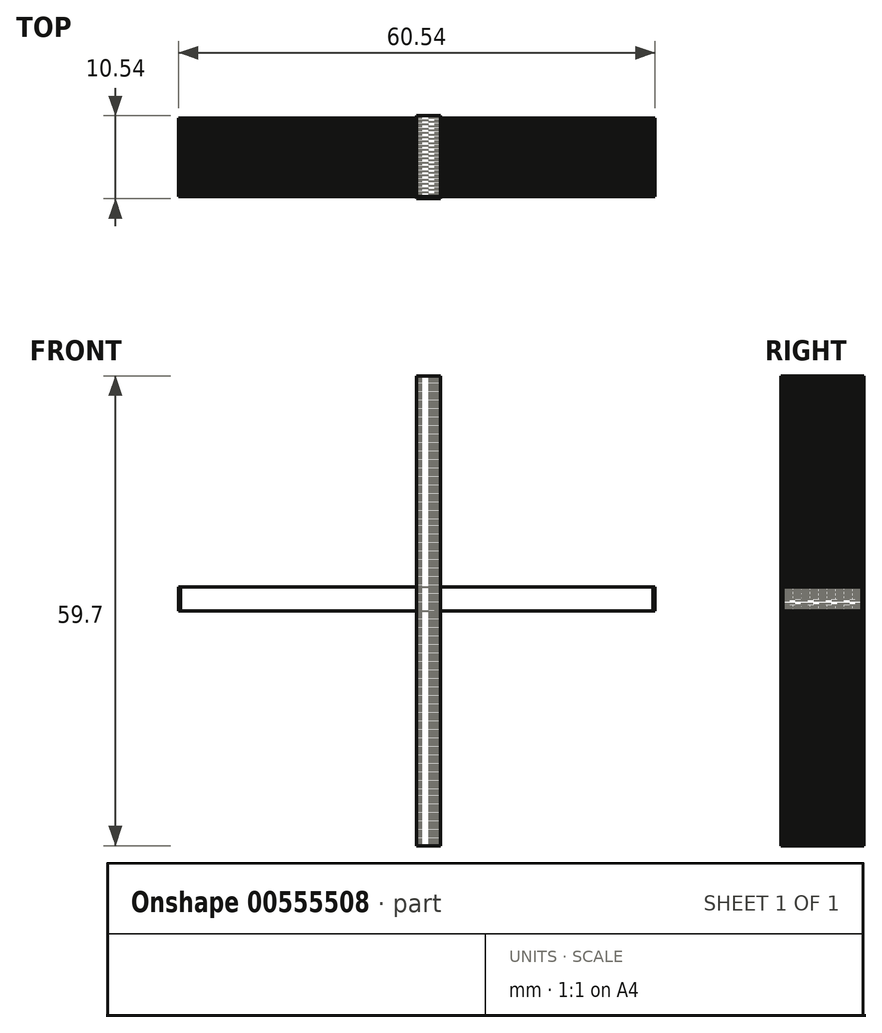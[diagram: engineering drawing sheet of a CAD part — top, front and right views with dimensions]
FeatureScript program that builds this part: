
annotation { "Feature Type Name" : "Feature", "Feature Type Description" : "" }
export const myFeature = defineFeature(function(context is Context, id is Id, definition is map)
    precondition{}
    {
        {
            var Q0;
            Q0=qCreatedBy(makeId("Top.planeOp"),FACE);
            var sketch = newSketch(context, id + "F0", { "sketchPlane" : qUnion([Q0])});
            skLineSegment(sketch, "E0.bottom", {"start": v(10, 5) * mm, "end": v(-10, 5) * mm});
            skLineSegment(sketch, "E0.top", {"start": v(10, -5) * mm, "end": v(-10, -5) * mm});
            skLineSegment(sketch, "E0.left", {"start": v(10, 5) * mm, "end": v(10, -5) * mm});
            skLineSegment(sketch, "E0.right", {"start": v(-10, 5) * mm, "end": v(-10, -5) * mm});
            skPoint(sketch, "E0.middle", {"position": v(0, 0) * mm});
            skLineSegment(sketch, "E1", {"start": v(-10, 4.73) * mm, "end": v(10, 4.73) * mm});
            skLineSegment(sketch, "E2.bottom", {"start": v(-10, 5) * mm, "end": v(-10.27, 5) * mm});
            skLineSegment(sketch, "E2.top", {"start": v(-10, -5) * mm, "end": v(-10.27, -5) * mm});
            skLineSegment(sketch, "E2.right", {"start": v(-10.27, 5) * mm, "end": v(-10.27, -5) * mm});
            skLineSegment(sketch, "E3.MirrorCS", {"start": v(10, 4.46) * mm, "end": v(-10, 4.46) * mm});
            skLineSegment(sketch, "E4.MirrorCS", {"start": v(10, 3.92) * mm, "end": v(-10, 3.92) * mm});
            skLineSegment(sketch, "E5.MirrorCS", {"start": v(-10, 4.19) * mm, "end": v(10, 4.2) * mm});
            skLineSegment(sketch, "E6.MirrorCS", {"start": v(-10, 3.65) * mm, "end": v(10, 3.65) * mm});
            skLineSegment(sketch, "E7.MirrorCS", {"start": v(10, 3.38) * mm, "end": v(-10, 3.38) * mm});
            skLineSegment(sketch, "E8.MirrorCS", {"start": v(-10, 3.11) * mm, "end": v(10, 3.11) * mm});
            skLineSegment(sketch, "E9.MirrorCS", {"start": v(10, 2.84) * mm, "end": v(-10, 2.84) * mm});
            skLineSegment(sketch, "E10.MirrorCS", {"start": v(-10, 2.57) * mm, "end": v(10, 2.57) * mm});
            skLineSegment(sketch, "E11.MirrorCS", {"start": v(10, 2.3) * mm, "end": v(-10, 2.3) * mm});
            skLineSegment(sketch, "E12.MirrorCS", {"start": v(-10, 2.03) * mm, "end": v(10, 2.03) * mm});
            skLineSegment(sketch, "E13.MirrorCS", {"start": v(10, 1.76) * mm, "end": v(-10, 1.76) * mm});
            skLineSegment(sketch, "E14.MirrorCS", {"start": v(-10, 1.49) * mm, "end": v(10, 1.5) * mm});
            skLineSegment(sketch, "E15.MirrorCS", {"start": v(10, 1.22) * mm, "end": v(-10, 1.22) * mm});
            skLineSegment(sketch, "E16.MirrorCS", {"start": v(-10, 0.95) * mm, "end": v(10, 0.95) * mm});
            skLineSegment(sketch, "E17.MirrorCS", {"start": v(10, 0.68) * mm, "end": v(-10, 0.68) * mm});
            skLineSegment(sketch, "E18.MirrorCS", {"start": v(-10, 0.4) * mm, "end": v(10, 0.4) * mm});
            skLineSegment(sketch, "E19.MirrorCS", {"start": v(10, 0.14) * mm, "end": v(-10, 0.14) * mm});
            skLineSegment(sketch, "E20.MirrorCS", {"start": v(-10, -0.13) * mm, "end": v(10, -0.13) * mm});
            skLineSegment(sketch, "E21.MirrorCS", {"start": v(10, -0.4) * mm, "end": v(-10, -0.4) * mm});
            skLineSegment(sketch, "E22.MirrorCS", {"start": v(-10, -0.67) * mm, "end": v(10, -0.67) * mm});
            skLineSegment(sketch, "E23.MirrorCS", {"start": v(10, -0.94) * mm, "end": v(-10, -0.94) * mm});
            skLineSegment(sketch, "E24.MirrorCS", {"start": v(-10, -1.21) * mm, "end": v(10, -1.21) * mm});
            skLineSegment(sketch, "E25.MirrorCS", {"start": v(10, -1.48) * mm, "end": v(-10, -1.48) * mm});
            skLineSegment(sketch, "E26.MirrorCS", {"start": v(-10, -1.75) * mm, "end": v(10, -1.75) * mm});
            skLineSegment(sketch, "E27.MirrorCS", {"start": v(10, -2.02) * mm, "end": v(-10, -2.02) * mm});
            skLineSegment(sketch, "E28.MirrorCS", {"start": v(-10, -2.3) * mm, "end": v(10, -2.3) * mm});
            skLineSegment(sketch, "E29.MirrorCS", {"start": v(10, -2.56) * mm, "end": v(-10, -2.56) * mm});
            skLineSegment(sketch, "E30.MirrorCS", {"start": v(-10, -2.83) * mm, "end": v(10, -2.83) * mm});
            skLineSegment(sketch, "E31.MirrorCS", {"start": v(10, -3.1) * mm, "end": v(-10, -3.1) * mm});
            skLineSegment(sketch, "E32.MirrorCS", {"start": v(-10, -3.37) * mm, "end": v(10, -3.37) * mm});
            skLineSegment(sketch, "E33.MirrorCS", {"start": v(10, -3.64) * mm, "end": v(-10, -3.64) * mm});
            skLineSegment(sketch, "E34.MirrorCS", {"start": v(-10, -3.91) * mm, "end": v(10, -3.91) * mm});
            skLineSegment(sketch, "E35.MirrorCS", {"start": v(10, -4.18) * mm, "end": v(-10, -4.18) * mm});
            skLineSegment(sketch, "E36.MirrorCS", {"start": v(-10, -4.45) * mm, "end": v(10, -4.45) * mm});
            skLineSegment(sketch, "E37.MirrorCS", {"start": v(10, -4.72) * mm, "end": v(-10, -4.72) * mm});
            skLineSegment(sketch, "E38.MirrorCS", {"start": v(-10, -5) * mm, "end": v(10, -5) * mm});
            skLineSegment(sketch, "E39.bottom", {"start": v(10, 5) * mm, "end": v(10.27, 5) * mm});
            skLineSegment(sketch, "E39.top", {"start": v(10, -5) * mm, "end": v(10.27, -5) * mm});
            skLineSegment(sketch, "E39.right", {"start": v(10.27, 5) * mm, "end": v(10.27, -5) * mm});
            skSolve(sketch);
        }
        {
            var Q0;
            Q0=qCreatedBy(makeId("Top.planeOp"),FACE);
            var sketch = newSketch(context, id + "F1", { "sketchPlane" : qUnion([Q0])});
            skLineSegment(sketch, "E40.bottom", {"start": v(30, 5) * mm, "end": v(-30, 5) * mm});
            skLineSegment(sketch, "E40.top", {"start": v(30, -5) * mm, "end": v(-30, -5) * mm});
            skLineSegment(sketch, "E40.left", {"start": v(30, 5) * mm, "end": v(30, -5) * mm});
            skLineSegment(sketch, "E40.right", {"start": v(-30, 5) * mm, "end": v(-30, -5) * mm});
            skPoint(sketch, "E40.middle", {"position": v(0, 0) * mm});
            skLineSegment(sketch, "E41", {"start": v(-30, 4.73) * mm, "end": v(30, 4.73) * mm});
            skLineSegment(sketch, "E42.bottom", {"start": v(-30, 5) * mm, "end": v(-30.27, 5) * mm});
            skLineSegment(sketch, "E42.top", {"start": v(-30, -5) * mm, "end": v(-30.27, -5) * mm});
            skLineSegment(sketch, "E42.right", {"start": v(-30.27, 5) * mm, "end": v(-30.27, -5) * mm});
            skLineSegment(sketch, "E43.MirrorCS", {"start": v(30, 4.46) * mm, "end": v(-30, 4.46) * mm});
            skLineSegment(sketch, "E44.MirrorCS", {"start": v(30, 3.92) * mm, "end": v(-30, 3.92) * mm});
            skLineSegment(sketch, "E45.MirrorCS", {"start": v(-30, 4.19) * mm, "end": v(30, 4.19) * mm});
            skLineSegment(sketch, "E46.MirrorCS", {"start": v(-30, 3.65) * mm, "end": v(30, 3.65) * mm});
            skLineSegment(sketch, "E47.MirrorCS", {"start": v(30, 3.38) * mm, "end": v(-30, 3.38) * mm});
            skLineSegment(sketch, "E48.MirrorCS", {"start": v(-30, 3.1) * mm, "end": v(30, 3.1) * mm});
            skLineSegment(sketch, "E49.MirrorCS", {"start": v(30, 2.84) * mm, "end": v(-30, 2.84) * mm});
            skLineSegment(sketch, "E50.MirrorCS", {"start": v(-30, 2.57) * mm, "end": v(30, 2.57) * mm});
            skLineSegment(sketch, "E51.MirrorCS", {"start": v(30, 2.3) * mm, "end": v(-30, 2.3) * mm});
            skLineSegment(sketch, "E52.MirrorCS", {"start": v(-30, 2.03) * mm, "end": v(30, 2.03) * mm});
            skLineSegment(sketch, "E53.MirrorCS", {"start": v(30, 1.76) * mm, "end": v(-30, 1.76) * mm});
            skLineSegment(sketch, "E54.MirrorCS", {"start": v(-30, 1.49) * mm, "end": v(30, 1.49) * mm});
            skLineSegment(sketch, "E55.MirrorCS", {"start": v(30, 1.22) * mm, "end": v(-30, 1.22) * mm});
            skLineSegment(sketch, "E56.MirrorCS", {"start": v(-30, 0.95) * mm, "end": v(30, 0.95) * mm});
            skLineSegment(sketch, "E57.MirrorCS", {"start": v(30, 0.68) * mm, "end": v(-30, 0.68) * mm});
            skLineSegment(sketch, "E58.MirrorCS", {"start": v(-30, 0.4) * mm, "end": v(30, 0.4) * mm});
            skLineSegment(sketch, "E59.MirrorCS", {"start": v(30, 0.14) * mm, "end": v(-30, 0.14) * mm});
            skLineSegment(sketch, "E60.MirrorCS", {"start": v(-30, -0.13) * mm, "end": v(30, -0.13) * mm});
            skLineSegment(sketch, "E61.MirrorCS", {"start": v(30, -0.4) * mm, "end": v(-30, -0.4) * mm});
            skLineSegment(sketch, "E62.MirrorCS", {"start": v(-30, -0.67) * mm, "end": v(30, -0.67) * mm});
            skLineSegment(sketch, "E63.MirrorCS", {"start": v(30, -0.94) * mm, "end": v(-30, -0.94) * mm});
            skLineSegment(sketch, "E64.MirrorCS", {"start": v(-30, -1.21) * mm, "end": v(30, -1.21) * mm});
            skLineSegment(sketch, "E65.MirrorCS", {"start": v(30, -1.48) * mm, "end": v(-30, -1.48) * mm});
            skLineSegment(sketch, "E66.MirrorCS", {"start": v(-30, -1.75) * mm, "end": v(30, -1.75) * mm});
            skLineSegment(sketch, "E67.MirrorCS", {"start": v(30, -2.02) * mm, "end": v(-30, -2.02) * mm});
            skLineSegment(sketch, "E68.MirrorCS", {"start": v(-30, -2.3) * mm, "end": v(30, -2.3) * mm});
            skLineSegment(sketch, "E69.MirrorCS", {"start": v(30, -2.56) * mm, "end": v(-30, -2.56) * mm});
            skLineSegment(sketch, "E70.MirrorCS", {"start": v(-30, -2.83) * mm, "end": v(30, -2.83) * mm});
            skLineSegment(sketch, "E71.MirrorCS", {"start": v(30, -3.1) * mm, "end": v(-30, -3.1) * mm});
            skLineSegment(sketch, "E72.MirrorCS", {"start": v(-30, -3.37) * mm, "end": v(30, -3.37) * mm});
            skLineSegment(sketch, "E73.MirrorCS", {"start": v(30, -3.64) * mm, "end": v(-30, -3.64) * mm});
            skLineSegment(sketch, "E74.MirrorCS", {"start": v(-30, -3.91) * mm, "end": v(30, -3.91) * mm});
            skLineSegment(sketch, "E75.MirrorCS", {"start": v(30, -4.18) * mm, "end": v(-30, -4.18) * mm});
            skLineSegment(sketch, "E76.MirrorCS", {"start": v(-30, -4.45) * mm, "end": v(30, -4.45) * mm});
            skLineSegment(sketch, "E77.MirrorCS", {"start": v(30, -4.72) * mm, "end": v(-30, -4.72) * mm});
            skLineSegment(sketch, "E78.MirrorCS", {"start": v(-30, -5) * mm, "end": v(30, -5) * mm});
            skLineSegment(sketch, "E79.bottom", {"start": v(30, 5) * mm, "end": v(30.27, 5) * mm});
            skLineSegment(sketch, "E79.top", {"start": v(30, -4.99) * mm, "end": v(30.27, -4.99) * mm});
            skLineSegment(sketch, "E79.left", {"start": v(30, 5) * mm, "end": v(30, -4.99) * mm});
            skLineSegment(sketch, "E79.right", {"start": v(30.27, 5) * mm, "end": v(30.27, -4.99) * mm});
            skSolve(sketch);
        }
        {
            var Q0;
            {var subQ38=sQuery(id+"F1.wireOp",EDGE,"E42.bottom");Q0=makeQuery(id+"F1.imprint","IMPRINT",FACE,{"disambiguationData":[TD([[makeQuery(id+"F1.imprint","IMPRINT",EDGE,{"derivedFrom":subQ38}),1.0]])]});}
            var Q1;
            {var subQ0=sQuery(id+"F1.wireOp",EDGE,"E40.bottom");Q1=makeQuery(id+"F1.imprint","IMPRINT",FACE,{"disambiguationData":[TD([[makeQuery(id+"F1.imprint","IMPRINT",EDGE,{"derivedFrom":subQ0}),1.0]])]});}
            var Q2;
            {var subQ0=sQuery(id+"F1.wireOp",EDGE,"E43.MirrorCS");Q2=makeQuery(id+"F1.imprint","IMPRINT",FACE,{"disambiguationData":[TD([[makeQuery(id+"F1.imprint","IMPRINT",EDGE,{"derivedFrom":subQ0}),1.0]])]});}
            var Q3;
            {var subQ0=sQuery(id+"F1.wireOp",EDGE,"E44.MirrorCS");Q3=makeQuery(id+"F1.imprint","IMPRINT",FACE,{"disambiguationData":[TD([[makeQuery(id+"F1.imprint","IMPRINT",EDGE,{"derivedFrom":subQ0}),1.0]])]});}
            var Q4;
            {var subQ0=sQuery(id+"F1.wireOp",EDGE,"E47.MirrorCS");Q4=makeQuery(id+"F1.imprint","IMPRINT",FACE,{"disambiguationData":[TD([[makeQuery(id+"F1.imprint","IMPRINT",EDGE,{"derivedFrom":subQ0}),1.0]])]});}
            var Q5;
            {var subQ0=sQuery(id+"F1.wireOp",EDGE,"E49.MirrorCS");Q5=makeQuery(id+"F1.imprint","IMPRINT",FACE,{"disambiguationData":[TD([[makeQuery(id+"F1.imprint","IMPRINT",EDGE,{"derivedFrom":subQ0}),1.0]])]});}
            var Q6;
            {var subQ0=sQuery(id+"F1.wireOp",EDGE,"E51.MirrorCS");Q6=makeQuery(id+"F1.imprint","IMPRINT",FACE,{"disambiguationData":[TD([[makeQuery(id+"F1.imprint","IMPRINT",EDGE,{"derivedFrom":subQ0}),1.0]])]});}
            var Q7;
            {var subQ0=sQuery(id+"F1.wireOp",EDGE,"E53.MirrorCS");Q7=makeQuery(id+"F1.imprint","IMPRINT",FACE,{"disambiguationData":[TD([[makeQuery(id+"F1.imprint","IMPRINT",EDGE,{"derivedFrom":subQ0}),1.0]])]});}
            var Q8;
            {var subQ0=sQuery(id+"F1.wireOp",EDGE,"E55.MirrorCS");Q8=makeQuery(id+"F1.imprint","IMPRINT",FACE,{"disambiguationData":[TD([[makeQuery(id+"F1.imprint","IMPRINT",EDGE,{"derivedFrom":subQ0}),1.0]])]});}
            var Q9;
            {var subQ0=sQuery(id+"F1.wireOp",EDGE,"E57.MirrorCS");Q9=makeQuery(id+"F1.imprint","IMPRINT",FACE,{"disambiguationData":[TD([[makeQuery(id+"F1.imprint","IMPRINT",EDGE,{"derivedFrom":subQ0}),1.0]])]});}
            var Q10;
            {var subQ0=sQuery(id+"F1.wireOp",EDGE,"E59.MirrorCS");Q10=makeQuery(id+"F1.imprint","IMPRINT",FACE,{"disambiguationData":[TD([[makeQuery(id+"F1.imprint","IMPRINT",EDGE,{"derivedFrom":subQ0}),1.0]])]});}
            var Q11;
            {var subQ0=sQuery(id+"F1.wireOp",EDGE,"E61.MirrorCS");Q11=makeQuery(id+"F1.imprint","IMPRINT",FACE,{"disambiguationData":[TD([[makeQuery(id+"F1.imprint","IMPRINT",EDGE,{"derivedFrom":subQ0}),1.0]])]});}
            var Q12;
            {var subQ0=sQuery(id+"F1.wireOp",EDGE,"E63.MirrorCS");Q12=makeQuery(id+"F1.imprint","IMPRINT",FACE,{"disambiguationData":[TD([[makeQuery(id+"F1.imprint","IMPRINT",EDGE,{"derivedFrom":subQ0}),1.0]])]});}
            var Q13;
            {var subQ0=sQuery(id+"F1.wireOp",EDGE,"E65.MirrorCS");Q13=makeQuery(id+"F1.imprint","IMPRINT",FACE,{"disambiguationData":[TD([[makeQuery(id+"F1.imprint","IMPRINT",EDGE,{"derivedFrom":subQ0}),1.0]])]});}
            var Q14;
            {var subQ2=sQuery(id+"F1.wireOp",EDGE,"E67.MirrorCS");Q14=makeQuery(id+"F1.imprint","IMPRINT",FACE,{"disambiguationData":[TD([[makeQuery(id+"F1.imprint","IMPRINT",EDGE,{"derivedFrom":subQ2}),1.0]])]});}
            var Q15;
            {var subQ0=sQuery(id+"F1.wireOp",EDGE,"E69.MirrorCS");Q15=makeQuery(id+"F1.imprint","IMPRINT",FACE,{"disambiguationData":[TD([[makeQuery(id+"F1.imprint","IMPRINT",EDGE,{"derivedFrom":subQ0}),1.0]])]});}
            var Q16;
            {var subQ0=sQuery(id+"F1.wireOp",EDGE,"E71.MirrorCS");Q16=makeQuery(id+"F1.imprint","IMPRINT",FACE,{"disambiguationData":[TD([[makeQuery(id+"F1.imprint","IMPRINT",EDGE,{"derivedFrom":subQ0}),1.0]])]});}
            var Q17;
            {var subQ0=sQuery(id+"F1.wireOp",EDGE,"E73.MirrorCS");Q17=makeQuery(id+"F1.imprint","IMPRINT",FACE,{"disambiguationData":[TD([[makeQuery(id+"F1.imprint","IMPRINT",EDGE,{"derivedFrom":subQ0}),1.0]])]});}
            var Q18;
            {var subQ0=sQuery(id+"F1.wireOp",EDGE,"E75.MirrorCS");Q18=makeQuery(id+"F1.imprint","IMPRINT",FACE,{"disambiguationData":[TD([[makeQuery(id+"F1.imprint","IMPRINT",EDGE,{"derivedFrom":subQ0}),1.0]])]});}
            var Q19;
            {var subQ0=sQuery(id+"F1.wireOp",EDGE,"E77.MirrorCS");Q19=makeQuery(id+"F1.imprint","IMPRINT",FACE,{"disambiguationData":[TD([[makeQuery(id+"F1.imprint","IMPRINT",EDGE,{"derivedFrom":subQ0}),1.0]])]});}
            extrude(context, id + "F2", {"entities" : qUnion([Q0, Q1, Q2, Q3, Q4, Q5, Q6, Q7, Q8, Q9, Q10, Q11, Q12, Q13, Q14, Q15, Q16, Q17, Q18, Q19]), "depth" : 3 * mm, "offsetDistance" : 25 * mm});
        }
        {
            var Q0;
            {var subQ33=sQuery(id+"F1.wireOp",EDGE,"E79.bottom");Q0=makeQuery(id+"F1.imprint","IMPRINT",FACE,{"disambiguationData":[TD([[makeQuery(id+"F1.imprint","IMPRINT",EDGE,{"derivedFrom":subQ33}),-1.0]])]});}
            var Q1;
            {var subQ0=sQuery(id+"F1.wireOp",EDGE,"E41");Q1=makeQuery(id+"F1.imprint","IMPRINT",FACE,{"disambiguationData":[TD([[makeQuery(id+"F1.imprint","IMPRINT",EDGE,{"derivedFrom":subQ0}),-1.0]])]});}
            var Q2;
            {var subQ0=sQuery(id+"F1.wireOp",EDGE,"E44.MirrorCS");Q2=makeQuery(id+"F1.imprint","IMPRINT",FACE,{"disambiguationData":[TD([[makeQuery(id+"F1.imprint","IMPRINT",EDGE,{"derivedFrom":subQ0}),-1.0]])]});}
            var Q3;
            {var subQ0=sQuery(id+"F1.wireOp",EDGE,"E46.MirrorCS");Q3=makeQuery(id+"F1.imprint","IMPRINT",FACE,{"disambiguationData":[TD([[makeQuery(id+"F1.imprint","IMPRINT",EDGE,{"derivedFrom":subQ0}),-1.0]])]});}
            var Q4;
            {var subQ0=sQuery(id+"F1.wireOp",EDGE,"E48.MirrorCS");Q4=makeQuery(id+"F1.imprint","IMPRINT",FACE,{"disambiguationData":[TD([[makeQuery(id+"F1.imprint","IMPRINT",EDGE,{"derivedFrom":subQ0}),-1.0]])]});}
            var Q5;
            {var subQ0=sQuery(id+"F1.wireOp",EDGE,"E50.MirrorCS");Q5=makeQuery(id+"F1.imprint","IMPRINT",FACE,{"disambiguationData":[TD([[makeQuery(id+"F1.imprint","IMPRINT",EDGE,{"derivedFrom":subQ0}),-1.0]])]});}
            var Q6;
            {var subQ0=sQuery(id+"F1.wireOp",EDGE,"E52.MirrorCS");Q6=makeQuery(id+"F1.imprint","IMPRINT",FACE,{"disambiguationData":[TD([[makeQuery(id+"F1.imprint","IMPRINT",EDGE,{"derivedFrom":subQ0}),-1.0]])]});}
            var Q7;
            {var subQ0=sQuery(id+"F1.wireOp",EDGE,"E54.MirrorCS");Q7=makeQuery(id+"F1.imprint","IMPRINT",FACE,{"disambiguationData":[TD([[makeQuery(id+"F1.imprint","IMPRINT",EDGE,{"derivedFrom":subQ0}),-1.0]])]});}
            var Q8;
            {var subQ0=sQuery(id+"F1.wireOp",EDGE,"E56.MirrorCS");Q8=makeQuery(id+"F1.imprint","IMPRINT",FACE,{"disambiguationData":[TD([[makeQuery(id+"F1.imprint","IMPRINT",EDGE,{"derivedFrom":subQ0}),-1.0]])]});}
            var Q9;
            {var subQ0=sQuery(id+"F1.wireOp",EDGE,"E58.MirrorCS");Q9=makeQuery(id+"F1.imprint","IMPRINT",FACE,{"disambiguationData":[TD([[makeQuery(id+"F1.imprint","IMPRINT",EDGE,{"derivedFrom":subQ0}),-1.0]])]});}
            var Q10;
            {var subQ0=sQuery(id+"F1.wireOp",EDGE,"E60.MirrorCS");Q10=makeQuery(id+"F1.imprint","IMPRINT",FACE,{"disambiguationData":[TD([[makeQuery(id+"F1.imprint","IMPRINT",EDGE,{"derivedFrom":subQ0}),-1.0]])]});}
            var Q11;
            {var subQ0=sQuery(id+"F1.wireOp",EDGE,"E62.MirrorCS");Q11=makeQuery(id+"F1.imprint","IMPRINT",FACE,{"disambiguationData":[TD([[makeQuery(id+"F1.imprint","IMPRINT",EDGE,{"derivedFrom":subQ0}),-1.0]])]});}
            var Q12;
            {var subQ0=sQuery(id+"F1.wireOp",EDGE,"E64.MirrorCS");Q12=makeQuery(id+"F1.imprint","IMPRINT",FACE,{"disambiguationData":[TD([[makeQuery(id+"F1.imprint","IMPRINT",EDGE,{"derivedFrom":subQ0}),-1.0]])]});}
            var Q13;
            {var subQ0=sQuery(id+"F1.wireOp",EDGE,"E66.MirrorCS");Q13=makeQuery(id+"F1.imprint","IMPRINT",FACE,{"disambiguationData":[TD([[makeQuery(id+"F1.imprint","IMPRINT",EDGE,{"derivedFrom":subQ0}),-1.0]])]});}
            var Q14;
            {var subQ0=sQuery(id+"F1.wireOp",EDGE,"E68.MirrorCS");Q14=makeQuery(id+"F1.imprint","IMPRINT",FACE,{"disambiguationData":[TD([[makeQuery(id+"F1.imprint","IMPRINT",EDGE,{"derivedFrom":subQ0}),-1.0]])]});}
            var Q15;
            {var subQ0=sQuery(id+"F1.wireOp",EDGE,"E70.MirrorCS");Q15=makeQuery(id+"F1.imprint","IMPRINT",FACE,{"disambiguationData":[TD([[makeQuery(id+"F1.imprint","IMPRINT",EDGE,{"derivedFrom":subQ0}),-1.0]])]});}
            var Q16;
            {var subQ0=sQuery(id+"F1.wireOp",EDGE,"E72.MirrorCS");Q16=makeQuery(id+"F1.imprint","IMPRINT",FACE,{"disambiguationData":[TD([[makeQuery(id+"F1.imprint","IMPRINT",EDGE,{"derivedFrom":subQ0}),-1.0]])]});}
            var Q17;
            {var subQ0=sQuery(id+"F1.wireOp",EDGE,"E74.MirrorCS");Q17=makeQuery(id+"F1.imprint","IMPRINT",FACE,{"disambiguationData":[TD([[makeQuery(id+"F1.imprint","IMPRINT",EDGE,{"derivedFrom":subQ0}),-1.0]])]});}
            var Q18;
            {var subQ0=sQuery(id+"F1.wireOp",EDGE,"E76.MirrorCS");Q18=makeQuery(id+"F1.imprint","IMPRINT",FACE,{"disambiguationData":[TD([[makeQuery(id+"F1.imprint","IMPRINT",EDGE,{"derivedFrom":subQ0}),-1.0]])]});}
            extrude(context, id + "F3", {"entities" : qUnion([Q0, Q1, Q2, Q3, Q4, Q5, Q6, Q7, Q8, Q9, Q10, Q11, Q12, Q13, Q14, Q15, Q16, Q17, Q18]), "depth" : 3 * mm, "offsetDistance" : 25 * mm});
        }
        {
            var Q0;
            {var subQ38=sQuery(id+"F1.wireOp",EDGE,"E42.bottom");Q0=makeQuery(id+"F1.imprint","IMPRINT",FACE,{"disambiguationData":[TD([[makeQuery(id+"F1.imprint","IMPRINT",EDGE,{"derivedFrom":subQ38}),1.0]])]});}
            var Q1;
            {var subQ0=sQuery(id+"F1.wireOp",EDGE,"E40.bottom");Q1=makeQuery(id+"F1.imprint","IMPRINT",FACE,{"disambiguationData":[TD([[makeQuery(id+"F1.imprint","IMPRINT",EDGE,{"derivedFrom":subQ0}),1.0]])]});}
            var Q2;
            {var subQ0=sQuery(id+"F1.wireOp",EDGE,"E41");Q2=makeQuery(id+"F1.imprint","IMPRINT",FACE,{"disambiguationData":[TD([[makeQuery(id+"F1.imprint","IMPRINT",EDGE,{"derivedFrom":subQ0}),-1.0]])]});}
            var Q3;
            {var subQ0=sQuery(id+"F1.wireOp",EDGE,"E43.MirrorCS");Q3=makeQuery(id+"F1.imprint","IMPRINT",FACE,{"disambiguationData":[TD([[makeQuery(id+"F1.imprint","IMPRINT",EDGE,{"derivedFrom":subQ0}),1.0]])]});}
            var Q4;
            {var subQ0=sQuery(id+"F1.wireOp",EDGE,"E44.MirrorCS");Q4=makeQuery(id+"F1.imprint","IMPRINT",FACE,{"disambiguationData":[TD([[makeQuery(id+"F1.imprint","IMPRINT",EDGE,{"derivedFrom":subQ0}),1.0]])]});}
            var Q5;
            {var subQ0=sQuery(id+"F1.wireOp",EDGE,"E47.MirrorCS");Q5=makeQuery(id+"F1.imprint","IMPRINT",FACE,{"disambiguationData":[TD([[makeQuery(id+"F1.imprint","IMPRINT",EDGE,{"derivedFrom":subQ0}),1.0]])]});}
            var Q6;
            {var subQ0=sQuery(id+"F1.wireOp",EDGE,"E46.MirrorCS");Q6=makeQuery(id+"F1.imprint","IMPRINT",FACE,{"disambiguationData":[TD([[makeQuery(id+"F1.imprint","IMPRINT",EDGE,{"derivedFrom":subQ0}),-1.0]])]});}
            var Q7;
            {var subQ0=sQuery(id+"F1.wireOp",EDGE,"E49.MirrorCS");Q7=makeQuery(id+"F1.imprint","IMPRINT",FACE,{"disambiguationData":[TD([[makeQuery(id+"F1.imprint","IMPRINT",EDGE,{"derivedFrom":subQ0}),1.0]])]});}
            var Q8;
            {var subQ0=sQuery(id+"F1.wireOp",EDGE,"E50.MirrorCS");Q8=makeQuery(id+"F1.imprint","IMPRINT",FACE,{"disambiguationData":[TD([[makeQuery(id+"F1.imprint","IMPRINT",EDGE,{"derivedFrom":subQ0}),-1.0]])]});}
            var Q9;
            {var subQ0=sQuery(id+"F1.wireOp",EDGE,"E51.MirrorCS");Q9=makeQuery(id+"F1.imprint","IMPRINT",FACE,{"disambiguationData":[TD([[makeQuery(id+"F1.imprint","IMPRINT",EDGE,{"derivedFrom":subQ0}),1.0]])]});}
            var Q10;
            {var subQ0=sQuery(id+"F1.wireOp",EDGE,"E53.MirrorCS");Q10=makeQuery(id+"F1.imprint","IMPRINT",FACE,{"disambiguationData":[TD([[makeQuery(id+"F1.imprint","IMPRINT",EDGE,{"derivedFrom":subQ0}),1.0]])]});}
            var Q11;
            {var subQ0=sQuery(id+"F1.wireOp",EDGE,"E54.MirrorCS");Q11=makeQuery(id+"F1.imprint","IMPRINT",FACE,{"disambiguationData":[TD([[makeQuery(id+"F1.imprint","IMPRINT",EDGE,{"derivedFrom":subQ0}),-1.0]])]});}
            var Q12;
            {var subQ0=sQuery(id+"F1.wireOp",EDGE,"E55.MirrorCS");Q12=makeQuery(id+"F1.imprint","IMPRINT",FACE,{"disambiguationData":[TD([[makeQuery(id+"F1.imprint","IMPRINT",EDGE,{"derivedFrom":subQ0}),1.0]])]});}
            var Q13;
            {var subQ0=sQuery(id+"F1.wireOp",EDGE,"E57.MirrorCS");Q13=makeQuery(id+"F1.imprint","IMPRINT",FACE,{"disambiguationData":[TD([[makeQuery(id+"F1.imprint","IMPRINT",EDGE,{"derivedFrom":subQ0}),1.0]])]});}
            var Q14;
            {var subQ0=sQuery(id+"F1.wireOp",EDGE,"E58.MirrorCS");Q14=makeQuery(id+"F1.imprint","IMPRINT",FACE,{"disambiguationData":[TD([[makeQuery(id+"F1.imprint","IMPRINT",EDGE,{"derivedFrom":subQ0}),-1.0]])]});}
            var Q15;
            {var subQ0=sQuery(id+"F1.wireOp",EDGE,"E59.MirrorCS");Q15=makeQuery(id+"F1.imprint","IMPRINT",FACE,{"disambiguationData":[TD([[makeQuery(id+"F1.imprint","IMPRINT",EDGE,{"derivedFrom":subQ0}),1.0]])]});}
            var Q16;
            {var subQ0=sQuery(id+"F1.wireOp",EDGE,"E61.MirrorCS");Q16=makeQuery(id+"F1.imprint","IMPRINT",FACE,{"disambiguationData":[TD([[makeQuery(id+"F1.imprint","IMPRINT",EDGE,{"derivedFrom":subQ0}),1.0]])]});}
            var Q17;
            {var subQ0=sQuery(id+"F1.wireOp",EDGE,"E62.MirrorCS");Q17=makeQuery(id+"F1.imprint","IMPRINT",FACE,{"disambiguationData":[TD([[makeQuery(id+"F1.imprint","IMPRINT",EDGE,{"derivedFrom":subQ0}),-1.0]])]});}
            var Q18;
            {var subQ0=sQuery(id+"F1.wireOp",EDGE,"E63.MirrorCS");Q18=makeQuery(id+"F1.imprint","IMPRINT",FACE,{"disambiguationData":[TD([[makeQuery(id+"F1.imprint","IMPRINT",EDGE,{"derivedFrom":subQ0}),1.0]])]});}
            var Q19;
            {var subQ0=sQuery(id+"F1.wireOp",EDGE,"E65.MirrorCS");Q19=makeQuery(id+"F1.imprint","IMPRINT",FACE,{"disambiguationData":[TD([[makeQuery(id+"F1.imprint","IMPRINT",EDGE,{"derivedFrom":subQ0}),1.0]])]});}
            var Q20;
            {var subQ0=sQuery(id+"F1.wireOp",EDGE,"E66.MirrorCS");Q20=makeQuery(id+"F1.imprint","IMPRINT",FACE,{"disambiguationData":[TD([[makeQuery(id+"F1.imprint","IMPRINT",EDGE,{"derivedFrom":subQ0}),-1.0]])]});}
            var Q21;
            {var subQ2=sQuery(id+"F1.wireOp",EDGE,"E67.MirrorCS");Q21=makeQuery(id+"F1.imprint","IMPRINT",FACE,{"disambiguationData":[TD([[makeQuery(id+"F1.imprint","IMPRINT",EDGE,{"derivedFrom":subQ2}),1.0]])]});}
            var Q22;
            {var subQ0=sQuery(id+"F1.wireOp",EDGE,"E69.MirrorCS");Q22=makeQuery(id+"F1.imprint","IMPRINT",FACE,{"disambiguationData":[TD([[makeQuery(id+"F1.imprint","IMPRINT",EDGE,{"derivedFrom":subQ0}),1.0]])]});}
            var Q23;
            {var subQ0=sQuery(id+"F1.wireOp",EDGE,"E70.MirrorCS");Q23=makeQuery(id+"F1.imprint","IMPRINT",FACE,{"disambiguationData":[TD([[makeQuery(id+"F1.imprint","IMPRINT",EDGE,{"derivedFrom":subQ0}),-1.0]])]});}
            var Q24;
            {var subQ0=sQuery(id+"F1.wireOp",EDGE,"E71.MirrorCS");Q24=makeQuery(id+"F1.imprint","IMPRINT",FACE,{"disambiguationData":[TD([[makeQuery(id+"F1.imprint","IMPRINT",EDGE,{"derivedFrom":subQ0}),1.0]])]});}
            var Q25;
            {var subQ0=sQuery(id+"F1.wireOp",EDGE,"E73.MirrorCS");Q25=makeQuery(id+"F1.imprint","IMPRINT",FACE,{"disambiguationData":[TD([[makeQuery(id+"F1.imprint","IMPRINT",EDGE,{"derivedFrom":subQ0}),1.0]])]});}
            var Q26;
            {var subQ0=sQuery(id+"F1.wireOp",EDGE,"E74.MirrorCS");Q26=makeQuery(id+"F1.imprint","IMPRINT",FACE,{"disambiguationData":[TD([[makeQuery(id+"F1.imprint","IMPRINT",EDGE,{"derivedFrom":subQ0}),-1.0]])]});}
            var Q27;
            {var subQ0=sQuery(id+"F1.wireOp",EDGE,"E75.MirrorCS");Q27=makeQuery(id+"F1.imprint","IMPRINT",FACE,{"disambiguationData":[TD([[makeQuery(id+"F1.imprint","IMPRINT",EDGE,{"derivedFrom":subQ0}),1.0]])]});}
            var Q28;
            {var subQ0=sQuery(id+"F1.wireOp",EDGE,"E77.MirrorCS");Q28=makeQuery(id+"F1.imprint","IMPRINT",FACE,{"disambiguationData":[TD([[makeQuery(id+"F1.imprint","IMPRINT",EDGE,{"derivedFrom":subQ0}),1.0]])]});}
            extrude(context, id + "F4", {"entities" : qUnion([Q0, Q1, Q2, Q3, Q4, Q5, Q6, Q7, Q8, Q9, Q10, Q11, Q12, Q13, Q14, Q15, Q16, Q17, Q18, Q19, Q20, Q21, Q22, Q23, Q24, Q25, Q26, Q27, Q28]), "depth" : 3 * mm, "offsetDistance" : 25 * mm});
        }
        {
            var Q0;
            {var subQ0=sQuery(id+"F1.wireOp",EDGE,"E44.MirrorCS");Q0=makeQuery(id+"F1.imprint","IMPRINT",FACE,{"disambiguationData":[TD([[makeQuery(id+"F1.imprint","IMPRINT",EDGE,{"derivedFrom":subQ0}),-1.0]])]});}
            var Q1;
            {var subQ0=sQuery(id+"F1.wireOp",EDGE,"E48.MirrorCS");Q1=makeQuery(id+"F1.imprint","IMPRINT",FACE,{"disambiguationData":[TD([[makeQuery(id+"F1.imprint","IMPRINT",EDGE,{"derivedFrom":subQ0}),-1.0]])]});}
            var Q2;
            {var subQ0=sQuery(id+"F1.wireOp",EDGE,"E52.MirrorCS");Q2=makeQuery(id+"F1.imprint","IMPRINT",FACE,{"disambiguationData":[TD([[makeQuery(id+"F1.imprint","IMPRINT",EDGE,{"derivedFrom":subQ0}),-1.0]])]});}
            var Q3;
            {var subQ0=sQuery(id+"F1.wireOp",EDGE,"E56.MirrorCS");Q3=makeQuery(id+"F1.imprint","IMPRINT",FACE,{"disambiguationData":[TD([[makeQuery(id+"F1.imprint","IMPRINT",EDGE,{"derivedFrom":subQ0}),-1.0]])]});}
            var Q4;
            {var subQ0=sQuery(id+"F1.wireOp",EDGE,"E60.MirrorCS");Q4=makeQuery(id+"F1.imprint","IMPRINT",FACE,{"disambiguationData":[TD([[makeQuery(id+"F1.imprint","IMPRINT",EDGE,{"derivedFrom":subQ0}),-1.0]])]});}
            var Q5;
            {var subQ0=sQuery(id+"F1.wireOp",EDGE,"E64.MirrorCS");Q5=makeQuery(id+"F1.imprint","IMPRINT",FACE,{"disambiguationData":[TD([[makeQuery(id+"F1.imprint","IMPRINT",EDGE,{"derivedFrom":subQ0}),-1.0]])]});}
            var Q6;
            {var subQ0=sQuery(id+"F1.wireOp",EDGE,"E68.MirrorCS");Q6=makeQuery(id+"F1.imprint","IMPRINT",FACE,{"disambiguationData":[TD([[makeQuery(id+"F1.imprint","IMPRINT",EDGE,{"derivedFrom":subQ0}),-1.0]])]});}
            var Q7;
            {var subQ0=sQuery(id+"F1.wireOp",EDGE,"E72.MirrorCS");Q7=makeQuery(id+"F1.imprint","IMPRINT",FACE,{"disambiguationData":[TD([[makeQuery(id+"F1.imprint","IMPRINT",EDGE,{"derivedFrom":subQ0}),-1.0]])]});}
            var Q8;
            {var subQ0=sQuery(id+"F1.wireOp",EDGE,"E76.MirrorCS");Q8=makeQuery(id+"F1.imprint","IMPRINT",FACE,{"disambiguationData":[TD([[makeQuery(id+"F1.imprint","IMPRINT",EDGE,{"derivedFrom":subQ0}),-1.0]])]});}
            var Q9;
            {var subQ33=sQuery(id+"F1.wireOp",EDGE,"E79.bottom");Q9=makeQuery(id+"F1.imprint","IMPRINT",FACE,{"disambiguationData":[TD([[makeQuery(id+"F1.imprint","IMPRINT",EDGE,{"derivedFrom":subQ33}),-1.0]])]});}
            extrude(context, id + "F5", {"entities" : qUnion([Q0, Q1, Q2, Q3, Q4, Q5, Q6, Q7, Q8, Q9]), "depth" : 3 * mm, "offsetDistance" : 25 * mm});
        }
        {
            var Q0;
            {var subQ38=sQuery(id+"F1.wireOp",EDGE,"E42.bottom");Q0=makeQuery(id+"F1.imprint","IMPRINT",FACE,{"disambiguationData":[TD([[makeQuery(id+"F1.imprint","IMPRINT",EDGE,{"derivedFrom":subQ38}),1.0]])]});}
            var Q1;
            {var subQ0=sQuery(id+"F1.wireOp",EDGE,"E40.bottom");Q1=makeQuery(id+"F1.imprint","IMPRINT",FACE,{"disambiguationData":[TD([[makeQuery(id+"F1.imprint","IMPRINT",EDGE,{"derivedFrom":subQ0}),1.0]])]});}
            var Q2;
            {var subQ0=sQuery(id+"F1.wireOp",EDGE,"E41");Q2=makeQuery(id+"F1.imprint","IMPRINT",FACE,{"disambiguationData":[TD([[makeQuery(id+"F1.imprint","IMPRINT",EDGE,{"derivedFrom":subQ0}),-1.0]])]});}
            var Q3;
            {var subQ0=sQuery(id+"F1.wireOp",EDGE,"E43.MirrorCS");Q3=makeQuery(id+"F1.imprint","IMPRINT",FACE,{"disambiguationData":[TD([[makeQuery(id+"F1.imprint","IMPRINT",EDGE,{"derivedFrom":subQ0}),1.0]])]});}
            var Q4;
            {var subQ0=sQuery(id+"F1.wireOp",EDGE,"E44.MirrorCS");Q4=makeQuery(id+"F1.imprint","IMPRINT",FACE,{"disambiguationData":[TD([[makeQuery(id+"F1.imprint","IMPRINT",EDGE,{"derivedFrom":subQ0}),-1.0]])]});}
            var Q5;
            {var subQ0=sQuery(id+"F1.wireOp",EDGE,"E44.MirrorCS");Q5=makeQuery(id+"F1.imprint","IMPRINT",FACE,{"disambiguationData":[TD([[makeQuery(id+"F1.imprint","IMPRINT",EDGE,{"derivedFrom":subQ0}),1.0]])]});}
            var Q6;
            {var subQ0=sQuery(id+"F1.wireOp",EDGE,"E47.MirrorCS");Q6=makeQuery(id+"F1.imprint","IMPRINT",FACE,{"disambiguationData":[TD([[makeQuery(id+"F1.imprint","IMPRINT",EDGE,{"derivedFrom":subQ0}),1.0]])]});}
            var Q7;
            {var subQ0=sQuery(id+"F1.wireOp",EDGE,"E48.MirrorCS");Q7=makeQuery(id+"F1.imprint","IMPRINT",FACE,{"disambiguationData":[TD([[makeQuery(id+"F1.imprint","IMPRINT",EDGE,{"derivedFrom":subQ0}),-1.0]])]});}
            var Q8;
            {var subQ0=sQuery(id+"F1.wireOp",EDGE,"E49.MirrorCS");Q8=makeQuery(id+"F1.imprint","IMPRINT",FACE,{"disambiguationData":[TD([[makeQuery(id+"F1.imprint","IMPRINT",EDGE,{"derivedFrom":subQ0}),1.0]])]});}
            var Q9;
            {var subQ0=sQuery(id+"F1.wireOp",EDGE,"E53.MirrorCS");Q9=makeQuery(id+"F1.imprint","IMPRINT",FACE,{"disambiguationData":[TD([[makeQuery(id+"F1.imprint","IMPRINT",EDGE,{"derivedFrom":subQ0}),1.0]])]});}
            var Q10;
            {var subQ0=sQuery(id+"F1.wireOp",EDGE,"E55.MirrorCS");Q10=makeQuery(id+"F1.imprint","IMPRINT",FACE,{"disambiguationData":[TD([[makeQuery(id+"F1.imprint","IMPRINT",EDGE,{"derivedFrom":subQ0}),1.0]])]});}
            var Q11;
            {var subQ0=sQuery(id+"F1.wireOp",EDGE,"E59.MirrorCS");Q11=makeQuery(id+"F1.imprint","IMPRINT",FACE,{"disambiguationData":[TD([[makeQuery(id+"F1.imprint","IMPRINT",EDGE,{"derivedFrom":subQ0}),1.0]])]});}
            var Q12;
            {var subQ0=sQuery(id+"F1.wireOp",EDGE,"E63.MirrorCS");Q12=makeQuery(id+"F1.imprint","IMPRINT",FACE,{"disambiguationData":[TD([[makeQuery(id+"F1.imprint","IMPRINT",EDGE,{"derivedFrom":subQ0}),1.0]])]});}
            var Q13;
            {var subQ0=sQuery(id+"F1.wireOp",EDGE,"E70.MirrorCS");Q13=makeQuery(id+"F1.imprint","IMPRINT",FACE,{"disambiguationData":[TD([[makeQuery(id+"F1.imprint","IMPRINT",EDGE,{"derivedFrom":subQ0}),-1.0]])]});}
            var Q14;
            {var subQ0=sQuery(id+"F1.wireOp",EDGE,"E73.MirrorCS");Q14=makeQuery(id+"F1.imprint","IMPRINT",FACE,{"disambiguationData":[TD([[makeQuery(id+"F1.imprint","IMPRINT",EDGE,{"derivedFrom":subQ0}),1.0]])]});}
            var Q15;
            {var subQ0=sQuery(id+"F1.wireOp",EDGE,"E76.MirrorCS");Q15=makeQuery(id+"F1.imprint","IMPRINT",FACE,{"disambiguationData":[TD([[makeQuery(id+"F1.imprint","IMPRINT",EDGE,{"derivedFrom":subQ0}),-1.0]])]});}
            var Q16;
            {var subQ0=sQuery(id+"F1.wireOp",EDGE,"E77.MirrorCS");Q16=makeQuery(id+"F1.imprint","IMPRINT",FACE,{"disambiguationData":[TD([[makeQuery(id+"F1.imprint","IMPRINT",EDGE,{"derivedFrom":subQ0}),1.0]])]});}
            var Q17;
            {var subQ0=sQuery(id+"F1.wireOp",EDGE,"E74.MirrorCS");Q17=makeQuery(id+"F1.imprint","IMPRINT",FACE,{"disambiguationData":[TD([[makeQuery(id+"F1.imprint","IMPRINT",EDGE,{"derivedFrom":subQ0}),-1.0]])]});}
            var Q18;
            {var subQ0=sQuery(id+"F1.wireOp",EDGE,"E71.MirrorCS");Q18=makeQuery(id+"F1.imprint","IMPRINT",FACE,{"disambiguationData":[TD([[makeQuery(id+"F1.imprint","IMPRINT",EDGE,{"derivedFrom":subQ0}),1.0]])]});}
            var Q19;
            {var subQ0=sQuery(id+"F1.wireOp",EDGE,"E68.MirrorCS");Q19=makeQuery(id+"F1.imprint","IMPRINT",FACE,{"disambiguationData":[TD([[makeQuery(id+"F1.imprint","IMPRINT",EDGE,{"derivedFrom":subQ0}),-1.0]])]});}
            var Q20;
            {var subQ2=sQuery(id+"F1.wireOp",EDGE,"E67.MirrorCS");Q20=makeQuery(id+"F1.imprint","IMPRINT",FACE,{"disambiguationData":[TD([[makeQuery(id+"F1.imprint","IMPRINT",EDGE,{"derivedFrom":subQ2}),1.0]])]});}
            var Q21;
            {var subQ0=sQuery(id+"F1.wireOp",EDGE,"E65.MirrorCS");Q21=makeQuery(id+"F1.imprint","IMPRINT",FACE,{"disambiguationData":[TD([[makeQuery(id+"F1.imprint","IMPRINT",EDGE,{"derivedFrom":subQ0}),1.0]])]});}
            var Q22;
            {var subQ0=sQuery(id+"F1.wireOp",EDGE,"E61.MirrorCS");Q22=makeQuery(id+"F1.imprint","IMPRINT",FACE,{"disambiguationData":[TD([[makeQuery(id+"F1.imprint","IMPRINT",EDGE,{"derivedFrom":subQ0}),1.0]])]});}
            var Q23;
            {var subQ0=sQuery(id+"F1.wireOp",EDGE,"E57.MirrorCS");Q23=makeQuery(id+"F1.imprint","IMPRINT",FACE,{"disambiguationData":[TD([[makeQuery(id+"F1.imprint","IMPRINT",EDGE,{"derivedFrom":subQ0}),1.0]])]});}
            var Q24;
            {var subQ0=sQuery(id+"F1.wireOp",EDGE,"E50.MirrorCS");Q24=makeQuery(id+"F1.imprint","IMPRINT",FACE,{"disambiguationData":[TD([[makeQuery(id+"F1.imprint","IMPRINT",EDGE,{"derivedFrom":subQ0}),-1.0]])]});}
            var Q25;
            {var subQ0=sQuery(id+"F1.wireOp",EDGE,"E46.MirrorCS");Q25=makeQuery(id+"F1.imprint","IMPRINT",FACE,{"disambiguationData":[TD([[makeQuery(id+"F1.imprint","IMPRINT",EDGE,{"derivedFrom":subQ0}),-1.0]])]});}
            var Q26;
            {var subQ0=sQuery(id+"F1.wireOp",EDGE,"E51.MirrorCS");Q26=makeQuery(id+"F1.imprint","IMPRINT",FACE,{"disambiguationData":[TD([[makeQuery(id+"F1.imprint","IMPRINT",EDGE,{"derivedFrom":subQ0}),1.0]])]});}
            var Q27;
            {var subQ0=sQuery(id+"F1.wireOp",EDGE,"E75.MirrorCS");Q27=makeQuery(id+"F1.imprint","IMPRINT",FACE,{"disambiguationData":[TD([[makeQuery(id+"F1.imprint","IMPRINT",EDGE,{"derivedFrom":subQ0}),1.0]])]});}
            var Q28;
            {var subQ0=sQuery(id+"F1.wireOp",EDGE,"E72.MirrorCS");Q28=makeQuery(id+"F1.imprint","IMPRINT",FACE,{"disambiguationData":[TD([[makeQuery(id+"F1.imprint","IMPRINT",EDGE,{"derivedFrom":subQ0}),-1.0]])]});}
            var Q29;
            {var subQ0=sQuery(id+"F1.wireOp",EDGE,"E69.MirrorCS");Q29=makeQuery(id+"F1.imprint","IMPRINT",FACE,{"disambiguationData":[TD([[makeQuery(id+"F1.imprint","IMPRINT",EDGE,{"derivedFrom":subQ0}),1.0]])]});}
            var Q30;
            {var subQ0=sQuery(id+"F1.wireOp",EDGE,"E66.MirrorCS");Q30=makeQuery(id+"F1.imprint","IMPRINT",FACE,{"disambiguationData":[TD([[makeQuery(id+"F1.imprint","IMPRINT",EDGE,{"derivedFrom":subQ0}),-1.0]])]});}
            var Q31;
            {var subQ0=sQuery(id+"F1.wireOp",EDGE,"E64.MirrorCS");Q31=makeQuery(id+"F1.imprint","IMPRINT",FACE,{"disambiguationData":[TD([[makeQuery(id+"F1.imprint","IMPRINT",EDGE,{"derivedFrom":subQ0}),-1.0]])]});}
            var Q32;
            {var subQ0=sQuery(id+"F1.wireOp",EDGE,"E62.MirrorCS");Q32=makeQuery(id+"F1.imprint","IMPRINT",FACE,{"disambiguationData":[TD([[makeQuery(id+"F1.imprint","IMPRINT",EDGE,{"derivedFrom":subQ0}),-1.0]])]});}
            var Q33;
            {var subQ0=sQuery(id+"F1.wireOp",EDGE,"E60.MirrorCS");Q33=makeQuery(id+"F1.imprint","IMPRINT",FACE,{"disambiguationData":[TD([[makeQuery(id+"F1.imprint","IMPRINT",EDGE,{"derivedFrom":subQ0}),-1.0]])]});}
            var Q34;
            {var subQ0=sQuery(id+"F1.wireOp",EDGE,"E58.MirrorCS");Q34=makeQuery(id+"F1.imprint","IMPRINT",FACE,{"disambiguationData":[TD([[makeQuery(id+"F1.imprint","IMPRINT",EDGE,{"derivedFrom":subQ0}),-1.0]])]});}
            var Q35;
            {var subQ0=sQuery(id+"F1.wireOp",EDGE,"E56.MirrorCS");Q35=makeQuery(id+"F1.imprint","IMPRINT",FACE,{"disambiguationData":[TD([[makeQuery(id+"F1.imprint","IMPRINT",EDGE,{"derivedFrom":subQ0}),-1.0]])]});}
            var Q36;
            {var subQ0=sQuery(id+"F1.wireOp",EDGE,"E54.MirrorCS");Q36=makeQuery(id+"F1.imprint","IMPRINT",FACE,{"disambiguationData":[TD([[makeQuery(id+"F1.imprint","IMPRINT",EDGE,{"derivedFrom":subQ0}),-1.0]])]});}
            var Q37;
            {var subQ0=sQuery(id+"F1.wireOp",EDGE,"E52.MirrorCS");Q37=makeQuery(id+"F1.imprint","IMPRINT",FACE,{"disambiguationData":[TD([[makeQuery(id+"F1.imprint","IMPRINT",EDGE,{"derivedFrom":subQ0}),-1.0]])]});}
            extrude(context, id + "F6", {"entities" : qUnion([Q0, Q1, Q2, Q3, Q4, Q5, Q6, Q7, Q8, Q9, Q10, Q11, Q12, Q13, Q14, Q15, Q16, Q17, Q18, Q19, Q20, Q21, Q22, Q23, Q24, Q25, Q26, Q27, Q28, Q29, Q30, Q31, Q32, Q33, Q34, Q35, Q36, Q37]), "depth" : 3 * mm, "offsetDistance" : 25 * mm});
        }
        {
            var Q0;
            Q0=qCreatedBy(makeId("Right.planeOp"),FACE);
            var sketch = newSketch(context, id + "F7", { "sketchPlane" : qUnion([Q0])});
            skLineSegment(sketch, "E80.bottom", {"start": v(5, 29.85) * mm, "end": v(-5, 29.85) * mm});
            skLineSegment(sketch, "E80.top", {"start": v(5, -29.85) * mm, "end": v(-5, -29.85) * mm});
            skLineSegment(sketch, "E80.left", {"start": v(5, 29.85) * mm, "end": v(5, -29.85) * mm});
            skLineSegment(sketch, "E80.right", {"start": v(-5, 29.85) * mm, "end": v(-5, -29.85) * mm});
            skPoint(sketch, "E80.middle", {"position": v(0, 0) * mm});
            skLineSegment(sketch, "E81", {"start": v(-5, 29.58) * mm, "end": v(5, 29.58) * mm});
            skLineSegment(sketch, "E82.bottom", {"start": v(-5, 29.85) * mm, "end": v(-5.27, 29.85) * mm});
            skLineSegment(sketch, "E82.top", {"start": v(-5, -29.85) * mm, "end": v(-5.27, -29.85) * mm});
            skLineSegment(sketch, "E82.right", {"start": v(-5.27, 29.85) * mm, "end": v(-5.27, -29.85) * mm});
            skLineSegment(sketch, "E83.MirrorCS", {"start": v(5, 29.31) * mm, "end": v(-5, 29.31) * mm});
            skLineSegment(sketch, "E84.MirrorCS", {"start": v(5, 28.77) * mm, "end": v(-5, 28.77) * mm});
            skLineSegment(sketch, "E85.MirrorCS", {"start": v(-5, 29.04) * mm, "end": v(5, 29.04) * mm});
            skLineSegment(sketch, "E86.MirrorCS", {"start": v(-5, 28.5) * mm, "end": v(5, 28.5) * mm});
            skLineSegment(sketch, "E87.MirrorCS", {"start": v(5, 28.23) * mm, "end": v(-5, 28.23) * mm});
            skLineSegment(sketch, "E88.MirrorCS", {"start": v(-5, 27.96) * mm, "end": v(5, 27.96) * mm});
            skLineSegment(sketch, "E89.MirrorCS", {"start": v(5, 27.7) * mm, "end": v(-5, 27.7) * mm});
            skLineSegment(sketch, "E90.MirrorCS", {"start": v(-5, 27.42) * mm, "end": v(5, 27.42) * mm});
            skLineSegment(sketch, "E91.MirrorCS", {"start": v(5, 27.15) * mm, "end": v(-5, 27.15) * mm});
            skLineSegment(sketch, "E92.MirrorCS", {"start": v(-5, 26.88) * mm, "end": v(5, 26.88) * mm});
            skLineSegment(sketch, "E93.MirrorCS", {"start": v(5, 26.61) * mm, "end": v(-5, 26.61) * mm});
            skLineSegment(sketch, "E94.MirrorCS", {"start": v(-5, 26.34) * mm, "end": v(5, 26.34) * mm});
            skLineSegment(sketch, "E95.MirrorCS", {"start": v(5, 26.07) * mm, "end": v(-5, 26.07) * mm});
            skLineSegment(sketch, "E96.MirrorCS", {"start": v(-5, 25.8) * mm, "end": v(5, 25.8) * mm});
            skLineSegment(sketch, "E97.MirrorCS", {"start": v(5, 25.53) * mm, "end": v(-5, 25.53) * mm});
            skLineSegment(sketch, "E98.MirrorCS", {"start": v(-5, 25.26) * mm, "end": v(5, 25.26) * mm});
            skLineSegment(sketch, "E99.MirrorCS", {"start": v(5, 25) * mm, "end": v(-5, 25) * mm});
            skLineSegment(sketch, "E100.MirrorCS", {"start": v(-5, 24.72) * mm, "end": v(5, 24.72) * mm});
            skLineSegment(sketch, "E101.MirrorCS", {"start": v(5, 24.45) * mm, "end": v(-5, 24.45) * mm});
            skLineSegment(sketch, "E102.MirrorCS", {"start": v(-5, 24.18) * mm, "end": v(5, 24.18) * mm});
            skLineSegment(sketch, "E103.MirrorCS", {"start": v(5, 23.91) * mm, "end": v(-5, 23.91) * mm});
            skLineSegment(sketch, "E104.MirrorCS", {"start": v(-5, 23.64) * mm, "end": v(5, 23.64) * mm});
            skLineSegment(sketch, "E105.MirrorCS", {"start": v(5, 23.37) * mm, "end": v(-5, 23.37) * mm});
            skLineSegment(sketch, "E106.MirrorCS", {"start": v(-5, 23.1) * mm, "end": v(5, 23.1) * mm});
            skLineSegment(sketch, "E107.MirrorCS", {"start": v(5, 22.83) * mm, "end": v(-5, 22.83) * mm});
            skLineSegment(sketch, "E108.MirrorCS", {"start": v(-5, 22.56) * mm, "end": v(5, 22.56) * mm});
            skLineSegment(sketch, "E109.MirrorCS", {"start": v(5, 22.3) * mm, "end": v(-5, 22.3) * mm});
            skLineSegment(sketch, "E110.MirrorCS", {"start": v(-5, 22.02) * mm, "end": v(5, 22.02) * mm});
            skLineSegment(sketch, "E111.MirrorCS", {"start": v(5, 21.75) * mm, "end": v(-5, 21.75) * mm});
            skLineSegment(sketch, "E112.MirrorCS", {"start": v(-5, 21.48) * mm, "end": v(5, 21.48) * mm});
            skLineSegment(sketch, "E113.MirrorCS", {"start": v(5, 21.21) * mm, "end": v(-5, 21.21) * mm});
            skLineSegment(sketch, "E114.MirrorCS", {"start": v(-5, 20.94) * mm, "end": v(5, 20.94) * mm});
            skLineSegment(sketch, "E115.MirrorCS", {"start": v(5, 20.67) * mm, "end": v(-5, 20.67) * mm});
            skLineSegment(sketch, "E116.MirrorCS", {"start": v(-5, 20.4) * mm, "end": v(5, 20.4) * mm});
            skLineSegment(sketch, "E117.MirrorCS", {"start": v(5, 20.13) * mm, "end": v(-5, 20.13) * mm});
            skLineSegment(sketch, "E118.MirrorCS", {"start": v(-5, 19.86) * mm, "end": v(5, 19.86) * mm});
            skLineSegment(sketch, "E119.bottom", {"start": v(5, 29.85) * mm, "end": v(5.27, 29.85) * mm});
            skLineSegment(sketch, "E119.left", {"start": v(5, 29.85) * mm, "end": v(5, 19.86) * mm});
            skLineSegment(sketch, "E120", {"start": v(5.27, 29.85) * mm, "end": v(5.27, -29.85) * mm});
            skLineSegment(sketch, "E121", {"start": v(5.27, -29.85) * mm, "end": v(5, -29.85) * mm});
            skLineSegment(sketch, "E122.MirrorCS", {"start": v(5, 9.87) * mm, "end": v(-5, 9.87) * mm});
            skLineSegment(sketch, "E123.MirrorCS", {"start": v(-5, 10.14) * mm, "end": v(5, 10.14) * mm});
            skLineSegment(sketch, "E124.MirrorCS", {"start": v(5, 10.41) * mm, "end": v(-5, 10.41) * mm});
            skLineSegment(sketch, "E125.MirrorCS", {"start": v(-5, 10.68) * mm, "end": v(5, 10.68) * mm});
            skLineSegment(sketch, "E126.MirrorCS", {"start": v(5, 10.95) * mm, "end": v(-5, 10.95) * mm});
            skLineSegment(sketch, "E127.MirrorCS", {"start": v(-5, 11.22) * mm, "end": v(5, 11.22) * mm});
            skLineSegment(sketch, "E128.MirrorCS", {"start": v(5, 11.5) * mm, "end": v(-5, 11.5) * mm});
            skLineSegment(sketch, "E129.MirrorCS", {"start": v(-5, 11.76) * mm, "end": v(5, 11.76) * mm});
            skLineSegment(sketch, "E130.MirrorCS", {"start": v(5, 12.03) * mm, "end": v(-5, 12.03) * mm});
            skLineSegment(sketch, "E131.MirrorCS", {"start": v(-5, 12.3) * mm, "end": v(5, 12.3) * mm});
            skLineSegment(sketch, "E132.MirrorCS", {"start": v(5, 12.57) * mm, "end": v(-5, 12.57) * mm});
            skLineSegment(sketch, "E133.MirrorCS", {"start": v(-5, 12.84) * mm, "end": v(5, 12.84) * mm});
            skLineSegment(sketch, "E134.MirrorCS", {"start": v(5, 13.11) * mm, "end": v(-5, 13.11) * mm});
            skLineSegment(sketch, "E135.MirrorCS", {"start": v(-5, 13.38) * mm, "end": v(5, 13.38) * mm});
            skLineSegment(sketch, "E136.MirrorCS", {"start": v(5, 13.65) * mm, "end": v(-5, 13.65) * mm});
            skLineSegment(sketch, "E137.MirrorCS", {"start": v(-5, 13.92) * mm, "end": v(5, 13.92) * mm});
            skLineSegment(sketch, "E138.MirrorCS", {"start": v(5, 14.2) * mm, "end": v(-5, 14.2) * mm});
            skLineSegment(sketch, "E139.MirrorCS", {"start": v(-5, 14.46) * mm, "end": v(5, 14.46) * mm});
            skLineSegment(sketch, "E140.MirrorCS", {"start": v(5, 14.73) * mm, "end": v(-5, 14.73) * mm});
            skLineSegment(sketch, "E141.MirrorCS", {"start": v(-5, 15) * mm, "end": v(5, 15) * mm});
            skLineSegment(sketch, "E142.MirrorCS", {"start": v(-5, 15.54) * mm, "end": v(5, 15.54) * mm});
            skLineSegment(sketch, "E143.MirrorCS", {"start": v(5, 15.81) * mm, "end": v(-5, 15.81) * mm});
            skLineSegment(sketch, "E144.MirrorCS", {"start": v(-5, 16.08) * mm, "end": v(5, 16.08) * mm});
            skLineSegment(sketch, "E145.MirrorCS", {"start": v(5, 16.35) * mm, "end": v(-5, 16.35) * mm});
            skLineSegment(sketch, "E146.MirrorCS", {"start": v(-5, 16.62) * mm, "end": v(5, 16.62) * mm});
            skLineSegment(sketch, "E147.MirrorCS", {"start": v(5, 16.9) * mm, "end": v(-5, 16.9) * mm});
            skLineSegment(sketch, "E148.MirrorCS", {"start": v(-5, 17.16) * mm, "end": v(5, 17.16) * mm});
            skLineSegment(sketch, "E149.MirrorCS", {"start": v(5, 17.43) * mm, "end": v(-5, 17.43) * mm});
            skLineSegment(sketch, "E150.MirrorCS", {"start": v(-5, 17.7) * mm, "end": v(5, 17.7) * mm});
            skLineSegment(sketch, "E151.MirrorCS", {"start": v(5, 17.97) * mm, "end": v(-5, 17.97) * mm});
            skLineSegment(sketch, "E152.MirrorCS", {"start": v(-5, 18.24) * mm, "end": v(5, 18.24) * mm});
            skLineSegment(sketch, "E153.MirrorCS", {"start": v(5, 18.51) * mm, "end": v(-5, 18.51) * mm});
            skLineSegment(sketch, "E154.MirrorCS", {"start": v(-5, 18.78) * mm, "end": v(5, 18.78) * mm});
            skLineSegment(sketch, "E155.MirrorCS", {"start": v(5, 19.05) * mm, "end": v(-5, 19.05) * mm});
            skLineSegment(sketch, "E156.MirrorCS", {"start": v(-5, 19.32) * mm, "end": v(5, 19.32) * mm});
            skLineSegment(sketch, "E157.MirrorCS", {"start": v(5, 19.6) * mm, "end": v(-5, 19.6) * mm});
            skLineSegment(sketch, "E158.MirrorCS", {"start": v(5, 15.27) * mm, "end": v(-5, 15.27) * mm});
            skLineSegment(sketch, "E159.MirrorCS", {"start": v(-5, 9.6) * mm, "end": v(5, 9.6) * mm});
            skLineSegment(sketch, "E160.MirrorCS", {"start": v(5, 9.33) * mm, "end": v(-5, 9.33) * mm});
            skLineSegment(sketch, "E161.MirrorCS", {"start": v(-5, 9.06) * mm, "end": v(5, 9.06) * mm});
            skLineSegment(sketch, "E162.MirrorCS", {"start": v(5, 8.8) * mm, "end": v(-5, 8.8) * mm});
            skLineSegment(sketch, "E163.MirrorCS", {"start": v(-5, 8.52) * mm, "end": v(5, 8.52) * mm});
            skLineSegment(sketch, "E164.MirrorCS", {"start": v(5, 8.25) * mm, "end": v(-5, 8.25) * mm});
            skLineSegment(sketch, "E165.MirrorCS", {"start": v(-5, 7.98) * mm, "end": v(5, 7.98) * mm});
            skLineSegment(sketch, "E166.MirrorCS", {"start": v(5, 7.71) * mm, "end": v(-5, 7.71) * mm});
            skLineSegment(sketch, "E167.MirrorCS", {"start": v(-5, 7.44) * mm, "end": v(5, 7.44) * mm});
            skLineSegment(sketch, "E168.MirrorCS", {"start": v(5, 7.17) * mm, "end": v(-5, 7.17) * mm});
            skLineSegment(sketch, "E169.MirrorCS", {"start": v(-5, 6.9) * mm, "end": v(5, 6.9) * mm});
            skLineSegment(sketch, "E170.MirrorCS", {"start": v(5, 6.63) * mm, "end": v(-5, 6.63) * mm});
            skLineSegment(sketch, "E171.MirrorCS", {"start": v(-5, 6.36) * mm, "end": v(5, 6.36) * mm});
            skLineSegment(sketch, "E172.MirrorCS", {"start": v(5, 6.1) * mm, "end": v(-5, 6.1) * mm});
            skLineSegment(sketch, "E173.MirrorCS", {"start": v(-5, 5.82) * mm, "end": v(5, 5.82) * mm});
            skLineSegment(sketch, "E174.MirrorCS", {"start": v(5, 5.55) * mm, "end": v(-5, 5.55) * mm});
            skLineSegment(sketch, "E175.MirrorCS", {"start": v(-5, 5.28) * mm, "end": v(5, 5.28) * mm});
            skLineSegment(sketch, "E176.MirrorCS", {"start": v(5, 5.01) * mm, "end": v(-5, 5.01) * mm});
            skLineSegment(sketch, "E177.MirrorCS", {"start": v(-5, 4.74) * mm, "end": v(5, 4.74) * mm});
            skLineSegment(sketch, "E178.MirrorCS", {"start": v(5, 4.47) * mm, "end": v(-5, 4.47) * mm});
            skLineSegment(sketch, "E179.MirrorCS", {"start": v(-5, 4.2) * mm, "end": v(5, 4.2) * mm});
            skLineSegment(sketch, "E180.MirrorCS", {"start": v(5, 3.93) * mm, "end": v(-5, 3.93) * mm});
            skLineSegment(sketch, "E181.MirrorCS", {"start": v(-5, 3.66) * mm, "end": v(5, 3.66) * mm});
            skLineSegment(sketch, "E182.MirrorCS", {"start": v(5, 3.4) * mm, "end": v(-5, 3.4) * mm});
            skLineSegment(sketch, "E183.MirrorCS", {"start": v(-5, 3.12) * mm, "end": v(5, 3.12) * mm});
            skLineSegment(sketch, "E184.MirrorCS", {"start": v(5, 2.85) * mm, "end": v(-5, 2.85) * mm});
            skLineSegment(sketch, "E185.MirrorCS", {"start": v(-5, 2.58) * mm, "end": v(5, 2.58) * mm});
            skLineSegment(sketch, "E186.MirrorCS", {"start": v(5, 2.31) * mm, "end": v(-5, 2.31) * mm});
            skLineSegment(sketch, "E187.MirrorCS", {"start": v(-5, 2.04) * mm, "end": v(5, 2.04) * mm});
            skLineSegment(sketch, "E188.MirrorCS", {"start": v(5, 1.77) * mm, "end": v(-5, 1.77) * mm});
            skLineSegment(sketch, "E189.MirrorCS", {"start": v(-5, 1.5) * mm, "end": v(5, 1.5) * mm});
            skLineSegment(sketch, "E190.MirrorCS", {"start": v(5, 1.23) * mm, "end": v(-5, 1.23) * mm});
            skLineSegment(sketch, "E191.MirrorCS", {"start": v(-5, 0.96) * mm, "end": v(5, 0.96) * mm});
            skLineSegment(sketch, "E192.MirrorCS", {"start": v(5, 0.7) * mm, "end": v(-5, 0.7) * mm});
            skLineSegment(sketch, "E193.MirrorCS", {"start": v(-5, 0.42) * mm, "end": v(5, 0.42) * mm});
            skLineSegment(sketch, "E194.MirrorCS", {"start": v(5, 0.15) * mm, "end": v(-5, 0.15) * mm});
            skLineSegment(sketch, "E195.MirrorCS", {"start": v(-5, -0.12) * mm, "end": v(5, -0.12) * mm});
            skLineSegment(sketch, "E196.MirrorCS", {"start": v(5, -0.39) * mm, "end": v(-5, -0.39) * mm});
            skLineSegment(sketch, "E197.MirrorCS", {"start": v(-5, -0.66) * mm, "end": v(5, -0.66) * mm});
            skLineSegment(sketch, "E198.MirrorCS", {"start": v(5, -0.93) * mm, "end": v(-5, -0.93) * mm});
            skLineSegment(sketch, "E199.MirrorCS", {"start": v(-5, -1.2) * mm, "end": v(5, -1.2) * mm});
            skLineSegment(sketch, "E200.MirrorCS", {"start": v(5, -1.47) * mm, "end": v(-5, -1.47) * mm});
            skLineSegment(sketch, "E201.MirrorCS", {"start": v(-5, -1.74) * mm, "end": v(5, -1.74) * mm});
            skLineSegment(sketch, "E202.MirrorCS", {"start": v(5, -2) * mm, "end": v(-5, -2) * mm});
            skLineSegment(sketch, "E203.MirrorCS", {"start": v(-5, -2.28) * mm, "end": v(5, -2.28) * mm});
            skLineSegment(sketch, "E204.MirrorCS", {"start": v(5, -2.55) * mm, "end": v(-5, -2.55) * mm});
            skLineSegment(sketch, "E205.MirrorCS", {"start": v(-5, -2.82) * mm, "end": v(5, -2.82) * mm});
            skLineSegment(sketch, "E206.MirrorCS", {"start": v(5, -3.09) * mm, "end": v(-5, -3.09) * mm});
            skLineSegment(sketch, "E207.MirrorCS", {"start": v(-5, -3.36) * mm, "end": v(5, -3.36) * mm});
            skLineSegment(sketch, "E208.MirrorCS", {"start": v(5, -3.63) * mm, "end": v(-5, -3.63) * mm});
            skLineSegment(sketch, "E209.MirrorCS", {"start": v(-5, -3.9) * mm, "end": v(5, -3.9) * mm});
            skLineSegment(sketch, "E210.MirrorCS", {"start": v(5, -4.17) * mm, "end": v(-5, -4.17) * mm});
            skLineSegment(sketch, "E211.MirrorCS", {"start": v(-5, -4.44) * mm, "end": v(5, -4.44) * mm});
            skLineSegment(sketch, "E212.MirrorCS", {"start": v(5, -4.7) * mm, "end": v(-5, -4.7) * mm});
            skLineSegment(sketch, "E213.MirrorCS", {"start": v(-5, -4.98) * mm, "end": v(5, -4.98) * mm});
            skLineSegment(sketch, "E214.MirrorCS", {"start": v(5, -5.25) * mm, "end": v(-5, -5.25) * mm});
            skLineSegment(sketch, "E215.MirrorCS", {"start": v(-5, -5.52) * mm, "end": v(5, -5.52) * mm});
            skLineSegment(sketch, "E216.MirrorCS", {"start": v(5, -5.79) * mm, "end": v(-5, -5.79) * mm});
            skLineSegment(sketch, "E217.MirrorCS", {"start": v(-5, -6.06) * mm, "end": v(5, -6.06) * mm});
            skLineSegment(sketch, "E218.MirrorCS", {"start": v(5, -6.33) * mm, "end": v(-5, -6.33) * mm});
            skLineSegment(sketch, "E219.MirrorCS", {"start": v(-5, -6.6) * mm, "end": v(5, -6.6) * mm});
            skLineSegment(sketch, "E220.MirrorCS", {"start": v(5, -6.87) * mm, "end": v(-5, -6.87) * mm});
            skLineSegment(sketch, "E221.MirrorCS", {"start": v(-5, -7.14) * mm, "end": v(5, -7.14) * mm});
            skLineSegment(sketch, "E222.MirrorCS", {"start": v(5, -7.4) * mm, "end": v(-5, -7.4) * mm});
            skLineSegment(sketch, "E223.MirrorCS", {"start": v(-5, -7.68) * mm, "end": v(5, -7.68) * mm});
            skLineSegment(sketch, "E224.MirrorCS", {"start": v(5, -7.95) * mm, "end": v(-5, -7.95) * mm});
            skLineSegment(sketch, "E225.MirrorCS", {"start": v(-5, -8.22) * mm, "end": v(5, -8.22) * mm});
            skLineSegment(sketch, "E226.MirrorCS", {"start": v(5, -8.49) * mm, "end": v(-5, -8.49) * mm});
            skLineSegment(sketch, "E227.MirrorCS", {"start": v(-5, -8.76) * mm, "end": v(5, -8.76) * mm});
            skLineSegment(sketch, "E228.MirrorCS", {"start": v(5, -9.03) * mm, "end": v(-5, -9.03) * mm});
            skLineSegment(sketch, "E229.MirrorCS", {"start": v(-5, -9.3) * mm, "end": v(5, -9.3) * mm});
            skLineSegment(sketch, "E230.MirrorCS", {"start": v(5, -9.57) * mm, "end": v(-5, -9.57) * mm});
            skLineSegment(sketch, "E231.MirrorCS", {"start": v(-5, -9.84) * mm, "end": v(5, -9.84) * mm});
            skLineSegment(sketch, "E232.MirrorCS", {"start": v(5, -10.1) * mm, "end": v(-5, -10.1) * mm});
            skLineSegment(sketch, "E233.MirrorCS", {"start": v(-5, -10.38) * mm, "end": v(5, -10.38) * mm});
            skLineSegment(sketch, "E234.MirrorCS", {"start": v(5, -10.65) * mm, "end": v(-5, -10.65) * mm});
            skLineSegment(sketch, "E235.MirrorCS", {"start": v(-5, -10.92) * mm, "end": v(5, -10.92) * mm});
            skLineSegment(sketch, "E236.MirrorCS", {"start": v(5, -11.19) * mm, "end": v(-5, -11.19) * mm});
            skLineSegment(sketch, "E237.MirrorCS", {"start": v(-5, -11.46) * mm, "end": v(5, -11.46) * mm});
            skLineSegment(sketch, "E238.MirrorCS", {"start": v(5, -11.73) * mm, "end": v(-5, -11.73) * mm});
            skLineSegment(sketch, "E239.MirrorCS", {"start": v(-5, -12) * mm, "end": v(5, -12) * mm});
            skLineSegment(sketch, "E240.MirrorCS", {"start": v(5, -12.27) * mm, "end": v(-5, -12.27) * mm});
            skLineSegment(sketch, "E241.MirrorCS", {"start": v(-5, -12.54) * mm, "end": v(5, -12.54) * mm});
            skLineSegment(sketch, "E242.MirrorCS", {"start": v(5, -12.8) * mm, "end": v(-5, -12.8) * mm});
            skLineSegment(sketch, "E243.MirrorCS", {"start": v(-5, -13.08) * mm, "end": v(5, -13.08) * mm});
            skLineSegment(sketch, "E244.MirrorCS", {"start": v(5, -13.35) * mm, "end": v(-5, -13.35) * mm});
            skLineSegment(sketch, "E245.MirrorCS", {"start": v(-5, -13.62) * mm, "end": v(5, -13.62) * mm});
            skLineSegment(sketch, "E246.MirrorCS", {"start": v(5, -13.89) * mm, "end": v(-5, -13.89) * mm});
            skLineSegment(sketch, "E247.MirrorCS", {"start": v(-5, -14.16) * mm, "end": v(5, -14.16) * mm});
            skLineSegment(sketch, "E248.MirrorCS", {"start": v(5, -14.43) * mm, "end": v(-5, -14.43) * mm});
            skLineSegment(sketch, "E249.MirrorCS", {"start": v(-5, -14.7) * mm, "end": v(5, -14.7) * mm});
            skLineSegment(sketch, "E250.MirrorCS", {"start": v(5, -14.97) * mm, "end": v(-5, -14.97) * mm});
            skLineSegment(sketch, "E251.MirrorCS", {"start": v(-5, -15.24) * mm, "end": v(5, -15.24) * mm});
            skLineSegment(sketch, "E252.MirrorCS", {"start": v(5, -15.5) * mm, "end": v(-5, -15.5) * mm});
            skLineSegment(sketch, "E253.MirrorCS", {"start": v(-5, -15.78) * mm, "end": v(5, -15.78) * mm});
            skLineSegment(sketch, "E254.MirrorCS", {"start": v(5, -16.05) * mm, "end": v(-5, -16.05) * mm});
            skLineSegment(sketch, "E255.MirrorCS", {"start": v(-5, -16.32) * mm, "end": v(5, -16.32) * mm});
            skLineSegment(sketch, "E256.MirrorCS", {"start": v(5, -16.59) * mm, "end": v(-5, -16.59) * mm});
            skLineSegment(sketch, "E257.MirrorCS", {"start": v(-5, -16.86) * mm, "end": v(5, -16.86) * mm});
            skLineSegment(sketch, "E258.MirrorCS", {"start": v(5, -17.13) * mm, "end": v(-5, -17.13) * mm});
            skLineSegment(sketch, "E259.MirrorCS", {"start": v(-5, -29.28) * mm, "end": v(5, -29.28) * mm});
            skLineSegment(sketch, "E260.MirrorCS", {"start": v(5, -29) * mm, "end": v(-5, -29) * mm});
            skLineSegment(sketch, "E261.MirrorCS", {"start": v(-5, -28.74) * mm, "end": v(5, -28.74) * mm});
            skLineSegment(sketch, "E262.MirrorCS", {"start": v(5, -28.47) * mm, "end": v(-5, -28.47) * mm});
            skLineSegment(sketch, "E263.MirrorCS", {"start": v(-5, -28.2) * mm, "end": v(5, -28.2) * mm});
            skLineSegment(sketch, "E264.MirrorCS", {"start": v(5, -27.93) * mm, "end": v(-5, -27.93) * mm});
            skLineSegment(sketch, "E265.MirrorCS", {"start": v(-5, -27.66) * mm, "end": v(5, -27.66) * mm});
            skLineSegment(sketch, "E266.MirrorCS", {"start": v(5, -27.39) * mm, "end": v(-5, -27.39) * mm});
            skLineSegment(sketch, "E267.MirrorCS", {"start": v(-5, -27.12) * mm, "end": v(5, -27.12) * mm});
            skLineSegment(sketch, "E268.MirrorCS", {"start": v(5, -26.85) * mm, "end": v(-5, -26.85) * mm});
            skLineSegment(sketch, "E269.MirrorCS", {"start": v(-5, -26.58) * mm, "end": v(5, -26.58) * mm});
            skLineSegment(sketch, "E270.MirrorCS", {"start": v(5, -26.3) * mm, "end": v(-5, -26.3) * mm});
            skLineSegment(sketch, "E271.MirrorCS", {"start": v(-5, -26.04) * mm, "end": v(5, -26.04) * mm});
            skLineSegment(sketch, "E272.MirrorCS", {"start": v(5, -25.77) * mm, "end": v(-5, -25.77) * mm});
            skLineSegment(sketch, "E273.MirrorCS", {"start": v(-5, -25.5) * mm, "end": v(5, -25.5) * mm});
            skLineSegment(sketch, "E274.MirrorCS", {"start": v(5, -25.23) * mm, "end": v(-5, -25.23) * mm});
            skLineSegment(sketch, "E275.MirrorCS", {"start": v(-5, -24.96) * mm, "end": v(5, -24.96) * mm});
            skLineSegment(sketch, "E276.MirrorCS", {"start": v(5, -24.69) * mm, "end": v(-5, -24.69) * mm});
            skLineSegment(sketch, "E277.MirrorCS", {"start": v(-5, -24.42) * mm, "end": v(5, -24.42) * mm});
            skLineSegment(sketch, "E278.MirrorCS", {"start": v(5, -24.15) * mm, "end": v(-5, -24.15) * mm});
            skLineSegment(sketch, "E279.MirrorCS", {"start": v(-5, -23.88) * mm, "end": v(5, -23.88) * mm});
            skLineSegment(sketch, "E280.MirrorCS", {"start": v(5, -23.6) * mm, "end": v(-5, -23.6) * mm});
            skLineSegment(sketch, "E281.MirrorCS", {"start": v(-5, -23.34) * mm, "end": v(5, -23.34) * mm});
            skLineSegment(sketch, "E282.MirrorCS", {"start": v(5, -23.07) * mm, "end": v(-5, -23.07) * mm});
            skLineSegment(sketch, "E283.MirrorCS", {"start": v(-5, -22.8) * mm, "end": v(5, -22.8) * mm});
            skLineSegment(sketch, "E284.MirrorCS", {"start": v(5, -22.53) * mm, "end": v(-5, -22.53) * mm});
            skLineSegment(sketch, "E285.MirrorCS", {"start": v(-5, -22.26) * mm, "end": v(5, -22.26) * mm});
            skLineSegment(sketch, "E286.MirrorCS", {"start": v(5, -21.99) * mm, "end": v(-5, -21.99) * mm});
            skLineSegment(sketch, "E287.MirrorCS", {"start": v(-5, -21.72) * mm, "end": v(5, -21.72) * mm});
            skLineSegment(sketch, "E288.MirrorCS", {"start": v(5, -21.45) * mm, "end": v(-5, -21.45) * mm});
            skLineSegment(sketch, "E289.MirrorCS", {"start": v(-5, -21.18) * mm, "end": v(5, -21.18) * mm});
            skLineSegment(sketch, "E290.MirrorCS", {"start": v(5, -20.9) * mm, "end": v(-5, -20.9) * mm});
            skLineSegment(sketch, "E291.MirrorCS", {"start": v(-5, -20.64) * mm, "end": v(5, -20.64) * mm});
            skLineSegment(sketch, "E292.MirrorCS", {"start": v(5, -20.37) * mm, "end": v(-5, -20.37) * mm});
            skLineSegment(sketch, "E293.MirrorCS", {"start": v(-5, -20.1) * mm, "end": v(5, -20.1) * mm});
            skLineSegment(sketch, "E294.MirrorCS", {"start": v(5, -19.83) * mm, "end": v(-5, -19.83) * mm});
            skLineSegment(sketch, "E295.MirrorCS", {"start": v(-5, -19.56) * mm, "end": v(5, -19.56) * mm});
            skLineSegment(sketch, "E296.MirrorCS", {"start": v(5, -19.29) * mm, "end": v(-5, -19.29) * mm});
            skLineSegment(sketch, "E297.MirrorCS", {"start": v(-5, -19.02) * mm, "end": v(5, -19.02) * mm});
            skLineSegment(sketch, "E298.MirrorCS", {"start": v(5, -18.75) * mm, "end": v(-5, -18.75) * mm});
            skLineSegment(sketch, "E299.MirrorCS", {"start": v(-5, -18.48) * mm, "end": v(5, -18.48) * mm});
            skLineSegment(sketch, "E300.MirrorCS", {"start": v(5, -18.2) * mm, "end": v(-5, -18.2) * mm});
            skLineSegment(sketch, "E301.MirrorCS", {"start": v(-5, -17.94) * mm, "end": v(5, -17.94) * mm});
            skLineSegment(sketch, "E302.MirrorCS", {"start": v(5, -17.67) * mm, "end": v(-5, -17.67) * mm});
            skLineSegment(sketch, "E303.MirrorCS", {"start": v(-5, -17.4) * mm, "end": v(5, -17.4) * mm});
            skLineSegment(sketch, "E304.MirrorCS", {"start": v(5, -29.55) * mm, "end": v(-5, -29.55) * mm});
            skSolve(sketch);
        }
        {
            var Q0;
            {var subQ0=sQuery(id+"F7.wireOp",EDGE,"E80.bottom");Q0=makeQuery(id+"F7.imprint","IMPRINT",FACE,{"disambiguationData":[TD([[makeQuery(id+"F7.imprint","IMPRINT",EDGE,{"derivedFrom":subQ0}),1.0]])]});}
            var Q1;
            {var subQ0=sQuery(id+"F7.wireOp",EDGE,"E83.MirrorCS");Q1=makeQuery(id+"F7.imprint","IMPRINT",FACE,{"disambiguationData":[TD([[makeQuery(id+"F7.imprint","IMPRINT",EDGE,{"derivedFrom":subQ0}),1.0]])]});}
            var Q2;
            {var subQ0=sQuery(id+"F7.wireOp",EDGE,"E84.MirrorCS");Q2=makeQuery(id+"F7.imprint","IMPRINT",FACE,{"disambiguationData":[TD([[makeQuery(id+"F7.imprint","IMPRINT",EDGE,{"derivedFrom":subQ0}),1.0]])]});}
            var Q3;
            {var subQ0=sQuery(id+"F7.wireOp",EDGE,"E87.MirrorCS");Q3=makeQuery(id+"F7.imprint","IMPRINT",FACE,{"disambiguationData":[TD([[makeQuery(id+"F7.imprint","IMPRINT",EDGE,{"derivedFrom":subQ0}),1.0]])]});}
            var Q4;
            {var subQ215=sQuery(id+"F7.wireOp",EDGE,"E119.bottom");Q4=makeQuery(id+"F7.imprint","IMPRINT",FACE,{"disambiguationData":[TD([[makeQuery(id+"F7.imprint","IMPRINT",EDGE,{"derivedFrom":subQ215}),-1.0]])]});}
            var Q5;
            {var subQ0=sQuery(id+"F7.wireOp",EDGE,"E89.MirrorCS");Q5=makeQuery(id+"F7.imprint","IMPRINT",FACE,{"disambiguationData":[TD([[makeQuery(id+"F7.imprint","IMPRINT",EDGE,{"derivedFrom":subQ0}),1.0]])]});}
            var Q6;
            {var subQ0=sQuery(id+"F7.wireOp",EDGE,"E91.MirrorCS");Q6=makeQuery(id+"F7.imprint","IMPRINT",FACE,{"disambiguationData":[TD([[makeQuery(id+"F7.imprint","IMPRINT",EDGE,{"derivedFrom":subQ0}),1.0]])]});}
            var Q7;
            {var subQ0=sQuery(id+"F7.wireOp",EDGE,"E93.MirrorCS");Q7=makeQuery(id+"F7.imprint","IMPRINT",FACE,{"disambiguationData":[TD([[makeQuery(id+"F7.imprint","IMPRINT",EDGE,{"derivedFrom":subQ0}),1.0]])]});}
            var Q8;
            {var subQ0=sQuery(id+"F7.wireOp",EDGE,"E95.MirrorCS");Q8=makeQuery(id+"F7.imprint","IMPRINT",FACE,{"disambiguationData":[TD([[makeQuery(id+"F7.imprint","IMPRINT",EDGE,{"derivedFrom":subQ0}),1.0]])]});}
            var Q9;
            {var subQ0=sQuery(id+"F7.wireOp",EDGE,"E97.MirrorCS");Q9=makeQuery(id+"F7.imprint","IMPRINT",FACE,{"disambiguationData":[TD([[makeQuery(id+"F7.imprint","IMPRINT",EDGE,{"derivedFrom":subQ0}),1.0]])]});}
            var Q10;
            {var subQ0=sQuery(id+"F7.wireOp",EDGE,"E99.MirrorCS");Q10=makeQuery(id+"F7.imprint","IMPRINT",FACE,{"disambiguationData":[TD([[makeQuery(id+"F7.imprint","IMPRINT",EDGE,{"derivedFrom":subQ0}),1.0]])]});}
            var Q11;
            {var subQ0=sQuery(id+"F7.wireOp",EDGE,"E101.MirrorCS");Q11=makeQuery(id+"F7.imprint","IMPRINT",FACE,{"disambiguationData":[TD([[makeQuery(id+"F7.imprint","IMPRINT",EDGE,{"derivedFrom":subQ0}),1.0]])]});}
            var Q12;
            {var subQ0=sQuery(id+"F7.wireOp",EDGE,"E105.MirrorCS");Q12=makeQuery(id+"F7.imprint","IMPRINT",FACE,{"disambiguationData":[TD([[makeQuery(id+"F7.imprint","IMPRINT",EDGE,{"derivedFrom":subQ0}),1.0]])]});}
            var Q13;
            {var subQ0=sQuery(id+"F7.wireOp",EDGE,"E107.MirrorCS");Q13=makeQuery(id+"F7.imprint","IMPRINT",FACE,{"disambiguationData":[TD([[makeQuery(id+"F7.imprint","IMPRINT",EDGE,{"derivedFrom":subQ0}),1.0]])]});}
            var Q14;
            {var subQ0=sQuery(id+"F7.wireOp",EDGE,"E109.MirrorCS");Q14=makeQuery(id+"F7.imprint","IMPRINT",FACE,{"disambiguationData":[TD([[makeQuery(id+"F7.imprint","IMPRINT",EDGE,{"derivedFrom":subQ0}),1.0]])]});}
            var Q15;
            {var subQ0=sQuery(id+"F7.wireOp",EDGE,"E111.MirrorCS");Q15=makeQuery(id+"F7.imprint","IMPRINT",FACE,{"disambiguationData":[TD([[makeQuery(id+"F7.imprint","IMPRINT",EDGE,{"derivedFrom":subQ0}),1.0]])]});}
            var Q16;
            {var subQ0=sQuery(id+"F7.wireOp",EDGE,"E113.MirrorCS");Q16=makeQuery(id+"F7.imprint","IMPRINT",FACE,{"disambiguationData":[TD([[makeQuery(id+"F7.imprint","IMPRINT",EDGE,{"derivedFrom":subQ0}),1.0]])]});}
            var Q17;
            {var subQ0=sQuery(id+"F7.wireOp",EDGE,"E115.MirrorCS");Q17=makeQuery(id+"F7.imprint","IMPRINT",FACE,{"disambiguationData":[TD([[makeQuery(id+"F7.imprint","IMPRINT",EDGE,{"derivedFrom":subQ0}),1.0]])]});}
            var Q18;
            {var subQ0=sQuery(id+"F7.wireOp",EDGE,"E117.MirrorCS");Q18=makeQuery(id+"F7.imprint","IMPRINT",FACE,{"disambiguationData":[TD([[makeQuery(id+"F7.imprint","IMPRINT",EDGE,{"derivedFrom":subQ0}),1.0]])]});}
            var Q19;
            {var subQ0=sQuery(id+"F7.wireOp",EDGE,"E156.MirrorCS");Q19=makeQuery(id+"F7.imprint","IMPRINT",FACE,{"disambiguationData":[TD([[makeQuery(id+"F7.imprint","IMPRINT",EDGE,{"derivedFrom":subQ0}),1.0]])]});}
            var Q20;
            {var subQ0=sQuery(id+"F7.wireOp",EDGE,"E154.MirrorCS");Q20=makeQuery(id+"F7.imprint","IMPRINT",FACE,{"disambiguationData":[TD([[makeQuery(id+"F7.imprint","IMPRINT",EDGE,{"derivedFrom":subQ0}),1.0]])]});}
            var Q21;
            {var subQ0=sQuery(id+"F7.wireOp",EDGE,"E152.MirrorCS");Q21=makeQuery(id+"F7.imprint","IMPRINT",FACE,{"disambiguationData":[TD([[makeQuery(id+"F7.imprint","IMPRINT",EDGE,{"derivedFrom":subQ0}),1.0]])]});}
            var Q22;
            {var subQ0=sQuery(id+"F7.wireOp",EDGE,"E150.MirrorCS");Q22=makeQuery(id+"F7.imprint","IMPRINT",FACE,{"disambiguationData":[TD([[makeQuery(id+"F7.imprint","IMPRINT",EDGE,{"derivedFrom":subQ0}),1.0]])]});}
            var Q23;
            {var subQ0=sQuery(id+"F7.wireOp",EDGE,"E148.MirrorCS");Q23=makeQuery(id+"F7.imprint","IMPRINT",FACE,{"disambiguationData":[TD([[makeQuery(id+"F7.imprint","IMPRINT",EDGE,{"derivedFrom":subQ0}),1.0]])]});}
            var Q24;
            {var subQ0=sQuery(id+"F7.wireOp",EDGE,"E146.MirrorCS");Q24=makeQuery(id+"F7.imprint","IMPRINT",FACE,{"disambiguationData":[TD([[makeQuery(id+"F7.imprint","IMPRINT",EDGE,{"derivedFrom":subQ0}),1.0]])]});}
            var Q25;
            {var subQ0=sQuery(id+"F7.wireOp",EDGE,"E144.MirrorCS");Q25=makeQuery(id+"F7.imprint","IMPRINT",FACE,{"disambiguationData":[TD([[makeQuery(id+"F7.imprint","IMPRINT",EDGE,{"derivedFrom":subQ0}),1.0]])]});}
            var Q26;
            {var subQ0=sQuery(id+"F7.wireOp",EDGE,"E142.MirrorCS");Q26=makeQuery(id+"F7.imprint","IMPRINT",FACE,{"disambiguationData":[TD([[makeQuery(id+"F7.imprint","IMPRINT",EDGE,{"derivedFrom":subQ0}),1.0]])]});}
            var Q27;
            {var subQ0=sQuery(id+"F7.wireOp",EDGE,"E141.MirrorCS");Q27=makeQuery(id+"F7.imprint","IMPRINT",FACE,{"disambiguationData":[TD([[makeQuery(id+"F7.imprint","IMPRINT",EDGE,{"derivedFrom":subQ0}),1.0]])]});}
            var Q28;
            {var subQ0=sQuery(id+"F7.wireOp",EDGE,"E139.MirrorCS");Q28=makeQuery(id+"F7.imprint","IMPRINT",FACE,{"disambiguationData":[TD([[makeQuery(id+"F7.imprint","IMPRINT",EDGE,{"derivedFrom":subQ0}),1.0]])]});}
            var Q29;
            {var subQ0=sQuery(id+"F7.wireOp",EDGE,"E137.MirrorCS");Q29=makeQuery(id+"F7.imprint","IMPRINT",FACE,{"disambiguationData":[TD([[makeQuery(id+"F7.imprint","IMPRINT",EDGE,{"derivedFrom":subQ0}),1.0]])]});}
            var Q30;
            {var subQ0=sQuery(id+"F7.wireOp",EDGE,"E135.MirrorCS");Q30=makeQuery(id+"F7.imprint","IMPRINT",FACE,{"disambiguationData":[TD([[makeQuery(id+"F7.imprint","IMPRINT",EDGE,{"derivedFrom":subQ0}),1.0]])]});}
            var Q31;
            {var subQ0=sQuery(id+"F7.wireOp",EDGE,"E103.MirrorCS");Q31=makeQuery(id+"F7.imprint","IMPRINT",FACE,{"disambiguationData":[TD([[makeQuery(id+"F7.imprint","IMPRINT",EDGE,{"derivedFrom":subQ0}),1.0]])]});}
            var Q32;
            {var subQ0=sQuery(id+"F7.wireOp",EDGE,"E133.MirrorCS");Q32=makeQuery(id+"F7.imprint","IMPRINT",FACE,{"disambiguationData":[TD([[makeQuery(id+"F7.imprint","IMPRINT",EDGE,{"derivedFrom":subQ0}),1.0]])]});}
            var Q33;
            {var subQ0=sQuery(id+"F7.wireOp",EDGE,"E131.MirrorCS");Q33=makeQuery(id+"F7.imprint","IMPRINT",FACE,{"disambiguationData":[TD([[makeQuery(id+"F7.imprint","IMPRINT",EDGE,{"derivedFrom":subQ0}),1.0]])]});}
            var Q34;
            {var subQ0=sQuery(id+"F7.wireOp",EDGE,"E129.MirrorCS");Q34=makeQuery(id+"F7.imprint","IMPRINT",FACE,{"disambiguationData":[TD([[makeQuery(id+"F7.imprint","IMPRINT",EDGE,{"derivedFrom":subQ0}),1.0]])]});}
            var Q35;
            {var subQ0=sQuery(id+"F7.wireOp",EDGE,"E127.MirrorCS");Q35=makeQuery(id+"F7.imprint","IMPRINT",FACE,{"disambiguationData":[TD([[makeQuery(id+"F7.imprint","IMPRINT",EDGE,{"derivedFrom":subQ0}),1.0]])]});}
            var Q36;
            {var subQ0=sQuery(id+"F7.wireOp",EDGE,"E125.MirrorCS");Q36=makeQuery(id+"F7.imprint","IMPRINT",FACE,{"disambiguationData":[TD([[makeQuery(id+"F7.imprint","IMPRINT",EDGE,{"derivedFrom":subQ0}),1.0]])]});}
            var Q37;
            {var subQ0=sQuery(id+"F7.wireOp",EDGE,"E123.MirrorCS");Q37=makeQuery(id+"F7.imprint","IMPRINT",FACE,{"disambiguationData":[TD([[makeQuery(id+"F7.imprint","IMPRINT",EDGE,{"derivedFrom":subQ0}),1.0]])]});}
            var Q38;
            {var subQ0=sQuery(id+"F7.wireOp",EDGE,"E122.MirrorCS");Q38=makeQuery(id+"F7.imprint","IMPRINT",FACE,{"disambiguationData":[TD([[makeQuery(id+"F7.imprint","IMPRINT",EDGE,{"derivedFrom":subQ0}),1.0]])]});}
            var Q39;
            {var subQ0=sQuery(id+"F7.wireOp",EDGE,"E160.MirrorCS");Q39=makeQuery(id+"F7.imprint","IMPRINT",FACE,{"disambiguationData":[TD([[makeQuery(id+"F7.imprint","IMPRINT",EDGE,{"derivedFrom":subQ0}),1.0]])]});}
            var Q40;
            {var subQ0=sQuery(id+"F7.wireOp",EDGE,"E162.MirrorCS");Q40=makeQuery(id+"F7.imprint","IMPRINT",FACE,{"disambiguationData":[TD([[makeQuery(id+"F7.imprint","IMPRINT",EDGE,{"derivedFrom":subQ0}),1.0]])]});}
            var Q41;
            {var subQ0=sQuery(id+"F7.wireOp",EDGE,"E164.MirrorCS");Q41=makeQuery(id+"F7.imprint","IMPRINT",FACE,{"disambiguationData":[TD([[makeQuery(id+"F7.imprint","IMPRINT",EDGE,{"derivedFrom":subQ0}),1.0]])]});}
            var Q42;
            {var subQ0=sQuery(id+"F7.wireOp",EDGE,"E166.MirrorCS");Q42=makeQuery(id+"F7.imprint","IMPRINT",FACE,{"disambiguationData":[TD([[makeQuery(id+"F7.imprint","IMPRINT",EDGE,{"derivedFrom":subQ0}),1.0]])]});}
            var Q43;
            {var subQ0=sQuery(id+"F7.wireOp",EDGE,"E178.MirrorCS");Q43=makeQuery(id+"F7.imprint","IMPRINT",FACE,{"disambiguationData":[TD([[makeQuery(id+"F7.imprint","IMPRINT",EDGE,{"derivedFrom":subQ0}),1.0]])]});}
            var Q44;
            {var subQ0=sQuery(id+"F7.wireOp",EDGE,"E180.MirrorCS");Q44=makeQuery(id+"F7.imprint","IMPRINT",FACE,{"disambiguationData":[TD([[makeQuery(id+"F7.imprint","IMPRINT",EDGE,{"derivedFrom":subQ0}),1.0]])]});}
            var Q45;
            {var subQ0=sQuery(id+"F7.wireOp",EDGE,"E168.MirrorCS");Q45=makeQuery(id+"F7.imprint","IMPRINT",FACE,{"disambiguationData":[TD([[makeQuery(id+"F7.imprint","IMPRINT",EDGE,{"derivedFrom":subQ0}),1.0]])]});}
            var Q46;
            {var subQ0=sQuery(id+"F7.wireOp",EDGE,"E172.MirrorCS");Q46=makeQuery(id+"F7.imprint","IMPRINT",FACE,{"disambiguationData":[TD([[makeQuery(id+"F7.imprint","IMPRINT",EDGE,{"derivedFrom":subQ0}),1.0]])]});}
            var Q47;
            {var subQ0=sQuery(id+"F7.wireOp",EDGE,"E174.MirrorCS");Q47=makeQuery(id+"F7.imprint","IMPRINT",FACE,{"disambiguationData":[TD([[makeQuery(id+"F7.imprint","IMPRINT",EDGE,{"derivedFrom":subQ0}),1.0]])]});}
            var Q48;
            {var subQ0=sQuery(id+"F7.wireOp",EDGE,"E176.MirrorCS");Q48=makeQuery(id+"F7.imprint","IMPRINT",FACE,{"disambiguationData":[TD([[makeQuery(id+"F7.imprint","IMPRINT",EDGE,{"derivedFrom":subQ0}),1.0]])]});}
            var Q49;
            {var subQ0=sQuery(id+"F7.wireOp",EDGE,"E170.MirrorCS");Q49=makeQuery(id+"F7.imprint","IMPRINT",FACE,{"disambiguationData":[TD([[makeQuery(id+"F7.imprint","IMPRINT",EDGE,{"derivedFrom":subQ0}),1.0]])]});}
            var Q50;
            {var subQ0=sQuery(id+"F7.wireOp",EDGE,"E184.MirrorCS");Q50=makeQuery(id+"F7.imprint","IMPRINT",FACE,{"disambiguationData":[TD([[makeQuery(id+"F7.imprint","IMPRINT",EDGE,{"derivedFrom":subQ0}),1.0]])]});}
            var Q51;
            {var subQ0=sQuery(id+"F7.wireOp",EDGE,"E186.MirrorCS");Q51=makeQuery(id+"F7.imprint","IMPRINT",FACE,{"disambiguationData":[TD([[makeQuery(id+"F7.imprint","IMPRINT",EDGE,{"derivedFrom":subQ0}),1.0]])]});}
            var Q52;
            {var subQ0=sQuery(id+"F7.wireOp",EDGE,"E188.MirrorCS");Q52=makeQuery(id+"F7.imprint","IMPRINT",FACE,{"disambiguationData":[TD([[makeQuery(id+"F7.imprint","IMPRINT",EDGE,{"derivedFrom":subQ0}),1.0]])]});}
            var Q53;
            {var subQ0=sQuery(id+"F7.wireOp",EDGE,"E190.MirrorCS");Q53=makeQuery(id+"F7.imprint","IMPRINT",FACE,{"disambiguationData":[TD([[makeQuery(id+"F7.imprint","IMPRINT",EDGE,{"derivedFrom":subQ0}),1.0]])]});}
            var Q54;
            {var subQ0=sQuery(id+"F7.wireOp",EDGE,"E192.MirrorCS");Q54=makeQuery(id+"F7.imprint","IMPRINT",FACE,{"disambiguationData":[TD([[makeQuery(id+"F7.imprint","IMPRINT",EDGE,{"derivedFrom":subQ0}),1.0]])]});}
            var Q55;
            {var subQ0=sQuery(id+"F7.wireOp",EDGE,"E182.MirrorCS");Q55=makeQuery(id+"F7.imprint","IMPRINT",FACE,{"disambiguationData":[TD([[makeQuery(id+"F7.imprint","IMPRINT",EDGE,{"derivedFrom":subQ0}),1.0]])]});}
            var Q56;
            {var subQ0=sQuery(id+"F7.wireOp",EDGE,"E194.MirrorCS");Q56=makeQuery(id+"F7.imprint","IMPRINT",FACE,{"disambiguationData":[TD([[makeQuery(id+"F7.imprint","IMPRINT",EDGE,{"derivedFrom":subQ0}),1.0]])]});}
            var Q57;
            {var subQ0=sQuery(id+"F7.wireOp",EDGE,"E196.MirrorCS");Q57=makeQuery(id+"F7.imprint","IMPRINT",FACE,{"disambiguationData":[TD([[makeQuery(id+"F7.imprint","IMPRINT",EDGE,{"derivedFrom":subQ0}),1.0]])]});}
            var Q58;
            {var subQ0=sQuery(id+"F7.wireOp",EDGE,"E198.MirrorCS");Q58=makeQuery(id+"F7.imprint","IMPRINT",FACE,{"disambiguationData":[TD([[makeQuery(id+"F7.imprint","IMPRINT",EDGE,{"derivedFrom":subQ0}),1.0]])]});}
            var Q59;
            {var subQ0=sQuery(id+"F7.wireOp",EDGE,"E200.MirrorCS");Q59=makeQuery(id+"F7.imprint","IMPRINT",FACE,{"disambiguationData":[TD([[makeQuery(id+"F7.imprint","IMPRINT",EDGE,{"derivedFrom":subQ0}),1.0]])]});}
            var Q60;
            {var subQ0=sQuery(id+"F7.wireOp",EDGE,"E202.MirrorCS");Q60=makeQuery(id+"F7.imprint","IMPRINT",FACE,{"disambiguationData":[TD([[makeQuery(id+"F7.imprint","IMPRINT",EDGE,{"derivedFrom":subQ0}),1.0]])]});}
            var Q61;
            {var subQ0=sQuery(id+"F7.wireOp",EDGE,"E204.MirrorCS");Q61=makeQuery(id+"F7.imprint","IMPRINT",FACE,{"disambiguationData":[TD([[makeQuery(id+"F7.imprint","IMPRINT",EDGE,{"derivedFrom":subQ0}),1.0]])]});}
            var Q62;
            {var subQ0=sQuery(id+"F7.wireOp",EDGE,"E206.MirrorCS");Q62=makeQuery(id+"F7.imprint","IMPRINT",FACE,{"disambiguationData":[TD([[makeQuery(id+"F7.imprint","IMPRINT",EDGE,{"derivedFrom":subQ0}),1.0]])]});}
            var Q63;
            {var subQ0=sQuery(id+"F7.wireOp",EDGE,"E208.MirrorCS");Q63=makeQuery(id+"F7.imprint","IMPRINT",FACE,{"disambiguationData":[TD([[makeQuery(id+"F7.imprint","IMPRINT",EDGE,{"derivedFrom":subQ0}),1.0]])]});}
            var Q64;
            {var subQ0=sQuery(id+"F7.wireOp",EDGE,"E210.MirrorCS");Q64=makeQuery(id+"F7.imprint","IMPRINT",FACE,{"disambiguationData":[TD([[makeQuery(id+"F7.imprint","IMPRINT",EDGE,{"derivedFrom":subQ0}),1.0]])]});}
            var Q65;
            {var subQ0=sQuery(id+"F7.wireOp",EDGE,"E212.MirrorCS");Q65=makeQuery(id+"F7.imprint","IMPRINT",FACE,{"disambiguationData":[TD([[makeQuery(id+"F7.imprint","IMPRINT",EDGE,{"derivedFrom":subQ0}),1.0]])]});}
            var Q66;
            {var subQ0=sQuery(id+"F7.wireOp",EDGE,"E214.MirrorCS");Q66=makeQuery(id+"F7.imprint","IMPRINT",FACE,{"disambiguationData":[TD([[makeQuery(id+"F7.imprint","IMPRINT",EDGE,{"derivedFrom":subQ0}),1.0]])]});}
            var Q67;
            {var subQ0=sQuery(id+"F7.wireOp",EDGE,"E216.MirrorCS");Q67=makeQuery(id+"F7.imprint","IMPRINT",FACE,{"disambiguationData":[TD([[makeQuery(id+"F7.imprint","IMPRINT",EDGE,{"derivedFrom":subQ0}),1.0]])]});}
            var Q68;
            {var subQ0=sQuery(id+"F7.wireOp",EDGE,"E218.MirrorCS");Q68=makeQuery(id+"F7.imprint","IMPRINT",FACE,{"disambiguationData":[TD([[makeQuery(id+"F7.imprint","IMPRINT",EDGE,{"derivedFrom":subQ0}),1.0]])]});}
            var Q69;
            {var subQ0=sQuery(id+"F7.wireOp",EDGE,"E220.MirrorCS");Q69=makeQuery(id+"F7.imprint","IMPRINT",FACE,{"disambiguationData":[TD([[makeQuery(id+"F7.imprint","IMPRINT",EDGE,{"derivedFrom":subQ0}),1.0]])]});}
            var Q70;
            {var subQ0=sQuery(id+"F7.wireOp",EDGE,"E222.MirrorCS");Q70=makeQuery(id+"F7.imprint","IMPRINT",FACE,{"disambiguationData":[TD([[makeQuery(id+"F7.imprint","IMPRINT",EDGE,{"derivedFrom":subQ0}),1.0]])]});}
            var Q71;
            {var subQ0=sQuery(id+"F7.wireOp",EDGE,"E224.MirrorCS");Q71=makeQuery(id+"F7.imprint","IMPRINT",FACE,{"disambiguationData":[TD([[makeQuery(id+"F7.imprint","IMPRINT",EDGE,{"derivedFrom":subQ0}),1.0]])]});}
            var Q72;
            {var subQ0=sQuery(id+"F7.wireOp",EDGE,"E226.MirrorCS");Q72=makeQuery(id+"F7.imprint","IMPRINT",FACE,{"disambiguationData":[TD([[makeQuery(id+"F7.imprint","IMPRINT",EDGE,{"derivedFrom":subQ0}),1.0]])]});}
            var Q73;
            {var subQ0=sQuery(id+"F7.wireOp",EDGE,"E228.MirrorCS");Q73=makeQuery(id+"F7.imprint","IMPRINT",FACE,{"disambiguationData":[TD([[makeQuery(id+"F7.imprint","IMPRINT",EDGE,{"derivedFrom":subQ0}),1.0]])]});}
            var Q74;
            {var subQ0=sQuery(id+"F7.wireOp",EDGE,"E230.MirrorCS");Q74=makeQuery(id+"F7.imprint","IMPRINT",FACE,{"disambiguationData":[TD([[makeQuery(id+"F7.imprint","IMPRINT",EDGE,{"derivedFrom":subQ0}),1.0]])]});}
            var Q75;
            {var subQ0=sQuery(id+"F7.wireOp",EDGE,"E232.MirrorCS");Q75=makeQuery(id+"F7.imprint","IMPRINT",FACE,{"disambiguationData":[TD([[makeQuery(id+"F7.imprint","IMPRINT",EDGE,{"derivedFrom":subQ0}),1.0]])]});}
            var Q76;
            {var subQ0=sQuery(id+"F7.wireOp",EDGE,"E234.MirrorCS");Q76=makeQuery(id+"F7.imprint","IMPRINT",FACE,{"disambiguationData":[TD([[makeQuery(id+"F7.imprint","IMPRINT",EDGE,{"derivedFrom":subQ0}),1.0]])]});}
            var Q77;
            {var subQ0=sQuery(id+"F7.wireOp",EDGE,"E236.MirrorCS");Q77=makeQuery(id+"F7.imprint","IMPRINT",FACE,{"disambiguationData":[TD([[makeQuery(id+"F7.imprint","IMPRINT",EDGE,{"derivedFrom":subQ0}),1.0]])]});}
            var Q78;
            {var subQ0=sQuery(id+"F7.wireOp",EDGE,"E238.MirrorCS");Q78=makeQuery(id+"F7.imprint","IMPRINT",FACE,{"disambiguationData":[TD([[makeQuery(id+"F7.imprint","IMPRINT",EDGE,{"derivedFrom":subQ0}),1.0]])]});}
            var Q79;
            {var subQ0=sQuery(id+"F7.wireOp",EDGE,"E240.MirrorCS");Q79=makeQuery(id+"F7.imprint","IMPRINT",FACE,{"disambiguationData":[TD([[makeQuery(id+"F7.imprint","IMPRINT",EDGE,{"derivedFrom":subQ0}),1.0]])]});}
            var Q80;
            {var subQ0=sQuery(id+"F7.wireOp",EDGE,"E242.MirrorCS");Q80=makeQuery(id+"F7.imprint","IMPRINT",FACE,{"disambiguationData":[TD([[makeQuery(id+"F7.imprint","IMPRINT",EDGE,{"derivedFrom":subQ0}),1.0]])]});}
            var Q81;
            {var subQ0=sQuery(id+"F7.wireOp",EDGE,"E244.MirrorCS");Q81=makeQuery(id+"F7.imprint","IMPRINT",FACE,{"disambiguationData":[TD([[makeQuery(id+"F7.imprint","IMPRINT",EDGE,{"derivedFrom":subQ0}),1.0]])]});}
            var Q82;
            {var subQ0=sQuery(id+"F7.wireOp",EDGE,"E246.MirrorCS");Q82=makeQuery(id+"F7.imprint","IMPRINT",FACE,{"disambiguationData":[TD([[makeQuery(id+"F7.imprint","IMPRINT",EDGE,{"derivedFrom":subQ0}),1.0]])]});}
            var Q83;
            {var subQ0=sQuery(id+"F7.wireOp",EDGE,"E248.MirrorCS");Q83=makeQuery(id+"F7.imprint","IMPRINT",FACE,{"disambiguationData":[TD([[makeQuery(id+"F7.imprint","IMPRINT",EDGE,{"derivedFrom":subQ0}),1.0]])]});}
            var Q84;
            {var subQ0=sQuery(id+"F7.wireOp",EDGE,"E252.MirrorCS");Q84=makeQuery(id+"F7.imprint","IMPRINT",FACE,{"disambiguationData":[TD([[makeQuery(id+"F7.imprint","IMPRINT",EDGE,{"derivedFrom":subQ0}),1.0]])]});}
            var Q85;
            {var subQ0=sQuery(id+"F7.wireOp",EDGE,"E254.MirrorCS");Q85=makeQuery(id+"F7.imprint","IMPRINT",FACE,{"disambiguationData":[TD([[makeQuery(id+"F7.imprint","IMPRINT",EDGE,{"derivedFrom":subQ0}),1.0]])]});}
            var Q86;
            {var subQ0=sQuery(id+"F7.wireOp",EDGE,"E256.MirrorCS");Q86=makeQuery(id+"F7.imprint","IMPRINT",FACE,{"disambiguationData":[TD([[makeQuery(id+"F7.imprint","IMPRINT",EDGE,{"derivedFrom":subQ0}),1.0]])]});}
            var Q87;
            {var subQ0=sQuery(id+"F7.wireOp",EDGE,"E258.MirrorCS");Q87=makeQuery(id+"F7.imprint","IMPRINT",FACE,{"disambiguationData":[TD([[makeQuery(id+"F7.imprint","IMPRINT",EDGE,{"derivedFrom":subQ0}),1.0]])]});}
            var Q88;
            {var subQ0=sQuery(id+"F7.wireOp",EDGE,"E301.MirrorCS");Q88=makeQuery(id+"F7.imprint","IMPRINT",FACE,{"disambiguationData":[TD([[makeQuery(id+"F7.imprint","IMPRINT",EDGE,{"derivedFrom":subQ0}),1.0]])]});}
            var Q89;
            {var subQ0=sQuery(id+"F7.wireOp",EDGE,"E299.MirrorCS");Q89=makeQuery(id+"F7.imprint","IMPRINT",FACE,{"disambiguationData":[TD([[makeQuery(id+"F7.imprint","IMPRINT",EDGE,{"derivedFrom":subQ0}),1.0]])]});}
            var Q90;
            {var subQ0=sQuery(id+"F7.wireOp",EDGE,"E297.MirrorCS");Q90=makeQuery(id+"F7.imprint","IMPRINT",FACE,{"disambiguationData":[TD([[makeQuery(id+"F7.imprint","IMPRINT",EDGE,{"derivedFrom":subQ0}),1.0]])]});}
            var Q91;
            {var subQ0=sQuery(id+"F7.wireOp",EDGE,"E295.MirrorCS");Q91=makeQuery(id+"F7.imprint","IMPRINT",FACE,{"disambiguationData":[TD([[makeQuery(id+"F7.imprint","IMPRINT",EDGE,{"derivedFrom":subQ0}),1.0]])]});}
            var Q92;
            {var subQ0=sQuery(id+"F7.wireOp",EDGE,"E293.MirrorCS");Q92=makeQuery(id+"F7.imprint","IMPRINT",FACE,{"disambiguationData":[TD([[makeQuery(id+"F7.imprint","IMPRINT",EDGE,{"derivedFrom":subQ0}),1.0]])]});}
            var Q93;
            {var subQ0=sQuery(id+"F7.wireOp",EDGE,"E291.MirrorCS");Q93=makeQuery(id+"F7.imprint","IMPRINT",FACE,{"disambiguationData":[TD([[makeQuery(id+"F7.imprint","IMPRINT",EDGE,{"derivedFrom":subQ0}),1.0]])]});}
            var Q94;
            {var subQ0=sQuery(id+"F7.wireOp",EDGE,"E289.MirrorCS");Q94=makeQuery(id+"F7.imprint","IMPRINT",FACE,{"disambiguationData":[TD([[makeQuery(id+"F7.imprint","IMPRINT",EDGE,{"derivedFrom":subQ0}),1.0]])]});}
            var Q95;
            {var subQ0=sQuery(id+"F7.wireOp",EDGE,"E287.MirrorCS");Q95=makeQuery(id+"F7.imprint","IMPRINT",FACE,{"disambiguationData":[TD([[makeQuery(id+"F7.imprint","IMPRINT",EDGE,{"derivedFrom":subQ0}),1.0]])]});}
            var Q96;
            {var subQ0=sQuery(id+"F7.wireOp",EDGE,"E283.MirrorCS");Q96=makeQuery(id+"F7.imprint","IMPRINT",FACE,{"disambiguationData":[TD([[makeQuery(id+"F7.imprint","IMPRINT",EDGE,{"derivedFrom":subQ0}),1.0]])]});}
            var Q97;
            {var subQ0=sQuery(id+"F7.wireOp",EDGE,"E250.MirrorCS");Q97=makeQuery(id+"F7.imprint","IMPRINT",FACE,{"disambiguationData":[TD([[makeQuery(id+"F7.imprint","IMPRINT",EDGE,{"derivedFrom":subQ0}),1.0]])]});}
            var Q98;
            {var subQ0=sQuery(id+"F7.wireOp",EDGE,"E285.MirrorCS");Q98=makeQuery(id+"F7.imprint","IMPRINT",FACE,{"disambiguationData":[TD([[makeQuery(id+"F7.imprint","IMPRINT",EDGE,{"derivedFrom":subQ0}),1.0]])]});}
            var Q99;
            {var subQ0=sQuery(id+"F7.wireOp",EDGE,"E281.MirrorCS");Q99=makeQuery(id+"F7.imprint","IMPRINT",FACE,{"disambiguationData":[TD([[makeQuery(id+"F7.imprint","IMPRINT",EDGE,{"derivedFrom":subQ0}),1.0]])]});}
            var Q100;
            {var subQ0=sQuery(id+"F7.wireOp",EDGE,"E279.MirrorCS");Q100=makeQuery(id+"F7.imprint","IMPRINT",FACE,{"disambiguationData":[TD([[makeQuery(id+"F7.imprint","IMPRINT",EDGE,{"derivedFrom":subQ0}),1.0]])]});}
            var Q101;
            {var subQ0=sQuery(id+"F7.wireOp",EDGE,"E277.MirrorCS");Q101=makeQuery(id+"F7.imprint","IMPRINT",FACE,{"disambiguationData":[TD([[makeQuery(id+"F7.imprint","IMPRINT",EDGE,{"derivedFrom":subQ0}),1.0]])]});}
            var Q102;
            {var subQ0=sQuery(id+"F7.wireOp",EDGE,"E271.MirrorCS");Q102=makeQuery(id+"F7.imprint","IMPRINT",FACE,{"disambiguationData":[TD([[makeQuery(id+"F7.imprint","IMPRINT",EDGE,{"derivedFrom":subQ0}),1.0]])]});}
            var Q103;
            {var subQ0=sQuery(id+"F7.wireOp",EDGE,"E269.MirrorCS");Q103=makeQuery(id+"F7.imprint","IMPRINT",FACE,{"disambiguationData":[TD([[makeQuery(id+"F7.imprint","IMPRINT",EDGE,{"derivedFrom":subQ0}),1.0]])]});}
            var Q104;
            {var subQ0=sQuery(id+"F7.wireOp",EDGE,"E267.MirrorCS");Q104=makeQuery(id+"F7.imprint","IMPRINT",FACE,{"disambiguationData":[TD([[makeQuery(id+"F7.imprint","IMPRINT",EDGE,{"derivedFrom":subQ0}),1.0]])]});}
            var Q105;
            {var subQ0=sQuery(id+"F7.wireOp",EDGE,"E265.MirrorCS");Q105=makeQuery(id+"F7.imprint","IMPRINT",FACE,{"disambiguationData":[TD([[makeQuery(id+"F7.imprint","IMPRINT",EDGE,{"derivedFrom":subQ0}),1.0]])]});}
            var Q106;
            {var subQ0=sQuery(id+"F7.wireOp",EDGE,"E261.MirrorCS");Q106=makeQuery(id+"F7.imprint","IMPRINT",FACE,{"disambiguationData":[TD([[makeQuery(id+"F7.imprint","IMPRINT",EDGE,{"derivedFrom":subQ0}),1.0]])]});}
            var Q107;
            {var subQ0=sQuery(id+"F7.wireOp",EDGE,"E259.MirrorCS");Q107=makeQuery(id+"F7.imprint","IMPRINT",FACE,{"disambiguationData":[TD([[makeQuery(id+"F7.imprint","IMPRINT",EDGE,{"derivedFrom":subQ0}),1.0]])]});}
            var Q108;
            {var subQ0=sQuery(id+"F7.wireOp",EDGE,"E275.MirrorCS");Q108=makeQuery(id+"F7.imprint","IMPRINT",FACE,{"disambiguationData":[TD([[makeQuery(id+"F7.imprint","IMPRINT",EDGE,{"derivedFrom":subQ0}),1.0]])]});}
            var Q109;
            {var subQ0=sQuery(id+"F7.wireOp",EDGE,"E273.MirrorCS");Q109=makeQuery(id+"F7.imprint","IMPRINT",FACE,{"disambiguationData":[TD([[makeQuery(id+"F7.imprint","IMPRINT",EDGE,{"derivedFrom":subQ0}),1.0]])]});}
            var Q110;
            {var subQ0=sQuery(id+"F7.wireOp",EDGE,"E263.MirrorCS");Q110=makeQuery(id+"F7.imprint","IMPRINT",FACE,{"disambiguationData":[TD([[makeQuery(id+"F7.imprint","IMPRINT",EDGE,{"derivedFrom":subQ0}),1.0]])]});}
            var Q111;
            {var subQ0=sQuery(id+"F7.wireOp",EDGE,"74cb0d83-953a-43af-9729-8d4360262b210.MirrorCS");Q111=makeQuery(id+"F7.imprint","IMPRINT",FACE,{"disambiguationData":[TD([[makeQuery(id+"F7.imprint","IMPRINT",EDGE,{"derivedFrom":subQ0}),1.0]])]});}
            var Q112;
            {var subQ0=sQuery(id+"F7.wireOp",EDGE,"E80.top");Q112=makeQuery(id+"F7.imprint","IMPRINT",FACE,{"disambiguationData":[TD([[makeQuery(id+"F7.imprint","IMPRINT",EDGE,{"derivedFrom":subQ0}),-1.0]])]});}
            var Q113;
            {var subQ0=sQuery(id+"F7.wireOp",EDGE,"E304.MirrorCS");Q113=makeQuery(id+"F7.imprint","IMPRINT",FACE,{"disambiguationData":[TD([[makeQuery(id+"F7.imprint","IMPRINT",EDGE,{"derivedFrom":subQ0}),1.0]])]});}
            extrude(context, id + "F8", {"entities" : qUnion([Q0, Q1, Q2, Q3, Q4, Q5, Q6, Q7, Q8, Q9, Q10, Q11, Q12, Q13, Q14, Q15, Q16, Q17, Q18, Q19, Q20, Q21, Q22, Q23, Q24, Q25, Q26, Q27, Q28, Q29, Q30, Q31, Q32, Q33, Q34, Q35, Q36, Q37, Q38, Q39, Q40, Q41, Q42, Q43, Q44, Q45, Q46, Q47, Q48, Q49, Q50, Q51, Q52, Q53, Q54, Q55, Q56, Q57, Q58, Q59, Q60, Q61, Q62, Q63, Q64, Q65, Q66, Q67, Q68, Q69, Q70, Q71, Q72, Q73, Q74, Q75, Q76, Q77, Q78, Q79, Q80, Q81, Q82, Q83, Q84, Q85, Q86, Q87, Q88, Q89, Q90, Q91, Q92, Q93, Q94, Q95, Q96, Q97, Q98, Q99, Q100, Q101, Q102, Q103, Q104, Q105, Q106, Q107, Q108, Q109, Q110, Q111, Q112, Q113]), "depth" : 3 * mm, "offsetDistance" : 25 * mm});
        }
        {
            var Q0;
            {var subQ0=sQuery(id+"F7.wireOp",EDGE,"E173.MirrorCS");Q0=makeQuery(id+"F7.imprint","IMPRINT",FACE,{"disambiguationData":[TD([[makeQuery(id+"F7.imprint","IMPRINT",EDGE,{"derivedFrom":subQ0}),-1.0]])]});}
            var Q1;
            {var subQ0=sQuery(id+"F7.wireOp",EDGE,"E115.MirrorCS");Q1=makeQuery(id+"F7.imprint","IMPRINT",FACE,{"disambiguationData":[TD([[makeQuery(id+"F7.imprint","IMPRINT",EDGE,{"derivedFrom":subQ0}),1.0]])]});}
            var Q2;
            {var subQ0=sQuery(id+"F7.wireOp",EDGE,"E143.MirrorCS");Q2=makeQuery(id+"F7.imprint","IMPRINT",FACE,{"disambiguationData":[TD([[makeQuery(id+"F7.imprint","IMPRINT",EDGE,{"derivedFrom":subQ0}),-1.0]])]});}
            var Q3;
            {var subQ0=sQuery(id+"F7.wireOp",EDGE,"E255.MirrorCS");Q3=makeQuery(id+"F7.imprint","IMPRINT",FACE,{"disambiguationData":[TD([[makeQuery(id+"F7.imprint","IMPRINT",EDGE,{"derivedFrom":subQ0}),-1.0]])]});}
            var Q4;
            {var subQ0=sQuery(id+"F7.wireOp",EDGE,"E146.MirrorCS");Q4=makeQuery(id+"F7.imprint","IMPRINT",FACE,{"disambiguationData":[TD([[makeQuery(id+"F7.imprint","IMPRINT",EDGE,{"derivedFrom":subQ0}),1.0]])]});}
            var Q5;
            {var subQ0=sQuery(id+"F7.wireOp",EDGE,"E92.MirrorCS");Q5=makeQuery(id+"F7.imprint","IMPRINT",FACE,{"disambiguationData":[TD([[makeQuery(id+"F7.imprint","IMPRINT",EDGE,{"derivedFrom":subQ0}),-1.0]])]});}
            var Q6;
            {var subQ0=sQuery(id+"F7.wireOp",EDGE,"E181.MirrorCS");Q6=makeQuery(id+"F7.imprint","IMPRINT",FACE,{"disambiguationData":[TD([[makeQuery(id+"F7.imprint","IMPRINT",EDGE,{"derivedFrom":subQ0}),-1.0]])]});}
            var Q7;
            {var subQ0=sQuery(id+"F7.wireOp",EDGE,"E145.MirrorCS");Q7=makeQuery(id+"F7.imprint","IMPRINT",FACE,{"disambiguationData":[TD([[makeQuery(id+"F7.imprint","IMPRINT",EDGE,{"derivedFrom":subQ0}),-1.0]])]});}
            var Q8;
            {var subQ0=sQuery(id+"F7.wireOp",EDGE,"E221.MirrorCS");Q8=makeQuery(id+"F7.imprint","IMPRINT",FACE,{"disambiguationData":[TD([[makeQuery(id+"F7.imprint","IMPRINT",EDGE,{"derivedFrom":subQ0}),-1.0]])]});}
            var Q9;
            {var subQ0=sQuery(id+"F7.wireOp",EDGE,"E240.MirrorCS");Q9=makeQuery(id+"F7.imprint","IMPRINT",FACE,{"disambiguationData":[TD([[makeQuery(id+"F7.imprint","IMPRINT",EDGE,{"derivedFrom":subQ0}),1.0]])]});}
            var Q10;
            {var subQ0=sQuery(id+"F7.wireOp",EDGE,"E273.MirrorCS");Q10=makeQuery(id+"F7.imprint","IMPRINT",FACE,{"disambiguationData":[TD([[makeQuery(id+"F7.imprint","IMPRINT",EDGE,{"derivedFrom":subQ0}),1.0]])]});}
            var Q11;
            {var subQ0=sQuery(id+"F7.wireOp",EDGE,"E113.MirrorCS");Q11=makeQuery(id+"F7.imprint","IMPRINT",FACE,{"disambiguationData":[TD([[makeQuery(id+"F7.imprint","IMPRINT",EDGE,{"derivedFrom":subQ0}),1.0]])]});}
            var Q12;
            {var subQ0=sQuery(id+"F7.wireOp",EDGE,"E129.MirrorCS");Q12=makeQuery(id+"F7.imprint","IMPRINT",FACE,{"disambiguationData":[TD([[makeQuery(id+"F7.imprint","IMPRINT",EDGE,{"derivedFrom":subQ0}),1.0]])]});}
            var Q13;
            {var subQ0=sQuery(id+"F7.wireOp",EDGE,"E205.MirrorCS");Q13=makeQuery(id+"F7.imprint","IMPRINT",FACE,{"disambiguationData":[TD([[makeQuery(id+"F7.imprint","IMPRINT",EDGE,{"derivedFrom":subQ0}),-1.0]])]});}
            var Q14;
            {var subQ0=sQuery(id+"F7.wireOp",EDGE,"E130.MirrorCS");Q14=makeQuery(id+"F7.imprint","IMPRINT",FACE,{"disambiguationData":[TD([[makeQuery(id+"F7.imprint","IMPRINT",EDGE,{"derivedFrom":subQ0}),-1.0]])]});}
            var Q15;
            {var subQ0=sQuery(id+"F7.wireOp",EDGE,"E264.MirrorCS");Q15=makeQuery(id+"F7.imprint","IMPRINT",FACE,{"disambiguationData":[TD([[makeQuery(id+"F7.imprint","IMPRINT",EDGE,{"derivedFrom":subQ0}),-1.0]])]});}
            var Q16;
            {var subQ0=sQuery(id+"F7.wireOp",EDGE,"E182.MirrorCS");Q16=makeQuery(id+"F7.imprint","IMPRINT",FACE,{"disambiguationData":[TD([[makeQuery(id+"F7.imprint","IMPRINT",EDGE,{"derivedFrom":subQ0}),1.0]])]});}
            var Q17;
            {var subQ0=sQuery(id+"F7.wireOp",EDGE,"E206.MirrorCS");Q17=makeQuery(id+"F7.imprint","IMPRINT",FACE,{"disambiguationData":[TD([[makeQuery(id+"F7.imprint","IMPRINT",EDGE,{"derivedFrom":subQ0}),1.0]])]});}
            var Q18;
            {var subQ0=sQuery(id+"F7.wireOp",EDGE,"E266.MirrorCS");Q18=makeQuery(id+"F7.imprint","IMPRINT",FACE,{"disambiguationData":[TD([[makeQuery(id+"F7.imprint","IMPRINT",EDGE,{"derivedFrom":subQ0}),-1.0]])]});}
            var Q19;
            {var subQ0=sQuery(id+"F7.wireOp",EDGE,"E216.MirrorCS");Q19=makeQuery(id+"F7.imprint","IMPRINT",FACE,{"disambiguationData":[TD([[makeQuery(id+"F7.imprint","IMPRINT",EDGE,{"derivedFrom":subQ0}),1.0]])]});}
            var Q20;
            {var subQ0=sQuery(id+"F7.wireOp",EDGE,"E172.MirrorCS");Q20=makeQuery(id+"F7.imprint","IMPRINT",FACE,{"disambiguationData":[TD([[makeQuery(id+"F7.imprint","IMPRINT",EDGE,{"derivedFrom":subQ0}),1.0]])]});}
            var Q21;
            {var subQ0=sQuery(id+"F7.wireOp",EDGE,"E166.MirrorCS");Q21=makeQuery(id+"F7.imprint","IMPRINT",FACE,{"disambiguationData":[TD([[makeQuery(id+"F7.imprint","IMPRINT",EDGE,{"derivedFrom":subQ0}),1.0]])]});}
            var Q22;
            {var subQ0=sQuery(id+"F7.wireOp",EDGE,"E299.MirrorCS");Q22=makeQuery(id+"F7.imprint","IMPRINT",FACE,{"disambiguationData":[TD([[makeQuery(id+"F7.imprint","IMPRINT",EDGE,{"derivedFrom":subQ0}),1.0]])]});}
            var Q23;
            {var subQ0=sQuery(id+"F7.wireOp",EDGE,"E275.MirrorCS");Q23=makeQuery(id+"F7.imprint","IMPRINT",FACE,{"disambiguationData":[TD([[makeQuery(id+"F7.imprint","IMPRINT",EDGE,{"derivedFrom":subQ0}),1.0]])]});}
            var Q24;
            {var subQ0=sQuery(id+"F7.wireOp",EDGE,"E144.MirrorCS");Q24=makeQuery(id+"F7.imprint","IMPRINT",FACE,{"disambiguationData":[TD([[makeQuery(id+"F7.imprint","IMPRINT",EDGE,{"derivedFrom":subQ0}),1.0]])]});}
            var Q25;
            {var subQ0=sQuery(id+"F7.wireOp",EDGE,"E239.MirrorCS");Q25=makeQuery(id+"F7.imprint","IMPRINT",FACE,{"disambiguationData":[TD([[makeQuery(id+"F7.imprint","IMPRINT",EDGE,{"derivedFrom":subQ0}),-1.0]])]});}
            var Q26;
            {var subQ0=sQuery(id+"F7.wireOp",EDGE,"E80.top");Q26=makeQuery(id+"F7.imprint","IMPRINT",FACE,{"disambiguationData":[TD([[makeQuery(id+"F7.imprint","IMPRINT",EDGE,{"derivedFrom":subQ0}),-1.0]])]});}
            var Q27;
            {var subQ0=sQuery(id+"F7.wireOp",EDGE,"E248.MirrorCS");Q27=makeQuery(id+"F7.imprint","IMPRINT",FACE,{"disambiguationData":[TD([[makeQuery(id+"F7.imprint","IMPRINT",EDGE,{"derivedFrom":subQ0}),1.0]])]});}
            var Q28;
            {var subQ0=sQuery(id+"F7.wireOp",EDGE,"E184.MirrorCS");Q28=makeQuery(id+"F7.imprint","IMPRINT",FACE,{"disambiguationData":[TD([[makeQuery(id+"F7.imprint","IMPRINT",EDGE,{"derivedFrom":subQ0}),1.0]])]});}
            var Q29;
            {var subQ0=sQuery(id+"F7.wireOp",EDGE,"E138.MirrorCS");Q29=makeQuery(id+"F7.imprint","IMPRINT",FACE,{"disambiguationData":[TD([[makeQuery(id+"F7.imprint","IMPRINT",EDGE,{"derivedFrom":subQ0}),-1.0]])]});}
            var Q30;
            {var subQ0=sQuery(id+"F7.wireOp",EDGE,"E139.MirrorCS");Q30=makeQuery(id+"F7.imprint","IMPRINT",FACE,{"disambiguationData":[TD([[makeQuery(id+"F7.imprint","IMPRINT",EDGE,{"derivedFrom":subQ0}),1.0]])]});}
            var Q31;
            {var subQ0=sQuery(id+"F7.wireOp",EDGE,"E292.MirrorCS");Q31=makeQuery(id+"F7.imprint","IMPRINT",FACE,{"disambiguationData":[TD([[makeQuery(id+"F7.imprint","IMPRINT",EDGE,{"derivedFrom":subQ0}),-1.0]])]});}
            var Q32;
            {var subQ0=sQuery(id+"F7.wireOp",EDGE,"E154.MirrorCS");Q32=makeQuery(id+"F7.imprint","IMPRINT",FACE,{"disambiguationData":[TD([[makeQuery(id+"F7.imprint","IMPRINT",EDGE,{"derivedFrom":subQ0}),1.0]])]});}
            var Q33;
            {var subQ0=sQuery(id+"F7.wireOp",EDGE,"E137.MirrorCS");Q33=makeQuery(id+"F7.imprint","IMPRINT",FACE,{"disambiguationData":[TD([[makeQuery(id+"F7.imprint","IMPRINT",EDGE,{"derivedFrom":subQ0}),1.0]])]});}
            var Q34;
            {var subQ0=sQuery(id+"F7.wireOp",EDGE,"E222.MirrorCS");Q34=makeQuery(id+"F7.imprint","IMPRINT",FACE,{"disambiguationData":[TD([[makeQuery(id+"F7.imprint","IMPRINT",EDGE,{"derivedFrom":subQ0}),1.0]])]});}
            var Q35;
            {var subQ0=sQuery(id+"F7.wireOp",EDGE,"E175.MirrorCS");Q35=makeQuery(id+"F7.imprint","IMPRINT",FACE,{"disambiguationData":[TD([[makeQuery(id+"F7.imprint","IMPRINT",EDGE,{"derivedFrom":subQ0}),-1.0]])]});}
            var Q36;
            {var subQ0=sQuery(id+"F7.wireOp",EDGE,"E131.MirrorCS");Q36=makeQuery(id+"F7.imprint","IMPRINT",FACE,{"disambiguationData":[TD([[makeQuery(id+"F7.imprint","IMPRINT",EDGE,{"derivedFrom":subQ0}),1.0]])]});}
            var Q37;
            {var subQ0=sQuery(id+"F7.wireOp",EDGE,"E122.MirrorCS");Q37=makeQuery(id+"F7.imprint","IMPRINT",FACE,{"disambiguationData":[TD([[makeQuery(id+"F7.imprint","IMPRINT",EDGE,{"derivedFrom":subQ0}),-1.0]])]});}
            var Q38;
            {var subQ0=sQuery(id+"F7.wireOp",EDGE,"E191.MirrorCS");Q38=makeQuery(id+"F7.imprint","IMPRINT",FACE,{"disambiguationData":[TD([[makeQuery(id+"F7.imprint","IMPRINT",EDGE,{"derivedFrom":subQ0}),-1.0]])]});}
            var Q39;
            {var subQ0=sQuery(id+"F7.wireOp",EDGE,"E153.MirrorCS");Q39=makeQuery(id+"F7.imprint","IMPRINT",FACE,{"disambiguationData":[TD([[makeQuery(id+"F7.imprint","IMPRINT",EDGE,{"derivedFrom":subQ0}),-1.0]])]});}
            var Q40;
            {var subQ0=sQuery(id+"F7.wireOp",EDGE,"E123.MirrorCS");Q40=makeQuery(id+"F7.imprint","IMPRINT",FACE,{"disambiguationData":[TD([[makeQuery(id+"F7.imprint","IMPRINT",EDGE,{"derivedFrom":subQ0}),1.0]])]});}
            var Q41;
            {var subQ0=sQuery(id+"F7.wireOp",EDGE,"E80.bottom");Q41=makeQuery(id+"F7.imprint","IMPRINT",FACE,{"disambiguationData":[TD([[makeQuery(id+"F7.imprint","IMPRINT",EDGE,{"derivedFrom":subQ0}),1.0]])]});}
            var Q42;
            {var subQ0=sQuery(id+"F7.wireOp",EDGE,"E214.MirrorCS");Q42=makeQuery(id+"F7.imprint","IMPRINT",FACE,{"disambiguationData":[TD([[makeQuery(id+"F7.imprint","IMPRINT",EDGE,{"derivedFrom":subQ0}),1.0]])]});}
            var Q43;
            {var subQ0=sQuery(id+"F7.wireOp",EDGE,"E91.MirrorCS");Q43=makeQuery(id+"F7.imprint","IMPRINT",FACE,{"disambiguationData":[TD([[makeQuery(id+"F7.imprint","IMPRINT",EDGE,{"derivedFrom":subQ0}),1.0]])]});}
            var Q44;
            {var subQ0=sQuery(id+"F7.wireOp",EDGE,"E180.MirrorCS");Q44=makeQuery(id+"F7.imprint","IMPRINT",FACE,{"disambiguationData":[TD([[makeQuery(id+"F7.imprint","IMPRINT",EDGE,{"derivedFrom":subQ0}),1.0]])]});}
            var Q45;
            {var subQ0=sQuery(id+"F7.wireOp",EDGE,"E151.MirrorCS");Q45=makeQuery(id+"F7.imprint","IMPRINT",FACE,{"disambiguationData":[TD([[makeQuery(id+"F7.imprint","IMPRINT",EDGE,{"derivedFrom":subQ0}),-1.0]])]});}
            var Q46;
            {var subQ0=sQuery(id+"F7.wireOp",EDGE,"E190.MirrorCS");Q46=makeQuery(id+"F7.imprint","IMPRINT",FACE,{"disambiguationData":[TD([[makeQuery(id+"F7.imprint","IMPRINT",EDGE,{"derivedFrom":subQ0}),1.0]])]});}
            var Q47;
            {var subQ0=sQuery(id+"F7.wireOp",EDGE,"E100.MirrorCS");Q47=makeQuery(id+"F7.imprint","IMPRINT",FACE,{"disambiguationData":[TD([[makeQuery(id+"F7.imprint","IMPRINT",EDGE,{"derivedFrom":subQ0}),-1.0]])]});}
            var Q48;
            {var subQ0=sQuery(id+"F7.wireOp",EDGE,"E229.MirrorCS");Q48=makeQuery(id+"F7.imprint","IMPRINT",FACE,{"disambiguationData":[TD([[makeQuery(id+"F7.imprint","IMPRINT",EDGE,{"derivedFrom":subQ0}),-1.0]])]});}
            var Q49;
            {var subQ0=sQuery(id+"F7.wireOp",EDGE,"E253.MirrorCS");Q49=makeQuery(id+"F7.imprint","IMPRINT",FACE,{"disambiguationData":[TD([[makeQuery(id+"F7.imprint","IMPRINT",EDGE,{"derivedFrom":subQ0}),-1.0]])]});}
            var Q50;
            {var subQ0=sQuery(id+"F7.wireOp",EDGE,"E207.MirrorCS");Q50=makeQuery(id+"F7.imprint","IMPRINT",FACE,{"disambiguationData":[TD([[makeQuery(id+"F7.imprint","IMPRINT",EDGE,{"derivedFrom":subQ0}),-1.0]])]});}
            var Q51;
            {var subQ0=sQuery(id+"F7.wireOp",EDGE,"E238.MirrorCS");Q51=makeQuery(id+"F7.imprint","IMPRINT",FACE,{"disambiguationData":[TD([[makeQuery(id+"F7.imprint","IMPRINT",EDGE,{"derivedFrom":subQ0}),1.0]])]});}
            var Q52;
            {var subQ0=sQuery(id+"F7.wireOp",EDGE,"E98.MirrorCS");Q52=makeQuery(id+"F7.imprint","IMPRINT",FACE,{"disambiguationData":[TD([[makeQuery(id+"F7.imprint","IMPRINT",EDGE,{"derivedFrom":subQ0}),-1.0]])]});}
            var Q53;
            {var subQ0=sQuery(id+"F7.wireOp",EDGE,"E230.MirrorCS");Q53=makeQuery(id+"F7.imprint","IMPRINT",FACE,{"disambiguationData":[TD([[makeQuery(id+"F7.imprint","IMPRINT",EDGE,{"derivedFrom":subQ0}),1.0]])]});}
            var Q54;
            {var subQ0=sQuery(id+"F7.wireOp",EDGE,"E167.MirrorCS");Q54=makeQuery(id+"F7.imprint","IMPRINT",FACE,{"disambiguationData":[TD([[makeQuery(id+"F7.imprint","IMPRINT",EDGE,{"derivedFrom":subQ0}),-1.0]])]});}
            var Q55;
            {var subQ0=sQuery(id+"F7.wireOp",EDGE,"E300.MirrorCS");Q55=makeQuery(id+"F7.imprint","IMPRINT",FACE,{"disambiguationData":[TD([[makeQuery(id+"F7.imprint","IMPRINT",EDGE,{"derivedFrom":subQ0}),-1.0]])]});}
            var Q56;
            {var subQ0=sQuery(id+"F7.wireOp",EDGE,"E267.MirrorCS");Q56=makeQuery(id+"F7.imprint","IMPRINT",FACE,{"disambiguationData":[TD([[makeQuery(id+"F7.imprint","IMPRINT",EDGE,{"derivedFrom":subQ0}),1.0]])]});}
            var Q57;
            {var subQ0=sQuery(id+"F7.wireOp",EDGE,"E289.MirrorCS");Q57=makeQuery(id+"F7.imprint","IMPRINT",FACE,{"disambiguationData":[TD([[makeQuery(id+"F7.imprint","IMPRINT",EDGE,{"derivedFrom":subQ0}),1.0]])]});}
            var Q58;
            {var subQ0=sQuery(id+"F7.wireOp",EDGE,"E288.MirrorCS");Q58=makeQuery(id+"F7.imprint","IMPRINT",FACE,{"disambiguationData":[TD([[makeQuery(id+"F7.imprint","IMPRINT",EDGE,{"derivedFrom":subQ0}),-1.0]])]});}
            var Q59;
            {var subQ0=sQuery(id+"F7.wireOp",EDGE,"E114.MirrorCS");Q59=makeQuery(id+"F7.imprint","IMPRINT",FACE,{"disambiguationData":[TD([[makeQuery(id+"F7.imprint","IMPRINT",EDGE,{"derivedFrom":subQ0}),-1.0]])]});}
            var Q60;
            {var subQ0=sQuery(id+"F7.wireOp",EDGE,"E283.MirrorCS");Q60=makeQuery(id+"F7.imprint","IMPRINT",FACE,{"disambiguationData":[TD([[makeQuery(id+"F7.imprint","IMPRINT",EDGE,{"derivedFrom":subQ0}),1.0]])]});}
            var Q61;
            {var subQ0=sQuery(id+"F7.wireOp",EDGE,"E224.MirrorCS");Q61=makeQuery(id+"F7.imprint","IMPRINT",FACE,{"disambiguationData":[TD([[makeQuery(id+"F7.imprint","IMPRINT",EDGE,{"derivedFrom":subQ0}),1.0]])]});}
            var Q62;
            {var subQ0=sQuery(id+"F7.wireOp",EDGE,"E265.MirrorCS");Q62=makeQuery(id+"F7.imprint","IMPRINT",FACE,{"disambiguationData":[TD([[makeQuery(id+"F7.imprint","IMPRINT",EDGE,{"derivedFrom":subQ0}),1.0]])]});}
            var Q63;
            {var subQ0=sQuery(id+"F7.wireOp",EDGE,"E197.MirrorCS");Q63=makeQuery(id+"F7.imprint","IMPRINT",FACE,{"disambiguationData":[TD([[makeQuery(id+"F7.imprint","IMPRINT",EDGE,{"derivedFrom":subQ0}),-1.0]])]});}
            var Q64;
            {var subQ0=sQuery(id+"F7.wireOp",EDGE,"E208.MirrorCS");Q64=makeQuery(id+"F7.imprint","IMPRINT",FACE,{"disambiguationData":[TD([[makeQuery(id+"F7.imprint","IMPRINT",EDGE,{"derivedFrom":subQ0}),1.0]])]});}
            var Q65;
            {var subQ0=sQuery(id+"F7.wireOp",EDGE,"E136.MirrorCS");Q65=makeQuery(id+"F7.imprint","IMPRINT",FACE,{"disambiguationData":[TD([[makeQuery(id+"F7.imprint","IMPRINT",EDGE,{"derivedFrom":subQ0}),-1.0]])]});}
            var Q66;
            {var subQ0=sQuery(id+"F7.wireOp",EDGE,"E280.MirrorCS");Q66=makeQuery(id+"F7.imprint","IMPRINT",FACE,{"disambiguationData":[TD([[makeQuery(id+"F7.imprint","IMPRINT",EDGE,{"derivedFrom":subQ0}),-1.0]])]});}
            var Q67;
            {var subQ0=sQuery(id+"F7.wireOp",EDGE,"E107.MirrorCS");Q67=makeQuery(id+"F7.imprint","IMPRINT",FACE,{"disambiguationData":[TD([[makeQuery(id+"F7.imprint","IMPRINT",EDGE,{"derivedFrom":subQ0}),1.0]])]});}
            var Q68;
            {var subQ0=sQuery(id+"F7.wireOp",EDGE,"E81");Q68=makeQuery(id+"F7.imprint","IMPRINT",FACE,{"disambiguationData":[TD([[makeQuery(id+"F7.imprint","IMPRINT",EDGE,{"derivedFrom":subQ0}),-1.0]])]});}
            var Q69;
            {var subQ0=sQuery(id+"F7.wireOp",EDGE,"E223.MirrorCS");Q69=makeQuery(id+"F7.imprint","IMPRINT",FACE,{"disambiguationData":[TD([[makeQuery(id+"F7.imprint","IMPRINT",EDGE,{"derivedFrom":subQ0}),-1.0]])]});}
            var Q70;
            {var subQ0=sQuery(id+"F7.wireOp",EDGE,"E199.MirrorCS");Q70=makeQuery(id+"F7.imprint","IMPRINT",FACE,{"disambiguationData":[TD([[makeQuery(id+"F7.imprint","IMPRINT",EDGE,{"derivedFrom":subQ0}),-1.0]])]});}
            var Q71;
            {var subQ0=sQuery(id+"F7.wireOp",EDGE,"E159.MirrorCS");Q71=makeQuery(id+"F7.imprint","IMPRINT",FACE,{"disambiguationData":[TD([[makeQuery(id+"F7.imprint","IMPRINT",EDGE,{"derivedFrom":subQ0}),-1.0]])]});}
            var Q72;
            {var subQ0=sQuery(id+"F7.wireOp",EDGE,"E88.MirrorCS");Q72=makeQuery(id+"F7.imprint","IMPRINT",FACE,{"disambiguationData":[TD([[makeQuery(id+"F7.imprint","IMPRINT",EDGE,{"derivedFrom":subQ0}),-1.0]])]});}
            var Q73;
            {var subQ0=sQuery(id+"F7.wireOp",EDGE,"E232.MirrorCS");Q73=makeQuery(id+"F7.imprint","IMPRINT",FACE,{"disambiguationData":[TD([[makeQuery(id+"F7.imprint","IMPRINT",EDGE,{"derivedFrom":subQ0}),1.0]])]});}
            var Q74;
            {var subQ0=sQuery(id+"F7.wireOp",EDGE,"E297.MirrorCS");Q74=makeQuery(id+"F7.imprint","IMPRINT",FACE,{"disambiguationData":[TD([[makeQuery(id+"F7.imprint","IMPRINT",EDGE,{"derivedFrom":subQ0}),1.0]])]});}
            var Q75;
            {var subQ0=sQuery(id+"F7.wireOp",EDGE,"E213.MirrorCS");Q75=makeQuery(id+"F7.imprint","IMPRINT",FACE,{"disambiguationData":[TD([[makeQuery(id+"F7.imprint","IMPRINT",EDGE,{"derivedFrom":subQ0}),-1.0]])]});}
            var Q76;
            {var subQ0=sQuery(id+"F7.wireOp",EDGE,"E122.MirrorCS");Q76=makeQuery(id+"F7.imprint","IMPRINT",FACE,{"disambiguationData":[TD([[makeQuery(id+"F7.imprint","IMPRINT",EDGE,{"derivedFrom":subQ0}),1.0]])]});}
            var Q77;
            {var subQ0=sQuery(id+"F7.wireOp",EDGE,"E106.MirrorCS");Q77=makeQuery(id+"F7.imprint","IMPRINT",FACE,{"disambiguationData":[TD([[makeQuery(id+"F7.imprint","IMPRINT",EDGE,{"derivedFrom":subQ0}),-1.0]])]});}
            var Q78;
            {var subQ0=sQuery(id+"F7.wireOp",EDGE,"E97.MirrorCS");Q78=makeQuery(id+"F7.imprint","IMPRINT",FACE,{"disambiguationData":[TD([[makeQuery(id+"F7.imprint","IMPRINT",EDGE,{"derivedFrom":subQ0}),1.0]])]});}
            var Q79;
            {var subQ0=sQuery(id+"F7.wireOp",EDGE,"E105.MirrorCS");Q79=makeQuery(id+"F7.imprint","IMPRINT",FACE,{"disambiguationData":[TD([[makeQuery(id+"F7.imprint","IMPRINT",EDGE,{"derivedFrom":subQ0}),1.0]])]});}
            var Q80;
            {var subQ0=sQuery(id+"F7.wireOp",EDGE,"E231.MirrorCS");Q80=makeQuery(id+"F7.imprint","IMPRINT",FACE,{"disambiguationData":[TD([[makeQuery(id+"F7.imprint","IMPRINT",EDGE,{"derivedFrom":subQ0}),-1.0]])]});}
            var Q81;
            {var subQ0=sQuery(id+"F7.wireOp",EDGE,"E164.MirrorCS");Q81=makeQuery(id+"F7.imprint","IMPRINT",FACE,{"disambiguationData":[TD([[makeQuery(id+"F7.imprint","IMPRINT",EDGE,{"derivedFrom":subQ0}),1.0]])]});}
            var Q82;
            {var subQ0=sQuery(id+"F7.wireOp",EDGE,"E282.MirrorCS");Q82=makeQuery(id+"F7.imprint","IMPRINT",FACE,{"disambiguationData":[TD([[makeQuery(id+"F7.imprint","IMPRINT",EDGE,{"derivedFrom":subQ0}),-1.0]])]});}
            var Q83;
            {var subQ0=sQuery(id+"F7.wireOp",EDGE,"E165.MirrorCS");Q83=makeQuery(id+"F7.imprint","IMPRINT",FACE,{"disambiguationData":[TD([[makeQuery(id+"F7.imprint","IMPRINT",EDGE,{"derivedFrom":subQ0}),-1.0]])]});}
            var Q84;
            {var subQ0=sQuery(id+"F7.wireOp",EDGE,"E259.MirrorCS");Q84=makeQuery(id+"F7.imprint","IMPRINT",FACE,{"disambiguationData":[TD([[makeQuery(id+"F7.imprint","IMPRINT",EDGE,{"derivedFrom":subQ0}),1.0]])]});}
            var Q85;
            {var subQ2=sQuery(id+"F7.wireOp",EDGE,"E259.MirrorCS");Q85=makeQuery(id+"F7.imprint","IMPRINT",FACE,{"disambiguationData":[TD([[makeQuery(id+"F7.imprint","IMPRINT",EDGE,{"derivedFrom":subQ2}),-1.0]])]});}
            var Q86;
            {var subQ0=sQuery(id+"F7.wireOp",EDGE,"E256.MirrorCS");Q86=makeQuery(id+"F7.imprint","IMPRINT",FACE,{"disambiguationData":[TD([[makeQuery(id+"F7.imprint","IMPRINT",EDGE,{"derivedFrom":subQ0}),1.0]])]});}
            var Q87;
            {var subQ0=sQuery(id+"F7.wireOp",EDGE,"E183.MirrorCS");Q87=makeQuery(id+"F7.imprint","IMPRINT",FACE,{"disambiguationData":[TD([[makeQuery(id+"F7.imprint","IMPRINT",EDGE,{"derivedFrom":subQ0}),-1.0]])]});}
            var Q88;
            {var subQ0=sQuery(id+"F7.wireOp",EDGE,"E254.MirrorCS");Q88=makeQuery(id+"F7.imprint","IMPRINT",FACE,{"disambiguationData":[TD([[makeQuery(id+"F7.imprint","IMPRINT",EDGE,{"derivedFrom":subQ0}),1.0]])]});}
            var Q89;
            {var subQ0=sQuery(id+"F7.wireOp",EDGE,"E281.MirrorCS");Q89=makeQuery(id+"F7.imprint","IMPRINT",FACE,{"disambiguationData":[TD([[makeQuery(id+"F7.imprint","IMPRINT",EDGE,{"derivedFrom":subQ0}),1.0]])]});}
            var Q90;
            {var subQ0=sQuery(id+"F7.wireOp",EDGE,"E290.MirrorCS");Q90=makeQuery(id+"F7.imprint","IMPRINT",FACE,{"disambiguationData":[TD([[makeQuery(id+"F7.imprint","IMPRINT",EDGE,{"derivedFrom":subQ0}),-1.0]])]});}
            var Q91;
            {var subQ0=sQuery(id+"F7.wireOp",EDGE,"E83.MirrorCS");Q91=makeQuery(id+"F7.imprint","IMPRINT",FACE,{"disambiguationData":[TD([[makeQuery(id+"F7.imprint","IMPRINT",EDGE,{"derivedFrom":subQ0}),1.0]])]});}
            var Q92;
            {var subQ0=sQuery(id+"F7.wireOp",EDGE,"E198.MirrorCS");Q92=makeQuery(id+"F7.imprint","IMPRINT",FACE,{"disambiguationData":[TD([[makeQuery(id+"F7.imprint","IMPRINT",EDGE,{"derivedFrom":subQ0}),1.0]])]});}
            var Q93;
            {var subQ0=sQuery(id+"F7.wireOp",EDGE,"E116.MirrorCS");Q93=makeQuery(id+"F7.imprint","IMPRINT",FACE,{"disambiguationData":[TD([[makeQuery(id+"F7.imprint","IMPRINT",EDGE,{"derivedFrom":subQ0}),-1.0]])]});}
            var Q94;
            {var subQ0=sQuery(id+"F7.wireOp",EDGE,"E274.MirrorCS");Q94=makeQuery(id+"F7.imprint","IMPRINT",FACE,{"disambiguationData":[TD([[makeQuery(id+"F7.imprint","IMPRINT",EDGE,{"derivedFrom":subQ0}),-1.0]])]});}
            var Q95;
            {var subQ0=sQuery(id+"F7.wireOp",EDGE,"E298.MirrorCS");Q95=makeQuery(id+"F7.imprint","IMPRINT",FACE,{"disambiguationData":[TD([[makeQuery(id+"F7.imprint","IMPRINT",EDGE,{"derivedFrom":subQ0}),-1.0]])]});}
            var Q96;
            {var subQ0=sQuery(id+"F7.wireOp",EDGE,"E272.MirrorCS");Q96=makeQuery(id+"F7.imprint","IMPRINT",FACE,{"disambiguationData":[TD([[makeQuery(id+"F7.imprint","IMPRINT",EDGE,{"derivedFrom":subQ0}),-1.0]])]});}
            var Q97;
            {var subQ0=sQuery(id+"F7.wireOp",EDGE,"E108.MirrorCS");Q97=makeQuery(id+"F7.imprint","IMPRINT",FACE,{"disambiguationData":[TD([[makeQuery(id+"F7.imprint","IMPRINT",EDGE,{"derivedFrom":subQ0}),-1.0]])]});}
            var Q98;
            {var subQ0=sQuery(id+"F7.wireOp",EDGE,"E189.MirrorCS");Q98=makeQuery(id+"F7.imprint","IMPRINT",FACE,{"disambiguationData":[TD([[makeQuery(id+"F7.imprint","IMPRINT",EDGE,{"derivedFrom":subQ0}),-1.0]])]});}
            var Q99;
            {var subQ0=sQuery(id+"F7.wireOp",EDGE,"E90.MirrorCS");Q99=makeQuery(id+"F7.imprint","IMPRINT",FACE,{"disambiguationData":[TD([[makeQuery(id+"F7.imprint","IMPRINT",EDGE,{"derivedFrom":subQ0}),-1.0]])]});}
            var Q100;
            {var subQ0=sQuery(id+"F7.wireOp",EDGE,"E247.MirrorCS");Q100=makeQuery(id+"F7.imprint","IMPRINT",FACE,{"disambiguationData":[TD([[makeQuery(id+"F7.imprint","IMPRINT",EDGE,{"derivedFrom":subQ0}),-1.0]])]});}
            var Q101;
            {var subQ0=sQuery(id+"F7.wireOp",EDGE,"E215.MirrorCS");Q101=makeQuery(id+"F7.imprint","IMPRINT",FACE,{"disambiguationData":[TD([[makeQuery(id+"F7.imprint","IMPRINT",EDGE,{"derivedFrom":subQ0}),-1.0]])]});}
            var Q102;
            {var subQ0=sQuery(id+"F7.wireOp",EDGE,"E245.MirrorCS");Q102=makeQuery(id+"F7.imprint","IMPRINT",FACE,{"disambiguationData":[TD([[makeQuery(id+"F7.imprint","IMPRINT",EDGE,{"derivedFrom":subQ0}),-1.0]])]});}
            var Q103;
            {var subQ0=sQuery(id+"F7.wireOp",EDGE,"E152.MirrorCS");Q103=makeQuery(id+"F7.imprint","IMPRINT",FACE,{"disambiguationData":[TD([[makeQuery(id+"F7.imprint","IMPRINT",EDGE,{"derivedFrom":subQ0}),1.0]])]});}
            var Q104;
            {var subQ0=sQuery(id+"F7.wireOp",EDGE,"E89.MirrorCS");Q104=makeQuery(id+"F7.imprint","IMPRINT",FACE,{"disambiguationData":[TD([[makeQuery(id+"F7.imprint","IMPRINT",EDGE,{"derivedFrom":subQ0}),1.0]])]});}
            var Q105;
            {var subQ0=sQuery(id+"F7.wireOp",EDGE,"E174.MirrorCS");Q105=makeQuery(id+"F7.imprint","IMPRINT",FACE,{"disambiguationData":[TD([[makeQuery(id+"F7.imprint","IMPRINT",EDGE,{"derivedFrom":subQ0}),1.0]])]});}
            var Q106;
            {var subQ0=sQuery(id+"F7.wireOp",EDGE,"E192.MirrorCS");Q106=makeQuery(id+"F7.imprint","IMPRINT",FACE,{"disambiguationData":[TD([[makeQuery(id+"F7.imprint","IMPRINT",EDGE,{"derivedFrom":subQ0}),1.0]])]});}
            var Q107;
            {var subQ0=sQuery(id+"F7.wireOp",EDGE,"E291.MirrorCS");Q107=makeQuery(id+"F7.imprint","IMPRINT",FACE,{"disambiguationData":[TD([[makeQuery(id+"F7.imprint","IMPRINT",EDGE,{"derivedFrom":subQ0}),1.0]])]});}
            var Q108;
            {var subQ0=sQuery(id+"F7.wireOp",EDGE,"E99.MirrorCS");Q108=makeQuery(id+"F7.imprint","IMPRINT",FACE,{"disambiguationData":[TD([[makeQuery(id+"F7.imprint","IMPRINT",EDGE,{"derivedFrom":subQ0}),1.0]])]});}
            var Q109;
            {var subQ0=sQuery(id+"F7.wireOp",EDGE,"E128.MirrorCS");Q109=makeQuery(id+"F7.imprint","IMPRINT",FACE,{"disambiguationData":[TD([[makeQuery(id+"F7.imprint","IMPRINT",EDGE,{"derivedFrom":subQ0}),-1.0]])]});}
            var Q110;
            {var subQ0=sQuery(id+"F7.wireOp",EDGE,"E200.MirrorCS");Q110=makeQuery(id+"F7.imprint","IMPRINT",FACE,{"disambiguationData":[TD([[makeQuery(id+"F7.imprint","IMPRINT",EDGE,{"derivedFrom":subQ0}),1.0]])]});}
            var Q111;
            {var subQ0=sQuery(id+"F7.wireOp",EDGE,"E246.MirrorCS");Q111=makeQuery(id+"F7.imprint","IMPRINT",FACE,{"disambiguationData":[TD([[makeQuery(id+"F7.imprint","IMPRINT",EDGE,{"derivedFrom":subQ0}),1.0]])]});}
            var Q112;
            {var subQ0=sQuery(id+"F7.wireOp",EDGE,"E284.MirrorCS");Q112=makeQuery(id+"F7.imprint","IMPRINT",FACE,{"disambiguationData":[TD([[makeQuery(id+"F7.imprint","IMPRINT",EDGE,{"derivedFrom":subQ0}),-1.0]])]});}
            var Q113;
            {var subQ0=sQuery(id+"F7.wireOp",EDGE,"E237.MirrorCS");Q113=makeQuery(id+"F7.imprint","IMPRINT",FACE,{"disambiguationData":[TD([[makeQuery(id+"F7.imprint","IMPRINT",EDGE,{"derivedFrom":subQ0}),-1.0]])]});}
            var Q114;
            {var subQ0=sQuery(id+"F7.wireOp",EDGE,"E263.MirrorCS");Q114=makeQuery(id+"F7.imprint","IMPRINT",FACE,{"disambiguationData":[TD([[makeQuery(id+"F7.imprint","IMPRINT",EDGE,{"derivedFrom":subQ0}),1.0]])]});}
            var Q115;
            {var subQ0=sQuery(id+"F7.wireOp",EDGE,"E150.MirrorCS");Q115=makeQuery(id+"F7.imprint","IMPRINT",FACE,{"disambiguationData":[TD([[makeQuery(id+"F7.imprint","IMPRINT",EDGE,{"derivedFrom":subQ0}),1.0]])]});}
            var Q116;
            {var subQ0=sQuery(id+"F7.wireOp",EDGE,"E219.MirrorCS");Q116=makeQuery(id+"F7.imprint","IMPRINT",FACE,{"disambiguationData":[TD([[makeQuery(id+"F7.imprint","IMPRINT",EDGE,{"derivedFrom":subQ0}),-1.0]])]});}
            var Q117;
            {var subQ0=sQuery(id+"F7.wireOp",EDGE,"E276.MirrorCS");Q117=makeQuery(id+"F7.imprint","IMPRINT",FACE,{"disambiguationData":[TD([[makeQuery(id+"F7.imprint","IMPRINT",EDGE,{"derivedFrom":subQ0}),-1.0]])]});}
            var Q118;
            {var subQ0=sQuery(id+"F7.wireOp",EDGE,"E87.MirrorCS");Q118=makeQuery(id+"F7.imprint","IMPRINT",FACE,{"disambiguationData":[TD([[makeQuery(id+"F7.imprint","IMPRINT",EDGE,{"derivedFrom":subQ0}),1.0]])]});}
            var Q119;
            {var subQ0=sQuery(id+"F7.wireOp",EDGE,"E112.MirrorCS");Q119=makeQuery(id+"F7.imprint","IMPRINT",FACE,{"disambiguationData":[TD([[makeQuery(id+"F7.imprint","IMPRINT",EDGE,{"derivedFrom":subQ0}),-1.0]])]});}
            var Q120;
            {var subQ0=sQuery(id+"F7.wireOp",EDGE,"E170.MirrorCS");Q120=makeQuery(id+"F7.imprint","IMPRINT",FACE,{"disambiguationData":[TD([[makeQuery(id+"F7.imprint","IMPRINT",EDGE,{"derivedFrom":subQ0}),1.0]])]});}
            var Q121;
            {var subQ0=sQuery(id+"F7.wireOp",EDGE,"E95.MirrorCS");Q121=makeQuery(id+"F7.imprint","IMPRINT",FACE,{"disambiguationData":[TD([[makeQuery(id+"F7.imprint","IMPRINT",EDGE,{"derivedFrom":subQ0}),1.0]])]});}
            var Q122;
            {var subQ0=sQuery(id+"F7.wireOp",EDGE,"E295.MirrorCS");Q122=makeQuery(id+"F7.imprint","IMPRINT",FACE,{"disambiguationData":[TD([[makeQuery(id+"F7.imprint","IMPRINT",EDGE,{"derivedFrom":subQ0}),1.0]])]});}
            var Q123;
            {var subQ0=sQuery(id+"F7.wireOp",EDGE,"E193.MirrorCS");Q123=makeQuery(id+"F7.imprint","IMPRINT",FACE,{"disambiguationData":[TD([[makeQuery(id+"F7.imprint","IMPRINT",EDGE,{"derivedFrom":subQ0}),-1.0]])]});}
            var Q124;
            {var subQ0=sQuery(id+"F7.wireOp",EDGE,"E86.MirrorCS");Q124=makeQuery(id+"F7.imprint","IMPRINT",FACE,{"disambiguationData":[TD([[makeQuery(id+"F7.imprint","IMPRINT",EDGE,{"derivedFrom":subQ0}),-1.0]])]});}
            var Q125;
            {var subQ0=sQuery(id+"F7.wireOp",EDGE,"E84.MirrorCS");Q125=makeQuery(id+"F7.imprint","IMPRINT",FACE,{"disambiguationData":[TD([[makeQuery(id+"F7.imprint","IMPRINT",EDGE,{"derivedFrom":subQ0}),-1.0]])]});}
            var Q126;
            {var subQ0=sQuery(id+"F7.wireOp",EDGE,"E268.MirrorCS");Q126=makeQuery(id+"F7.imprint","IMPRINT",FACE,{"disambiguationData":[TD([[makeQuery(id+"F7.imprint","IMPRINT",EDGE,{"derivedFrom":subQ0}),-1.0]])]});}
            var Q127;
            {var subQ0=sQuery(id+"F7.wireOp",EDGE,"E111.MirrorCS");Q127=makeQuery(id+"F7.imprint","IMPRINT",FACE,{"disambiguationData":[TD([[makeQuery(id+"F7.imprint","IMPRINT",EDGE,{"derivedFrom":subQ0}),1.0]])]});}
            var Q128;
            {var subQ0=sQuery(id+"F7.wireOp",EDGE,"E220.MirrorCS");Q128=makeQuery(id+"F7.imprint","IMPRINT",FACE,{"disambiguationData":[TD([[makeQuery(id+"F7.imprint","IMPRINT",EDGE,{"derivedFrom":subQ0}),1.0]])]});}
            var Q129;
            {var subQ0=sQuery(id+"F7.wireOp",EDGE,"E270.MirrorCS");Q129=makeQuery(id+"F7.imprint","IMPRINT",FACE,{"disambiguationData":[TD([[makeQuery(id+"F7.imprint","IMPRINT",EDGE,{"derivedFrom":subQ0}),-1.0]])]});}
            var Q130;
            {var subQ0=sQuery(id+"F7.wireOp",EDGE,"E242.MirrorCS");Q130=makeQuery(id+"F7.imprint","IMPRINT",FACE,{"disambiguationData":[TD([[makeQuery(id+"F7.imprint","IMPRINT",EDGE,{"derivedFrom":subQ0}),1.0]])]});}
            var Q131;
            {var subQ0=sQuery(id+"F7.wireOp",EDGE,"E148.MirrorCS");Q131=makeQuery(id+"F7.imprint","IMPRINT",FACE,{"disambiguationData":[TD([[makeQuery(id+"F7.imprint","IMPRINT",EDGE,{"derivedFrom":subQ0}),1.0]])]});}
            var Q132;
            {var subQ0=sQuery(id+"F7.wireOp",EDGE,"E227.MirrorCS");Q132=makeQuery(id+"F7.imprint","IMPRINT",FACE,{"disambiguationData":[TD([[makeQuery(id+"F7.imprint","IMPRINT",EDGE,{"derivedFrom":subQ0}),-1.0]])]});}
            var Q133;
            {var subQ0=sQuery(id+"F7.wireOp",EDGE,"E287.MirrorCS");Q133=makeQuery(id+"F7.imprint","IMPRINT",FACE,{"disambiguationData":[TD([[makeQuery(id+"F7.imprint","IMPRINT",EDGE,{"derivedFrom":subQ0}),1.0]])]});}
            var Q134;
            {var subQ0=sQuery(id+"F7.wireOp",EDGE,"E127.MirrorCS");Q134=makeQuery(id+"F7.imprint","IMPRINT",FACE,{"disambiguationData":[TD([[makeQuery(id+"F7.imprint","IMPRINT",EDGE,{"derivedFrom":subQ0}),1.0]])]});}
            var Q135;
            {var subQ0=sQuery(id+"F7.wireOp",EDGE,"E142.MirrorCS");Q135=makeQuery(id+"F7.imprint","IMPRINT",FACE,{"disambiguationData":[TD([[makeQuery(id+"F7.imprint","IMPRINT",EDGE,{"derivedFrom":subQ0}),-1.0]])]});}
            var Q136;
            {var subQ0=sQuery(id+"F7.wireOp",EDGE,"E126.MirrorCS");Q136=makeQuery(id+"F7.imprint","IMPRINT",FACE,{"disambiguationData":[TD([[makeQuery(id+"F7.imprint","IMPRINT",EDGE,{"derivedFrom":subQ0}),-1.0]])]});}
            var Q137;
            {var subQ0=sQuery(id+"F7.wireOp",EDGE,"E117.MirrorCS");Q137=makeQuery(id+"F7.imprint","IMPRINT",FACE,{"disambiguationData":[TD([[makeQuery(id+"F7.imprint","IMPRINT",EDGE,{"derivedFrom":subQ0}),1.0]])]});}
            var Q138;
            {var subQ0=sQuery(id+"F7.wireOp",EDGE,"E177.MirrorCS");Q138=makeQuery(id+"F7.imprint","IMPRINT",FACE,{"disambiguationData":[TD([[makeQuery(id+"F7.imprint","IMPRINT",EDGE,{"derivedFrom":subQ0}),-1.0]])]});}
            var Q139;
            {var subQ0=sQuery(id+"F7.wireOp",EDGE,"E243.MirrorCS");Q139=makeQuery(id+"F7.imprint","IMPRINT",FACE,{"disambiguationData":[TD([[makeQuery(id+"F7.imprint","IMPRINT",EDGE,{"derivedFrom":subQ0}),-1.0]])]});}
            var Q140;
            {var subQ0=sQuery(id+"F7.wireOp",EDGE,"E203.MirrorCS");Q140=makeQuery(id+"F7.imprint","IMPRINT",FACE,{"disambiguationData":[TD([[makeQuery(id+"F7.imprint","IMPRINT",EDGE,{"derivedFrom":subQ0}),-1.0]])]});}
            var Q141;
            {var subQ0=sQuery(id+"F7.wireOp",EDGE,"E101.MirrorCS");Q141=makeQuery(id+"F7.imprint","IMPRINT",FACE,{"disambiguationData":[TD([[makeQuery(id+"F7.imprint","IMPRINT",EDGE,{"derivedFrom":subQ0}),1.0]])]});}
            var Q142;
            {var subQ0=sQuery(id+"F7.wireOp",EDGE,"E269.MirrorCS");Q142=makeQuery(id+"F7.imprint","IMPRINT",FACE,{"disambiguationData":[TD([[makeQuery(id+"F7.imprint","IMPRINT",EDGE,{"derivedFrom":subQ0}),1.0]])]});}
            var Q143;
            {var subQ0=sQuery(id+"F7.wireOp",EDGE,"E168.MirrorCS");Q143=makeQuery(id+"F7.imprint","IMPRINT",FACE,{"disambiguationData":[TD([[makeQuery(id+"F7.imprint","IMPRINT",EDGE,{"derivedFrom":subQ0}),1.0]])]});}
            var Q144;
            {var subQ0=sQuery(id+"F7.wireOp",EDGE,"E178.MirrorCS");Q144=makeQuery(id+"F7.imprint","IMPRINT",FACE,{"disambiguationData":[TD([[makeQuery(id+"F7.imprint","IMPRINT",EDGE,{"derivedFrom":subQ0}),1.0]])]});}
            var Q145;
            {var subQ0=sQuery(id+"F7.wireOp",EDGE,"E102.MirrorCS");Q145=makeQuery(id+"F7.imprint","IMPRINT",FACE,{"disambiguationData":[TD([[makeQuery(id+"F7.imprint","IMPRINT",EDGE,{"derivedFrom":subQ0}),-1.0]])]});}
            var Q146;
            {var subQ0=sQuery(id+"F7.wireOp",EDGE,"E103.MirrorCS");Q146=makeQuery(id+"F7.imprint","IMPRINT",FACE,{"disambiguationData":[TD([[makeQuery(id+"F7.imprint","IMPRINT",EDGE,{"derivedFrom":subQ0}),1.0]])]});}
            var Q147;
            {var subQ0=sQuery(id+"F7.wireOp",EDGE,"E228.MirrorCS");Q147=makeQuery(id+"F7.imprint","IMPRINT",FACE,{"disambiguationData":[TD([[makeQuery(id+"F7.imprint","IMPRINT",EDGE,{"derivedFrom":subQ0}),1.0]])]});}
            var Q148;
            {var subQ0=sQuery(id+"F7.wireOp",EDGE,"E210.MirrorCS");Q148=makeQuery(id+"F7.imprint","IMPRINT",FACE,{"disambiguationData":[TD([[makeQuery(id+"F7.imprint","IMPRINT",EDGE,{"derivedFrom":subQ0}),1.0]])]});}
            var Q149;
            {var subQ0=sQuery(id+"F7.wireOp",EDGE,"E293.MirrorCS");Q149=makeQuery(id+"F7.imprint","IMPRINT",FACE,{"disambiguationData":[TD([[makeQuery(id+"F7.imprint","IMPRINT",EDGE,{"derivedFrom":subQ0}),1.0]])]});}
            var Q150;
            {var subQ0=sQuery(id+"F7.wireOp",EDGE,"E217.MirrorCS");Q150=makeQuery(id+"F7.imprint","IMPRINT",FACE,{"disambiguationData":[TD([[makeQuery(id+"F7.imprint","IMPRINT",EDGE,{"derivedFrom":subQ0}),-1.0]])]});}
            var Q151;
            {var subQ0=sQuery(id+"F7.wireOp",EDGE,"E161.MirrorCS");Q151=makeQuery(id+"F7.imprint","IMPRINT",FACE,{"disambiguationData":[TD([[makeQuery(id+"F7.imprint","IMPRINT",EDGE,{"derivedFrom":subQ0}),-1.0]])]});}
            var Q152;
            {var subQ0=sQuery(id+"F7.wireOp",EDGE,"E194.MirrorCS");Q152=makeQuery(id+"F7.imprint","IMPRINT",FACE,{"disambiguationData":[TD([[makeQuery(id+"F7.imprint","IMPRINT",EDGE,{"derivedFrom":subQ0}),1.0]])]});}
            var Q153;
            {var subQ0=sQuery(id+"F7.wireOp",EDGE,"E251.MirrorCS");Q153=makeQuery(id+"F7.imprint","IMPRINT",FACE,{"disambiguationData":[TD([[makeQuery(id+"F7.imprint","IMPRINT",EDGE,{"derivedFrom":subQ0}),-1.0]])]});}
            var Q154;
            {var subQ0=sQuery(id+"F7.wireOp",EDGE,"E218.MirrorCS");Q154=makeQuery(id+"F7.imprint","IMPRINT",FACE,{"disambiguationData":[TD([[makeQuery(id+"F7.imprint","IMPRINT",EDGE,{"derivedFrom":subQ0}),1.0]])]});}
            var Q155;
            {var subQ0=sQuery(id+"F7.wireOp",EDGE,"E176.MirrorCS");Q155=makeQuery(id+"F7.imprint","IMPRINT",FACE,{"disambiguationData":[TD([[makeQuery(id+"F7.imprint","IMPRINT",EDGE,{"derivedFrom":subQ0}),1.0]])]});}
            var Q156;
            {var subQ0=sQuery(id+"F7.wireOp",EDGE,"E271.MirrorCS");Q156=makeQuery(id+"F7.imprint","IMPRINT",FACE,{"disambiguationData":[TD([[makeQuery(id+"F7.imprint","IMPRINT",EDGE,{"derivedFrom":subQ0}),1.0]])]});}
            var Q157;
            {var subQ0=sQuery(id+"F7.wireOp",EDGE,"E233.MirrorCS");Q157=makeQuery(id+"F7.imprint","IMPRINT",FACE,{"disambiguationData":[TD([[makeQuery(id+"F7.imprint","IMPRINT",EDGE,{"derivedFrom":subQ0}),-1.0]])]});}
            var Q158;
            {var subQ0=sQuery(id+"F7.wireOp",EDGE,"E249.MirrorCS");Q158=makeQuery(id+"F7.imprint","IMPRINT",FACE,{"disambiguationData":[TD([[makeQuery(id+"F7.imprint","IMPRINT",EDGE,{"derivedFrom":subQ0}),-1.0]])]});}
            var Q159;
            {var subQ0=sQuery(id+"F7.wireOp",EDGE,"E134.MirrorCS");Q159=makeQuery(id+"F7.imprint","IMPRINT",FACE,{"disambiguationData":[TD([[makeQuery(id+"F7.imprint","IMPRINT",EDGE,{"derivedFrom":subQ0}),-1.0]])]});}
            var Q160;
            {var subQ0=sQuery(id+"F7.wireOp",EDGE,"E132.MirrorCS");Q160=makeQuery(id+"F7.imprint","IMPRINT",FACE,{"disambiguationData":[TD([[makeQuery(id+"F7.imprint","IMPRINT",EDGE,{"derivedFrom":subQ0}),-1.0]])]});}
            var Q161;
            {var subQ2=sQuery(id+"F7.wireOp",EDGE,"E195.MirrorCS");Q161=makeQuery(id+"F7.imprint","IMPRINT",FACE,{"disambiguationData":[TD([[makeQuery(id+"F7.imprint","IMPRINT",EDGE,{"derivedFrom":subQ2}),-1.0]])]});}
            var Q162;
            {var subQ0=sQuery(id+"F7.wireOp",EDGE,"E301.MirrorCS");Q162=makeQuery(id+"F7.imprint","IMPRINT",FACE,{"disambiguationData":[TD([[makeQuery(id+"F7.imprint","IMPRINT",EDGE,{"derivedFrom":subQ0}),1.0]])]});}
            var Q163;
            {var subQ0=sQuery(id+"F7.wireOp",EDGE,"E209.MirrorCS");Q163=makeQuery(id+"F7.imprint","IMPRINT",FACE,{"disambiguationData":[TD([[makeQuery(id+"F7.imprint","IMPRINT",EDGE,{"derivedFrom":subQ0}),-1.0]])]});}
            var Q164;
            {var subQ0=sQuery(id+"F7.wireOp",EDGE,"E257.MirrorCS");Q164=makeQuery(id+"F7.imprint","IMPRINT",FACE,{"disambiguationData":[TD([[makeQuery(id+"F7.imprint","IMPRINT",EDGE,{"derivedFrom":subQ0}),-1.0]])]});}
            var Q165;
            {var subQ0=sQuery(id+"F7.wireOp",EDGE,"E187.MirrorCS");Q165=makeQuery(id+"F7.imprint","IMPRINT",FACE,{"disambiguationData":[TD([[makeQuery(id+"F7.imprint","IMPRINT",EDGE,{"derivedFrom":subQ0}),-1.0]])]});}
            var Q166;
            {var subQ0=sQuery(id+"F7.wireOp",EDGE,"E212.MirrorCS");Q166=makeQuery(id+"F7.imprint","IMPRINT",FACE,{"disambiguationData":[TD([[makeQuery(id+"F7.imprint","IMPRINT",EDGE,{"derivedFrom":subQ0}),1.0]])]});}
            var Q167;
            {var subQ0=sQuery(id+"F7.wireOp",EDGE,"E133.MirrorCS");Q167=makeQuery(id+"F7.imprint","IMPRINT",FACE,{"disambiguationData":[TD([[makeQuery(id+"F7.imprint","IMPRINT",EDGE,{"derivedFrom":subQ0}),1.0]])]});}
            var Q168;
            {var subQ0=sQuery(id+"F7.wireOp",EDGE,"E155.MirrorCS");Q168=makeQuery(id+"F7.imprint","IMPRINT",FACE,{"disambiguationData":[TD([[makeQuery(id+"F7.imprint","IMPRINT",EDGE,{"derivedFrom":subQ0}),-1.0]])]});}
            var Q169;
            {var subQ0=sQuery(id+"F7.wireOp",EDGE,"E225.MirrorCS");Q169=makeQuery(id+"F7.imprint","IMPRINT",FACE,{"disambiguationData":[TD([[makeQuery(id+"F7.imprint","IMPRINT",EDGE,{"derivedFrom":subQ0}),-1.0]])]});}
            var Q170;
            {var subQ0=sQuery(id+"F7.wireOp",EDGE,"E135.MirrorCS");Q170=makeQuery(id+"F7.imprint","IMPRINT",FACE,{"disambiguationData":[TD([[makeQuery(id+"F7.imprint","IMPRINT",EDGE,{"derivedFrom":subQ0}),1.0]])]});}
            var Q171;
            {var subQ0=sQuery(id+"F7.wireOp",EDGE,"E196.MirrorCS");Q171=makeQuery(id+"F7.imprint","IMPRINT",FACE,{"disambiguationData":[TD([[makeQuery(id+"F7.imprint","IMPRINT",EDGE,{"derivedFrom":subQ0}),1.0]])]});}
            var Q172;
            {var subQ0=sQuery(id+"F7.wireOp",EDGE,"E250.MirrorCS");Q172=makeQuery(id+"F7.imprint","IMPRINT",FACE,{"disambiguationData":[TD([[makeQuery(id+"F7.imprint","IMPRINT",EDGE,{"derivedFrom":subQ0}),1.0]])]});}
            var Q173;
            {var subQ0=sQuery(id+"F7.wireOp",EDGE,"E94.MirrorCS");Q173=makeQuery(id+"F7.imprint","IMPRINT",FACE,{"disambiguationData":[TD([[makeQuery(id+"F7.imprint","IMPRINT",EDGE,{"derivedFrom":subQ0}),-1.0]])]});}
            var Q174;
            {var subQ0=sQuery(id+"F7.wireOp",EDGE,"E149.MirrorCS");Q174=makeQuery(id+"F7.imprint","IMPRINT",FACE,{"disambiguationData":[TD([[makeQuery(id+"F7.imprint","IMPRINT",EDGE,{"derivedFrom":subQ0}),-1.0]])]});}
            var Q175;
            {var subQ0=sQuery(id+"F7.wireOp",EDGE,"E211.MirrorCS");Q175=makeQuery(id+"F7.imprint","IMPRINT",FACE,{"disambiguationData":[TD([[makeQuery(id+"F7.imprint","IMPRINT",EDGE,{"derivedFrom":subQ0}),-1.0]])]});}
            var Q176;
            {var subQ0=sQuery(id+"F7.wireOp",EDGE,"E279.MirrorCS");Q176=makeQuery(id+"F7.imprint","IMPRINT",FACE,{"disambiguationData":[TD([[makeQuery(id+"F7.imprint","IMPRINT",EDGE,{"derivedFrom":subQ0}),1.0]])]});}
            var Q177;
            {var subQ0=sQuery(id+"F7.wireOp",EDGE,"E278.MirrorCS");Q177=makeQuery(id+"F7.imprint","IMPRINT",FACE,{"disambiguationData":[TD([[makeQuery(id+"F7.imprint","IMPRINT",EDGE,{"derivedFrom":subQ0}),-1.0]])]});}
            var Q178;
            {var subQ0=sQuery(id+"F7.wireOp",EDGE,"E124.MirrorCS");Q178=makeQuery(id+"F7.imprint","IMPRINT",FACE,{"disambiguationData":[TD([[makeQuery(id+"F7.imprint","IMPRINT",EDGE,{"derivedFrom":subQ0}),-1.0]])]});}
            var Q179;
            {var subQ0=sQuery(id+"F7.wireOp",EDGE,"E142.MirrorCS");Q179=makeQuery(id+"F7.imprint","IMPRINT",FACE,{"disambiguationData":[TD([[makeQuery(id+"F7.imprint","IMPRINT",EDGE,{"derivedFrom":subQ0}),1.0]])]});}
            var Q180;
            {var subQ0=sQuery(id+"F7.wireOp",EDGE,"E188.MirrorCS");Q180=makeQuery(id+"F7.imprint","IMPRINT",FACE,{"disambiguationData":[TD([[makeQuery(id+"F7.imprint","IMPRINT",EDGE,{"derivedFrom":subQ0}),1.0]])]});}
            var Q181;
            {var subQ0=sQuery(id+"F7.wireOp",EDGE,"E202.MirrorCS");Q181=makeQuery(id+"F7.imprint","IMPRINT",FACE,{"disambiguationData":[TD([[makeQuery(id+"F7.imprint","IMPRINT",EDGE,{"derivedFrom":subQ0}),1.0]])]});}
            var Q182;
            {var subQ0=sQuery(id+"F7.wireOp",EDGE,"E186.MirrorCS");Q182=makeQuery(id+"F7.imprint","IMPRINT",FACE,{"disambiguationData":[TD([[makeQuery(id+"F7.imprint","IMPRINT",EDGE,{"derivedFrom":subQ0}),1.0]])]});}
            var Q183;
            {var subQ0=sQuery(id+"F7.wireOp",EDGE,"E162.MirrorCS");Q183=makeQuery(id+"F7.imprint","IMPRINT",FACE,{"disambiguationData":[TD([[makeQuery(id+"F7.imprint","IMPRINT",EDGE,{"derivedFrom":subQ0}),1.0]])]});}
            var Q184;
            {var subQ0=sQuery(id+"F7.wireOp",EDGE,"E235.MirrorCS");Q184=makeQuery(id+"F7.imprint","IMPRINT",FACE,{"disambiguationData":[TD([[makeQuery(id+"F7.imprint","IMPRINT",EDGE,{"derivedFrom":subQ0}),-1.0]])]});}
            var Q185;
            {var subQ0=sQuery(id+"F7.wireOp",EDGE,"E84.MirrorCS");Q185=makeQuery(id+"F7.imprint","IMPRINT",FACE,{"disambiguationData":[TD([[makeQuery(id+"F7.imprint","IMPRINT",EDGE,{"derivedFrom":subQ0}),1.0]])]});}
            var Q186;
            {var subQ0=sQuery(id+"F7.wireOp",EDGE,"E118.MirrorCS");Q186=makeQuery(id+"F7.imprint","IMPRINT",FACE,{"disambiguationData":[TD([[makeQuery(id+"F7.imprint","IMPRINT",EDGE,{"derivedFrom":subQ0}),-1.0]])]});}
            var Q187;
            {var subQ0=sQuery(id+"F7.wireOp",EDGE,"E147.MirrorCS");Q187=makeQuery(id+"F7.imprint","IMPRINT",FACE,{"disambiguationData":[TD([[makeQuery(id+"F7.imprint","IMPRINT",EDGE,{"derivedFrom":subQ0}),-1.0]])]});}
            var Q188;
            {var subQ0=sQuery(id+"F7.wireOp",EDGE,"E226.MirrorCS");Q188=makeQuery(id+"F7.imprint","IMPRINT",FACE,{"disambiguationData":[TD([[makeQuery(id+"F7.imprint","IMPRINT",EDGE,{"derivedFrom":subQ0}),1.0]])]});}
            var Q189;
            {var subQ0=sQuery(id+"F7.wireOp",EDGE,"E110.MirrorCS");Q189=makeQuery(id+"F7.imprint","IMPRINT",FACE,{"disambiguationData":[TD([[makeQuery(id+"F7.imprint","IMPRINT",EDGE,{"derivedFrom":subQ0}),-1.0]])]});}
            var Q190;
            {var subQ0=sQuery(id+"F7.wireOp",EDGE,"E201.MirrorCS");Q190=makeQuery(id+"F7.imprint","IMPRINT",FACE,{"disambiguationData":[TD([[makeQuery(id+"F7.imprint","IMPRINT",EDGE,{"derivedFrom":subQ0}),-1.0]])]});}
            var Q191;
            {var subQ0=sQuery(id+"F7.wireOp",EDGE,"E252.MirrorCS");Q191=makeQuery(id+"F7.imprint","IMPRINT",FACE,{"disambiguationData":[TD([[makeQuery(id+"F7.imprint","IMPRINT",EDGE,{"derivedFrom":subQ0}),1.0]])]});}
            var Q192;
            {var subQ0=sQuery(id+"F7.wireOp",EDGE,"E296.MirrorCS");Q192=makeQuery(id+"F7.imprint","IMPRINT",FACE,{"disambiguationData":[TD([[makeQuery(id+"F7.imprint","IMPRINT",EDGE,{"derivedFrom":subQ0}),-1.0]])]});}
            var Q193;
            {var subQ0=sQuery(id+"F7.wireOp",EDGE,"E104.MirrorCS");Q193=makeQuery(id+"F7.imprint","IMPRINT",FACE,{"disambiguationData":[TD([[makeQuery(id+"F7.imprint","IMPRINT",EDGE,{"derivedFrom":subQ0}),-1.0]])]});}
            var Q194;
            {var subQ0=sQuery(id+"F7.wireOp",EDGE,"E96.MirrorCS");Q194=makeQuery(id+"F7.imprint","IMPRINT",FACE,{"disambiguationData":[TD([[makeQuery(id+"F7.imprint","IMPRINT",EDGE,{"derivedFrom":subQ0}),-1.0]])]});}
            var Q195;
            {var subQ0=sQuery(id+"F7.wireOp",EDGE,"E302.MirrorCS");Q195=makeQuery(id+"F7.imprint","IMPRINT",FACE,{"disambiguationData":[TD([[makeQuery(id+"F7.imprint","IMPRINT",EDGE,{"derivedFrom":subQ0}),-1.0]])]});}
            var Q196;
            {var subQ0=sQuery(id+"F7.wireOp",EDGE,"E179.MirrorCS");Q196=makeQuery(id+"F7.imprint","IMPRINT",FACE,{"disambiguationData":[TD([[makeQuery(id+"F7.imprint","IMPRINT",EDGE,{"derivedFrom":subQ0}),-1.0]])]});}
            var Q197;
            {var subQ0=sQuery(id+"F7.wireOp",EDGE,"E185.MirrorCS");Q197=makeQuery(id+"F7.imprint","IMPRINT",FACE,{"disambiguationData":[TD([[makeQuery(id+"F7.imprint","IMPRINT",EDGE,{"derivedFrom":subQ0}),-1.0]])]});}
            var Q198;
            {var subQ0=sQuery(id+"F7.wireOp",EDGE,"E169.MirrorCS");Q198=makeQuery(id+"F7.imprint","IMPRINT",FACE,{"disambiguationData":[TD([[makeQuery(id+"F7.imprint","IMPRINT",EDGE,{"derivedFrom":subQ0}),-1.0]])]});}
            var Q199;
            {var subQ0=sQuery(id+"F7.wireOp",EDGE,"E125.MirrorCS");Q199=makeQuery(id+"F7.imprint","IMPRINT",FACE,{"disambiguationData":[TD([[makeQuery(id+"F7.imprint","IMPRINT",EDGE,{"derivedFrom":subQ0}),1.0]])]});}
            var Q200;
            {var subQ0=sQuery(id+"F7.wireOp",EDGE,"E156.MirrorCS");Q200=makeQuery(id+"F7.imprint","IMPRINT",FACE,{"disambiguationData":[TD([[makeQuery(id+"F7.imprint","IMPRINT",EDGE,{"derivedFrom":subQ0}),1.0]])]});}
            var Q201;
            {var subQ0=sQuery(id+"F7.wireOp",EDGE,"E204.MirrorCS");Q201=makeQuery(id+"F7.imprint","IMPRINT",FACE,{"disambiguationData":[TD([[makeQuery(id+"F7.imprint","IMPRINT",EDGE,{"derivedFrom":subQ0}),1.0]])]});}
            var Q202;
            {var subQ0=sQuery(id+"F7.wireOp",EDGE,"E241.MirrorCS");Q202=makeQuery(id+"F7.imprint","IMPRINT",FACE,{"disambiguationData":[TD([[makeQuery(id+"F7.imprint","IMPRINT",EDGE,{"derivedFrom":subQ0}),-1.0]])]});}
            var Q203;
            {var subQ0=sQuery(id+"F7.wireOp",EDGE,"E285.MirrorCS");Q203=makeQuery(id+"F7.imprint","IMPRINT",FACE,{"disambiguationData":[TD([[makeQuery(id+"F7.imprint","IMPRINT",EDGE,{"derivedFrom":subQ0}),1.0]])]});}
            var Q204;
            {var subQ0=sQuery(id+"F7.wireOp",EDGE,"E109.MirrorCS");Q204=makeQuery(id+"F7.imprint","IMPRINT",FACE,{"disambiguationData":[TD([[makeQuery(id+"F7.imprint","IMPRINT",EDGE,{"derivedFrom":subQ0}),1.0]])]});}
            var Q205;
            {var subQ0=sQuery(id+"F7.wireOp",EDGE,"E93.MirrorCS");Q205=makeQuery(id+"F7.imprint","IMPRINT",FACE,{"disambiguationData":[TD([[makeQuery(id+"F7.imprint","IMPRINT",EDGE,{"derivedFrom":subQ0}),1.0]])]});}
            var Q206;
            {var subQ0=sQuery(id+"F7.wireOp",EDGE,"E277.MirrorCS");Q206=makeQuery(id+"F7.imprint","IMPRINT",FACE,{"disambiguationData":[TD([[makeQuery(id+"F7.imprint","IMPRINT",EDGE,{"derivedFrom":subQ0}),1.0]])]});}
            var Q207;
            {var subQ0=sQuery(id+"F7.wireOp",EDGE,"E244.MirrorCS");Q207=makeQuery(id+"F7.imprint","IMPRINT",FACE,{"disambiguationData":[TD([[makeQuery(id+"F7.imprint","IMPRINT",EDGE,{"derivedFrom":subQ0}),1.0]])]});}
            var Q208;
            {var subQ0=sQuery(id+"F7.wireOp",EDGE,"E234.MirrorCS");Q208=makeQuery(id+"F7.imprint","IMPRINT",FACE,{"disambiguationData":[TD([[makeQuery(id+"F7.imprint","IMPRINT",EDGE,{"derivedFrom":subQ0}),1.0]])]});}
            var Q209;
            {var subQ0=sQuery(id+"F7.wireOp",EDGE,"E163.MirrorCS");Q209=makeQuery(id+"F7.imprint","IMPRINT",FACE,{"disambiguationData":[TD([[makeQuery(id+"F7.imprint","IMPRINT",EDGE,{"derivedFrom":subQ0}),-1.0]])]});}
            var Q210;
            {var subQ0=sQuery(id+"F7.wireOp",EDGE,"E258.MirrorCS");Q210=makeQuery(id+"F7.imprint","IMPRINT",FACE,{"disambiguationData":[TD([[makeQuery(id+"F7.imprint","IMPRINT",EDGE,{"derivedFrom":subQ0}),1.0]])]});}
            var Q211;
            {var subQ0=sQuery(id+"F7.wireOp",EDGE,"E262.MirrorCS");Q211=makeQuery(id+"F7.imprint","IMPRINT",FACE,{"disambiguationData":[TD([[makeQuery(id+"F7.imprint","IMPRINT",EDGE,{"derivedFrom":subQ0}),-1.0]])]});}
            var Q212;
            {var subQ0=sQuery(id+"F7.wireOp",EDGE,"E286.MirrorCS");Q212=makeQuery(id+"F7.imprint","IMPRINT",FACE,{"disambiguationData":[TD([[makeQuery(id+"F7.imprint","IMPRINT",EDGE,{"derivedFrom":subQ0}),-1.0]])]});}
            var Q213;
            {var subQ0=sQuery(id+"F7.wireOp",EDGE,"E160.MirrorCS");Q213=makeQuery(id+"F7.imprint","IMPRINT",FACE,{"disambiguationData":[TD([[makeQuery(id+"F7.imprint","IMPRINT",EDGE,{"derivedFrom":subQ0}),1.0]])]});}
            var Q214;
            {var subQ0=sQuery(id+"F7.wireOp",EDGE,"E294.MirrorCS");Q214=makeQuery(id+"F7.imprint","IMPRINT",FACE,{"disambiguationData":[TD([[makeQuery(id+"F7.imprint","IMPRINT",EDGE,{"derivedFrom":subQ0}),-1.0]])]});}
            var Q215;
            {var subQ0=sQuery(id+"F7.wireOp",EDGE,"E171.MirrorCS");Q215=makeQuery(id+"F7.imprint","IMPRINT",FACE,{"disambiguationData":[TD([[makeQuery(id+"F7.imprint","IMPRINT",EDGE,{"derivedFrom":subQ0}),-1.0]])]});}
            var Q216;
            {var subQ0=sQuery(id+"F7.wireOp",EDGE,"E236.MirrorCS");Q216=makeQuery(id+"F7.imprint","IMPRINT",FACE,{"disambiguationData":[TD([[makeQuery(id+"F7.imprint","IMPRINT",EDGE,{"derivedFrom":subQ0}),1.0]])]});}
            var Q217;
            {var subQ0=sQuery(id+"F7.wireOp",EDGE,"E260.MirrorCS");Q217=makeQuery(id+"F7.imprint","IMPRINT",FACE,{"disambiguationData":[TD([[makeQuery(id+"F7.imprint","IMPRINT",EDGE,{"derivedFrom":subQ0}),-1.0]])]});}
            var Q218;
            {var subQ13=sQuery(id+"F7.wireOp",EDGE,"E119.bottom");Q218=makeQuery(id+"F7.imprint","IMPRINT",FACE,{"disambiguationData":[TD([[makeQuery(id+"F7.imprint","IMPRINT",EDGE,{"derivedFrom":subQ13}),-1.0]])]});}
            var Q219;
            {var subQ0=sQuery(id+"F7.wireOp",EDGE,"E141.MirrorCS");Q219=makeQuery(id+"F7.imprint","IMPRINT",FACE,{"disambiguationData":[TD([[makeQuery(id+"F7.imprint","IMPRINT",EDGE,{"derivedFrom":subQ0}),1.0]])]});}
            var Q220;
            {var subQ154=sQuery(id+"F7.wireOp",EDGE,"E82.bottom");Q220=makeQuery(id+"F7.imprint","IMPRINT",FACE,{"disambiguationData":[TD([[makeQuery(id+"F7.imprint","IMPRINT",EDGE,{"derivedFrom":subQ154}),1.0]])]});}
            var Q221;
            {var subQ0=sQuery(id+"F7.wireOp",EDGE,"E261.MirrorCS");Q221=makeQuery(id+"F7.imprint","IMPRINT",FACE,{"disambiguationData":[TD([[makeQuery(id+"F7.imprint","IMPRINT",EDGE,{"derivedFrom":subQ0}),1.0]])]});}
            var Q222;
            {var subQ0=sQuery(id+"F7.wireOp",EDGE,"E140.MirrorCS");Q222=makeQuery(id+"F7.imprint","IMPRINT",FACE,{"disambiguationData":[TD([[makeQuery(id+"F7.imprint","IMPRINT",EDGE,{"derivedFrom":subQ0}),-1.0]])]});}
            var Q223;
            {var subQ0=sQuery(id+"F7.wireOp",EDGE,"E304.MirrorCS");Q223=makeQuery(id+"F7.imprint","IMPRINT",FACE,{"disambiguationData":[TD([[makeQuery(id+"F7.imprint","IMPRINT",EDGE,{"derivedFrom":subQ0}),1.0]])]});}
            extrude(context, id + "F9", {"entities" : qUnion([Q0, Q1, Q2, Q3, Q4, Q5, Q6, Q7, Q8, Q9, Q10, Q11, Q12, Q13, Q14, Q15, Q16, Q17, Q18, Q19, Q20, Q21, Q22, Q23, Q24, Q25, Q26, Q27, Q28, Q29, Q30, Q31, Q32, Q33, Q34, Q35, Q36, Q37, Q38, Q39, Q40, Q41, Q42, Q43, Q44, Q45, Q46, Q47, Q48, Q49, Q50, Q51, Q52, Q53, Q54, Q55, Q56, Q57, Q58, Q59, Q60, Q61, Q62, Q63, Q64, Q65, Q66, Q67, Q68, Q69, Q70, Q71, Q72, Q73, Q74, Q75, Q76, Q77, Q78, Q79, Q80, Q81, Q82, Q83, Q84, Q85, Q86, Q87, Q88, Q89, Q90, Q91, Q92, Q93, Q94, Q95, Q96, Q97, Q98, Q99, Q100, Q101, Q102, Q103, Q104, Q105, Q106, Q107, Q108, Q109, Q110, Q111, Q112, Q113, Q114, Q115, Q116, Q117, Q118, Q119, Q120, Q121, Q122, Q123, Q124, Q125, Q126, Q127, Q128, Q129, Q130, Q131, Q132, Q133, Q134, Q135, Q136, Q137, Q138, Q139, Q140, Q141, Q142, Q143, Q144, Q145, Q146, Q147, Q148, Q149, Q150, Q151, Q152, Q153, Q154, Q155, Q156, Q157, Q158, Q159, Q160, Q161, Q162, Q163, Q164, Q165, Q166, Q167, Q168, Q169, Q170, Q171, Q172, Q173, Q174, Q175, Q176, Q177, Q178, Q179, Q180, Q181, Q182, Q183, Q184, Q185, Q186, Q187, Q188, Q189, Q190, Q191, Q192, Q193, Q194, Q195, Q196, Q197, Q198, Q199, Q200, Q201, Q202, Q203, Q204, Q205, Q206, Q207, Q208, Q209, Q210, Q211, Q212, Q213, Q214, Q215, Q216, Q217, Q218, Q219, Q220, Q221, Q222, Q223]), "depth" : 3 * mm, "offsetDistance" : 25 * mm});
        }
        {
            var Q0;
            {var subQ0=sQuery(id+"F7.wireOp",EDGE,"E81");Q0=makeQuery(id+"F7.imprint","IMPRINT",FACE,{"disambiguationData":[TD([[makeQuery(id+"F7.imprint","IMPRINT",EDGE,{"derivedFrom":subQ0}),-1.0]])]});}
            var Q1;
            {var subQ0=sQuery(id+"F7.wireOp",EDGE,"E84.MirrorCS");Q1=makeQuery(id+"F7.imprint","IMPRINT",FACE,{"disambiguationData":[TD([[makeQuery(id+"F7.imprint","IMPRINT",EDGE,{"derivedFrom":subQ0}),-1.0]])]});}
            var Q2;
            {var subQ0=sQuery(id+"F7.wireOp",EDGE,"E86.MirrorCS");Q2=makeQuery(id+"F7.imprint","IMPRINT",FACE,{"disambiguationData":[TD([[makeQuery(id+"F7.imprint","IMPRINT",EDGE,{"derivedFrom":subQ0}),-1.0]])]});}
            var Q3;
            {var subQ0=sQuery(id+"F7.wireOp",EDGE,"E88.MirrorCS");Q3=makeQuery(id+"F7.imprint","IMPRINT",FACE,{"disambiguationData":[TD([[makeQuery(id+"F7.imprint","IMPRINT",EDGE,{"derivedFrom":subQ0}),-1.0]])]});}
            var Q4;
            {var subQ0=sQuery(id+"F7.wireOp",EDGE,"E90.MirrorCS");Q4=makeQuery(id+"F7.imprint","IMPRINT",FACE,{"disambiguationData":[TD([[makeQuery(id+"F7.imprint","IMPRINT",EDGE,{"derivedFrom":subQ0}),-1.0]])]});}
            var Q5;
            {var subQ0=sQuery(id+"F7.wireOp",EDGE,"E92.MirrorCS");Q5=makeQuery(id+"F7.imprint","IMPRINT",FACE,{"disambiguationData":[TD([[makeQuery(id+"F7.imprint","IMPRINT",EDGE,{"derivedFrom":subQ0}),-1.0]])]});}
            var Q6;
            {var subQ0=sQuery(id+"F7.wireOp",EDGE,"E94.MirrorCS");Q6=makeQuery(id+"F7.imprint","IMPRINT",FACE,{"disambiguationData":[TD([[makeQuery(id+"F7.imprint","IMPRINT",EDGE,{"derivedFrom":subQ0}),-1.0]])]});}
            var Q7;
            {var subQ0=sQuery(id+"F7.wireOp",EDGE,"E96.MirrorCS");Q7=makeQuery(id+"F7.imprint","IMPRINT",FACE,{"disambiguationData":[TD([[makeQuery(id+"F7.imprint","IMPRINT",EDGE,{"derivedFrom":subQ0}),-1.0]])]});}
            var Q8;
            {var subQ0=sQuery(id+"F7.wireOp",EDGE,"E98.MirrorCS");Q8=makeQuery(id+"F7.imprint","IMPRINT",FACE,{"disambiguationData":[TD([[makeQuery(id+"F7.imprint","IMPRINT",EDGE,{"derivedFrom":subQ0}),-1.0]])]});}
            var Q9;
            {var subQ0=sQuery(id+"F7.wireOp",EDGE,"E100.MirrorCS");Q9=makeQuery(id+"F7.imprint","IMPRINT",FACE,{"disambiguationData":[TD([[makeQuery(id+"F7.imprint","IMPRINT",EDGE,{"derivedFrom":subQ0}),-1.0]])]});}
            var Q10;
            {var subQ0=sQuery(id+"F7.wireOp",EDGE,"E102.MirrorCS");Q10=makeQuery(id+"F7.imprint","IMPRINT",FACE,{"disambiguationData":[TD([[makeQuery(id+"F7.imprint","IMPRINT",EDGE,{"derivedFrom":subQ0}),-1.0]])]});}
            var Q11;
            {var subQ0=sQuery(id+"F7.wireOp",EDGE,"E104.MirrorCS");Q11=makeQuery(id+"F7.imprint","IMPRINT",FACE,{"disambiguationData":[TD([[makeQuery(id+"F7.imprint","IMPRINT",EDGE,{"derivedFrom":subQ0}),-1.0]])]});}
            var Q12;
            {var subQ0=sQuery(id+"F7.wireOp",EDGE,"E106.MirrorCS");Q12=makeQuery(id+"F7.imprint","IMPRINT",FACE,{"disambiguationData":[TD([[makeQuery(id+"F7.imprint","IMPRINT",EDGE,{"derivedFrom":subQ0}),-1.0]])]});}
            var Q13;
            {var subQ0=sQuery(id+"F7.wireOp",EDGE,"E108.MirrorCS");Q13=makeQuery(id+"F7.imprint","IMPRINT",FACE,{"disambiguationData":[TD([[makeQuery(id+"F7.imprint","IMPRINT",EDGE,{"derivedFrom":subQ0}),-1.0]])]});}
            var Q14;
            {var subQ0=sQuery(id+"F7.wireOp",EDGE,"E110.MirrorCS");Q14=makeQuery(id+"F7.imprint","IMPRINT",FACE,{"disambiguationData":[TD([[makeQuery(id+"F7.imprint","IMPRINT",EDGE,{"derivedFrom":subQ0}),-1.0]])]});}
            var Q15;
            {var subQ0=sQuery(id+"F7.wireOp",EDGE,"E112.MirrorCS");Q15=makeQuery(id+"F7.imprint","IMPRINT",FACE,{"disambiguationData":[TD([[makeQuery(id+"F7.imprint","IMPRINT",EDGE,{"derivedFrom":subQ0}),-1.0]])]});}
            var Q16;
            {var subQ0=sQuery(id+"F7.wireOp",EDGE,"E114.MirrorCS");Q16=makeQuery(id+"F7.imprint","IMPRINT",FACE,{"disambiguationData":[TD([[makeQuery(id+"F7.imprint","IMPRINT",EDGE,{"derivedFrom":subQ0}),-1.0]])]});}
            var Q17;
            {var subQ0=sQuery(id+"F7.wireOp",EDGE,"E116.MirrorCS");Q17=makeQuery(id+"F7.imprint","IMPRINT",FACE,{"disambiguationData":[TD([[makeQuery(id+"F7.imprint","IMPRINT",EDGE,{"derivedFrom":subQ0}),-1.0]])]});}
            var Q18;
            {var subQ0=sQuery(id+"F7.wireOp",EDGE,"E118.MirrorCS");Q18=makeQuery(id+"F7.imprint","IMPRINT",FACE,{"disambiguationData":[TD([[makeQuery(id+"F7.imprint","IMPRINT",EDGE,{"derivedFrom":subQ0}),-1.0]])]});}
            var Q19;
            {var subQ0=sQuery(id+"F7.wireOp",EDGE,"E155.MirrorCS");Q19=makeQuery(id+"F7.imprint","IMPRINT",FACE,{"disambiguationData":[TD([[makeQuery(id+"F7.imprint","IMPRINT",EDGE,{"derivedFrom":subQ0}),-1.0]])]});}
            var Q20;
            {var subQ0=sQuery(id+"F7.wireOp",EDGE,"E153.MirrorCS");Q20=makeQuery(id+"F7.imprint","IMPRINT",FACE,{"disambiguationData":[TD([[makeQuery(id+"F7.imprint","IMPRINT",EDGE,{"derivedFrom":subQ0}),-1.0]])]});}
            var Q21;
            {var subQ0=sQuery(id+"F7.wireOp",EDGE,"E151.MirrorCS");Q21=makeQuery(id+"F7.imprint","IMPRINT",FACE,{"disambiguationData":[TD([[makeQuery(id+"F7.imprint","IMPRINT",EDGE,{"derivedFrom":subQ0}),-1.0]])]});}
            var Q22;
            {var subQ0=sQuery(id+"F7.wireOp",EDGE,"E149.MirrorCS");Q22=makeQuery(id+"F7.imprint","IMPRINT",FACE,{"disambiguationData":[TD([[makeQuery(id+"F7.imprint","IMPRINT",EDGE,{"derivedFrom":subQ0}),-1.0]])]});}
            var Q23;
            {var subQ0=sQuery(id+"F7.wireOp",EDGE,"E147.MirrorCS");Q23=makeQuery(id+"F7.imprint","IMPRINT",FACE,{"disambiguationData":[TD([[makeQuery(id+"F7.imprint","IMPRINT",EDGE,{"derivedFrom":subQ0}),-1.0]])]});}
            var Q24;
            {var subQ0=sQuery(id+"F7.wireOp",EDGE,"E145.MirrorCS");Q24=makeQuery(id+"F7.imprint","IMPRINT",FACE,{"disambiguationData":[TD([[makeQuery(id+"F7.imprint","IMPRINT",EDGE,{"derivedFrom":subQ0}),-1.0]])]});}
            var Q25;
            {var subQ0=sQuery(id+"F7.wireOp",EDGE,"E143.MirrorCS");Q25=makeQuery(id+"F7.imprint","IMPRINT",FACE,{"disambiguationData":[TD([[makeQuery(id+"F7.imprint","IMPRINT",EDGE,{"derivedFrom":subQ0}),-1.0]])]});}
            var Q26;
            {var subQ0=sQuery(id+"F7.wireOp",EDGE,"E142.MirrorCS");Q26=makeQuery(id+"F7.imprint","IMPRINT",FACE,{"disambiguationData":[TD([[makeQuery(id+"F7.imprint","IMPRINT",EDGE,{"derivedFrom":subQ0}),-1.0]])]});}
            var Q27;
            {var subQ0=sQuery(id+"F7.wireOp",EDGE,"E140.MirrorCS");Q27=makeQuery(id+"F7.imprint","IMPRINT",FACE,{"disambiguationData":[TD([[makeQuery(id+"F7.imprint","IMPRINT",EDGE,{"derivedFrom":subQ0}),-1.0]])]});}
            var Q28;
            {var subQ0=sQuery(id+"F7.wireOp",EDGE,"E138.MirrorCS");Q28=makeQuery(id+"F7.imprint","IMPRINT",FACE,{"disambiguationData":[TD([[makeQuery(id+"F7.imprint","IMPRINT",EDGE,{"derivedFrom":subQ0}),-1.0]])]});}
            var Q29;
            {var subQ0=sQuery(id+"F7.wireOp",EDGE,"E136.MirrorCS");Q29=makeQuery(id+"F7.imprint","IMPRINT",FACE,{"disambiguationData":[TD([[makeQuery(id+"F7.imprint","IMPRINT",EDGE,{"derivedFrom":subQ0}),-1.0]])]});}
            var Q30;
            {var subQ0=sQuery(id+"F7.wireOp",EDGE,"E134.MirrorCS");Q30=makeQuery(id+"F7.imprint","IMPRINT",FACE,{"disambiguationData":[TD([[makeQuery(id+"F7.imprint","IMPRINT",EDGE,{"derivedFrom":subQ0}),-1.0]])]});}
            var Q31;
            {var subQ0=sQuery(id+"F7.wireOp",EDGE,"E132.MirrorCS");Q31=makeQuery(id+"F7.imprint","IMPRINT",FACE,{"disambiguationData":[TD([[makeQuery(id+"F7.imprint","IMPRINT",EDGE,{"derivedFrom":subQ0}),-1.0]])]});}
            var Q32;
            {var subQ0=sQuery(id+"F7.wireOp",EDGE,"E130.MirrorCS");Q32=makeQuery(id+"F7.imprint","IMPRINT",FACE,{"disambiguationData":[TD([[makeQuery(id+"F7.imprint","IMPRINT",EDGE,{"derivedFrom":subQ0}),-1.0]])]});}
            var Q33;
            {var subQ0=sQuery(id+"F7.wireOp",EDGE,"E128.MirrorCS");Q33=makeQuery(id+"F7.imprint","IMPRINT",FACE,{"disambiguationData":[TD([[makeQuery(id+"F7.imprint","IMPRINT",EDGE,{"derivedFrom":subQ0}),-1.0]])]});}
            var Q34;
            {var subQ0=sQuery(id+"F7.wireOp",EDGE,"E124.MirrorCS");Q34=makeQuery(id+"F7.imprint","IMPRINT",FACE,{"disambiguationData":[TD([[makeQuery(id+"F7.imprint","IMPRINT",EDGE,{"derivedFrom":subQ0}),-1.0]])]});}
            var Q35;
            {var subQ0=sQuery(id+"F7.wireOp",EDGE,"E122.MirrorCS");Q35=makeQuery(id+"F7.imprint","IMPRINT",FACE,{"disambiguationData":[TD([[makeQuery(id+"F7.imprint","IMPRINT",EDGE,{"derivedFrom":subQ0}),-1.0]])]});}
            var Q36;
            {var subQ0=sQuery(id+"F7.wireOp",EDGE,"E161.MirrorCS");Q36=makeQuery(id+"F7.imprint","IMPRINT",FACE,{"disambiguationData":[TD([[makeQuery(id+"F7.imprint","IMPRINT",EDGE,{"derivedFrom":subQ0}),-1.0]])]});}
            var Q37;
            {var subQ0=sQuery(id+"F7.wireOp",EDGE,"E167.MirrorCS");Q37=makeQuery(id+"F7.imprint","IMPRINT",FACE,{"disambiguationData":[TD([[makeQuery(id+"F7.imprint","IMPRINT",EDGE,{"derivedFrom":subQ0}),-1.0]])]});}
            var Q38;
            {var subQ0=sQuery(id+"F7.wireOp",EDGE,"E124.MirrorCS");Q38=makeQuery(id+"F7.imprint","IMPRINT",FACE,{"disambiguationData":[TD([[makeQuery(id+"F7.imprint","IMPRINT",EDGE,{"derivedFrom":subQ0}),-1.0]])]});}
            var Q39;
            {var subQ0=sQuery(id+"F7.wireOp",EDGE,"E161.MirrorCS");Q39=makeQuery(id+"F7.imprint","IMPRINT",FACE,{"disambiguationData":[TD([[makeQuery(id+"F7.imprint","IMPRINT",EDGE,{"derivedFrom":subQ0}),-1.0]])]});}
            var Q40;
            {var subQ0=sQuery(id+"F7.wireOp",EDGE,"E165.MirrorCS");Q40=makeQuery(id+"F7.imprint","IMPRINT",FACE,{"disambiguationData":[TD([[makeQuery(id+"F7.imprint","IMPRINT",EDGE,{"derivedFrom":subQ0}),-1.0]])]});}
            var Q41;
            {var subQ0=sQuery(id+"F7.wireOp",EDGE,"E167.MirrorCS");Q41=makeQuery(id+"F7.imprint","IMPRINT",FACE,{"disambiguationData":[TD([[makeQuery(id+"F7.imprint","IMPRINT",EDGE,{"derivedFrom":subQ0}),-1.0]])]});}
            var Q42;
            {var subQ0=sQuery(id+"F7.wireOp",EDGE,"E171.MirrorCS");Q42=makeQuery(id+"F7.imprint","IMPRINT",FACE,{"disambiguationData":[TD([[makeQuery(id+"F7.imprint","IMPRINT",EDGE,{"derivedFrom":subQ0}),-1.0]])]});}
            var Q43;
            {var subQ0=sQuery(id+"F7.wireOp",EDGE,"E173.MirrorCS");Q43=makeQuery(id+"F7.imprint","IMPRINT",FACE,{"disambiguationData":[TD([[makeQuery(id+"F7.imprint","IMPRINT",EDGE,{"derivedFrom":subQ0}),-1.0]])]});}
            var Q44;
            {var subQ0=sQuery(id+"F7.wireOp",EDGE,"E177.MirrorCS");Q44=makeQuery(id+"F7.imprint","IMPRINT",FACE,{"disambiguationData":[TD([[makeQuery(id+"F7.imprint","IMPRINT",EDGE,{"derivedFrom":subQ0}),-1.0]])]});}
            var Q45;
            {var subQ0=sQuery(id+"F7.wireOp",EDGE,"E181.MirrorCS");Q45=makeQuery(id+"F7.imprint","IMPRINT",FACE,{"disambiguationData":[TD([[makeQuery(id+"F7.imprint","IMPRINT",EDGE,{"derivedFrom":subQ0}),-1.0]])]});}
            var Q46;
            {var subQ0=sQuery(id+"F7.wireOp",EDGE,"E126.MirrorCS");Q46=makeQuery(id+"F7.imprint","IMPRINT",FACE,{"disambiguationData":[TD([[makeQuery(id+"F7.imprint","IMPRINT",EDGE,{"derivedFrom":subQ0}),-1.0]])]});}
            var Q47;
            {var subQ0=sQuery(id+"F7.wireOp",EDGE,"E159.MirrorCS");Q47=makeQuery(id+"F7.imprint","IMPRINT",FACE,{"disambiguationData":[TD([[makeQuery(id+"F7.imprint","IMPRINT",EDGE,{"derivedFrom":subQ0}),-1.0]])]});}
            var Q48;
            {var subQ0=sQuery(id+"F7.wireOp",EDGE,"E163.MirrorCS");Q48=makeQuery(id+"F7.imprint","IMPRINT",FACE,{"disambiguationData":[TD([[makeQuery(id+"F7.imprint","IMPRINT",EDGE,{"derivedFrom":subQ0}),-1.0]])]});}
            var Q49;
            {var subQ0=sQuery(id+"F7.wireOp",EDGE,"E169.MirrorCS");Q49=makeQuery(id+"F7.imprint","IMPRINT",FACE,{"disambiguationData":[TD([[makeQuery(id+"F7.imprint","IMPRINT",EDGE,{"derivedFrom":subQ0}),-1.0]])]});}
            var Q50;
            {var subQ0=sQuery(id+"F7.wireOp",EDGE,"E175.MirrorCS");Q50=makeQuery(id+"F7.imprint","IMPRINT",FACE,{"disambiguationData":[TD([[makeQuery(id+"F7.imprint","IMPRINT",EDGE,{"derivedFrom":subQ0}),-1.0]])]});}
            var Q51;
            {var subQ0=sQuery(id+"F7.wireOp",EDGE,"E183.MirrorCS");Q51=makeQuery(id+"F7.imprint","IMPRINT",FACE,{"disambiguationData":[TD([[makeQuery(id+"F7.imprint","IMPRINT",EDGE,{"derivedFrom":subQ0}),-1.0]])]});}
            var Q52;
            {var subQ0=sQuery(id+"F7.wireOp",EDGE,"E185.MirrorCS");Q52=makeQuery(id+"F7.imprint","IMPRINT",FACE,{"disambiguationData":[TD([[makeQuery(id+"F7.imprint","IMPRINT",EDGE,{"derivedFrom":subQ0}),-1.0]])]});}
            var Q53;
            {var subQ0=sQuery(id+"F7.wireOp",EDGE,"E187.MirrorCS");Q53=makeQuery(id+"F7.imprint","IMPRINT",FACE,{"disambiguationData":[TD([[makeQuery(id+"F7.imprint","IMPRINT",EDGE,{"derivedFrom":subQ0}),-1.0]])]});}
            var Q54;
            {var subQ0=sQuery(id+"F7.wireOp",EDGE,"E189.MirrorCS");Q54=makeQuery(id+"F7.imprint","IMPRINT",FACE,{"disambiguationData":[TD([[makeQuery(id+"F7.imprint","IMPRINT",EDGE,{"derivedFrom":subQ0}),-1.0]])]});}
            var Q55;
            {var subQ0=sQuery(id+"F7.wireOp",EDGE,"E191.MirrorCS");Q55=makeQuery(id+"F7.imprint","IMPRINT",FACE,{"disambiguationData":[TD([[makeQuery(id+"F7.imprint","IMPRINT",EDGE,{"derivedFrom":subQ0}),-1.0]])]});}
            var Q56;
            {var subQ0=sQuery(id+"F7.wireOp",EDGE,"E193.MirrorCS");Q56=makeQuery(id+"F7.imprint","IMPRINT",FACE,{"disambiguationData":[TD([[makeQuery(id+"F7.imprint","IMPRINT",EDGE,{"derivedFrom":subQ0}),-1.0]])]});}
            var Q57;
            {var subQ2=sQuery(id+"F7.wireOp",EDGE,"E195.MirrorCS");Q57=makeQuery(id+"F7.imprint","IMPRINT",FACE,{"disambiguationData":[TD([[makeQuery(id+"F7.imprint","IMPRINT",EDGE,{"derivedFrom":subQ2}),-1.0]])]});}
            var Q58;
            {var subQ0=sQuery(id+"F7.wireOp",EDGE,"E197.MirrorCS");Q58=makeQuery(id+"F7.imprint","IMPRINT",FACE,{"disambiguationData":[TD([[makeQuery(id+"F7.imprint","IMPRINT",EDGE,{"derivedFrom":subQ0}),-1.0]])]});}
            var Q59;
            {var subQ0=sQuery(id+"F7.wireOp",EDGE,"E199.MirrorCS");Q59=makeQuery(id+"F7.imprint","IMPRINT",FACE,{"disambiguationData":[TD([[makeQuery(id+"F7.imprint","IMPRINT",EDGE,{"derivedFrom":subQ0}),-1.0]])]});}
            var Q60;
            {var subQ0=sQuery(id+"F7.wireOp",EDGE,"E201.MirrorCS");Q60=makeQuery(id+"F7.imprint","IMPRINT",FACE,{"disambiguationData":[TD([[makeQuery(id+"F7.imprint","IMPRINT",EDGE,{"derivedFrom":subQ0}),-1.0]])]});}
            var Q61;
            {var subQ0=sQuery(id+"F7.wireOp",EDGE,"E203.MirrorCS");Q61=makeQuery(id+"F7.imprint","IMPRINT",FACE,{"disambiguationData":[TD([[makeQuery(id+"F7.imprint","IMPRINT",EDGE,{"derivedFrom":subQ0}),-1.0]])]});}
            var Q62;
            {var subQ0=sQuery(id+"F7.wireOp",EDGE,"E205.MirrorCS");Q62=makeQuery(id+"F7.imprint","IMPRINT",FACE,{"disambiguationData":[TD([[makeQuery(id+"F7.imprint","IMPRINT",EDGE,{"derivedFrom":subQ0}),-1.0]])]});}
            var Q63;
            {var subQ0=sQuery(id+"F7.wireOp",EDGE,"E207.MirrorCS");Q63=makeQuery(id+"F7.imprint","IMPRINT",FACE,{"disambiguationData":[TD([[makeQuery(id+"F7.imprint","IMPRINT",EDGE,{"derivedFrom":subQ0}),-1.0]])]});}
            var Q64;
            {var subQ0=sQuery(id+"F7.wireOp",EDGE,"E179.MirrorCS");Q64=makeQuery(id+"F7.imprint","IMPRINT",FACE,{"disambiguationData":[TD([[makeQuery(id+"F7.imprint","IMPRINT",EDGE,{"derivedFrom":subQ0}),-1.0]])]});}
            var Q65;
            {var subQ0=sQuery(id+"F7.wireOp",EDGE,"E209.MirrorCS");Q65=makeQuery(id+"F7.imprint","IMPRINT",FACE,{"disambiguationData":[TD([[makeQuery(id+"F7.imprint","IMPRINT",EDGE,{"derivedFrom":subQ0}),-1.0]])]});}
            var Q66;
            {var subQ0=sQuery(id+"F7.wireOp",EDGE,"E211.MirrorCS");Q66=makeQuery(id+"F7.imprint","IMPRINT",FACE,{"disambiguationData":[TD([[makeQuery(id+"F7.imprint","IMPRINT",EDGE,{"derivedFrom":subQ0}),-1.0]])]});}
            var Q67;
            {var subQ0=sQuery(id+"F7.wireOp",EDGE,"E217.MirrorCS");Q67=makeQuery(id+"F7.imprint","IMPRINT",FACE,{"disambiguationData":[TD([[makeQuery(id+"F7.imprint","IMPRINT",EDGE,{"derivedFrom":subQ0}),-1.0]])]});}
            var Q68;
            {var subQ0=sQuery(id+"F7.wireOp",EDGE,"E227.MirrorCS");Q68=makeQuery(id+"F7.imprint","IMPRINT",FACE,{"disambiguationData":[TD([[makeQuery(id+"F7.imprint","IMPRINT",EDGE,{"derivedFrom":subQ0}),-1.0]])]});}
            var Q69;
            {var subQ0=sQuery(id+"F7.wireOp",EDGE,"E213.MirrorCS");Q69=makeQuery(id+"F7.imprint","IMPRINT",FACE,{"disambiguationData":[TD([[makeQuery(id+"F7.imprint","IMPRINT",EDGE,{"derivedFrom":subQ0}),-1.0]])]});}
            var Q70;
            {var subQ0=sQuery(id+"F7.wireOp",EDGE,"E215.MirrorCS");Q70=makeQuery(id+"F7.imprint","IMPRINT",FACE,{"disambiguationData":[TD([[makeQuery(id+"F7.imprint","IMPRINT",EDGE,{"derivedFrom":subQ0}),-1.0]])]});}
            var Q71;
            {var subQ0=sQuery(id+"F7.wireOp",EDGE,"E219.MirrorCS");Q71=makeQuery(id+"F7.imprint","IMPRINT",FACE,{"disambiguationData":[TD([[makeQuery(id+"F7.imprint","IMPRINT",EDGE,{"derivedFrom":subQ0}),-1.0]])]});}
            var Q72;
            {var subQ0=sQuery(id+"F7.wireOp",EDGE,"E221.MirrorCS");Q72=makeQuery(id+"F7.imprint","IMPRINT",FACE,{"disambiguationData":[TD([[makeQuery(id+"F7.imprint","IMPRINT",EDGE,{"derivedFrom":subQ0}),-1.0]])]});}
            var Q73;
            {var subQ0=sQuery(id+"F7.wireOp",EDGE,"E225.MirrorCS");Q73=makeQuery(id+"F7.imprint","IMPRINT",FACE,{"disambiguationData":[TD([[makeQuery(id+"F7.imprint","IMPRINT",EDGE,{"derivedFrom":subQ0}),-1.0]])]});}
            var Q74;
            {var subQ0=sQuery(id+"F7.wireOp",EDGE,"E229.MirrorCS");Q74=makeQuery(id+"F7.imprint","IMPRINT",FACE,{"disambiguationData":[TD([[makeQuery(id+"F7.imprint","IMPRINT",EDGE,{"derivedFrom":subQ0}),-1.0]])]});}
            var Q75;
            {var subQ0=sQuery(id+"F7.wireOp",EDGE,"E233.MirrorCS");Q75=makeQuery(id+"F7.imprint","IMPRINT",FACE,{"disambiguationData":[TD([[makeQuery(id+"F7.imprint","IMPRINT",EDGE,{"derivedFrom":subQ0}),-1.0]])]});}
            var Q76;
            {var subQ0=sQuery(id+"F7.wireOp",EDGE,"E235.MirrorCS");Q76=makeQuery(id+"F7.imprint","IMPRINT",FACE,{"disambiguationData":[TD([[makeQuery(id+"F7.imprint","IMPRINT",EDGE,{"derivedFrom":subQ0}),-1.0]])]});}
            var Q77;
            {var subQ0=sQuery(id+"F7.wireOp",EDGE,"E241.MirrorCS");Q77=makeQuery(id+"F7.imprint","IMPRINT",FACE,{"disambiguationData":[TD([[makeQuery(id+"F7.imprint","IMPRINT",EDGE,{"derivedFrom":subQ0}),-1.0]])]});}
            var Q78;
            {var subQ0=sQuery(id+"F7.wireOp",EDGE,"E243.MirrorCS");Q78=makeQuery(id+"F7.imprint","IMPRINT",FACE,{"disambiguationData":[TD([[makeQuery(id+"F7.imprint","IMPRINT",EDGE,{"derivedFrom":subQ0}),-1.0]])]});}
            var Q79;
            {var subQ0=sQuery(id+"F7.wireOp",EDGE,"E245.MirrorCS");Q79=makeQuery(id+"F7.imprint","IMPRINT",FACE,{"disambiguationData":[TD([[makeQuery(id+"F7.imprint","IMPRINT",EDGE,{"derivedFrom":subQ0}),-1.0]])]});}
            var Q80;
            {var subQ0=sQuery(id+"F7.wireOp",EDGE,"E247.MirrorCS");Q80=makeQuery(id+"F7.imprint","IMPRINT",FACE,{"disambiguationData":[TD([[makeQuery(id+"F7.imprint","IMPRINT",EDGE,{"derivedFrom":subQ0}),-1.0]])]});}
            var Q81;
            {var subQ0=sQuery(id+"F7.wireOp",EDGE,"E249.MirrorCS");Q81=makeQuery(id+"F7.imprint","IMPRINT",FACE,{"disambiguationData":[TD([[makeQuery(id+"F7.imprint","IMPRINT",EDGE,{"derivedFrom":subQ0}),-1.0]])]});}
            var Q82;
            {var subQ0=sQuery(id+"F7.wireOp",EDGE,"E253.MirrorCS");Q82=makeQuery(id+"F7.imprint","IMPRINT",FACE,{"disambiguationData":[TD([[makeQuery(id+"F7.imprint","IMPRINT",EDGE,{"derivedFrom":subQ0}),-1.0]])]});}
            var Q83;
            {var subQ0=sQuery(id+"F7.wireOp",EDGE,"E223.MirrorCS");Q83=makeQuery(id+"F7.imprint","IMPRINT",FACE,{"disambiguationData":[TD([[makeQuery(id+"F7.imprint","IMPRINT",EDGE,{"derivedFrom":subQ0}),-1.0]])]});}
            var Q84;
            {var subQ0=sQuery(id+"F7.wireOp",EDGE,"E231.MirrorCS");Q84=makeQuery(id+"F7.imprint","IMPRINT",FACE,{"disambiguationData":[TD([[makeQuery(id+"F7.imprint","IMPRINT",EDGE,{"derivedFrom":subQ0}),-1.0]])]});}
            var Q85;
            {var subQ0=sQuery(id+"F7.wireOp",EDGE,"E237.MirrorCS");Q85=makeQuery(id+"F7.imprint","IMPRINT",FACE,{"disambiguationData":[TD([[makeQuery(id+"F7.imprint","IMPRINT",EDGE,{"derivedFrom":subQ0}),-1.0]])]});}
            var Q86;
            {var subQ0=sQuery(id+"F7.wireOp",EDGE,"E239.MirrorCS");Q86=makeQuery(id+"F7.imprint","IMPRINT",FACE,{"disambiguationData":[TD([[makeQuery(id+"F7.imprint","IMPRINT",EDGE,{"derivedFrom":subQ0}),-1.0]])]});}
            var Q87;
            {var subQ0=sQuery(id+"F7.wireOp",EDGE,"E251.MirrorCS");Q87=makeQuery(id+"F7.imprint","IMPRINT",FACE,{"disambiguationData":[TD([[makeQuery(id+"F7.imprint","IMPRINT",EDGE,{"derivedFrom":subQ0}),-1.0]])]});}
            var Q88;
            {var subQ0=sQuery(id+"F7.wireOp",EDGE,"E255.MirrorCS");Q88=makeQuery(id+"F7.imprint","IMPRINT",FACE,{"disambiguationData":[TD([[makeQuery(id+"F7.imprint","IMPRINT",EDGE,{"derivedFrom":subQ0}),-1.0]])]});}
            var Q89;
            {var subQ0=sQuery(id+"F7.wireOp",EDGE,"E257.MirrorCS");Q89=makeQuery(id+"F7.imprint","IMPRINT",FACE,{"disambiguationData":[TD([[makeQuery(id+"F7.imprint","IMPRINT",EDGE,{"derivedFrom":subQ0}),-1.0]])]});}
            var Q90;
            {var subQ0=sQuery(id+"F7.wireOp",EDGE,"E302.MirrorCS");Q90=makeQuery(id+"F7.imprint","IMPRINT",FACE,{"disambiguationData":[TD([[makeQuery(id+"F7.imprint","IMPRINT",EDGE,{"derivedFrom":subQ0}),-1.0]])]});}
            var Q91;
            {var subQ0=sQuery(id+"F7.wireOp",EDGE,"E300.MirrorCS");Q91=makeQuery(id+"F7.imprint","IMPRINT",FACE,{"disambiguationData":[TD([[makeQuery(id+"F7.imprint","IMPRINT",EDGE,{"derivedFrom":subQ0}),-1.0]])]});}
            var Q92;
            {var subQ0=sQuery(id+"F7.wireOp",EDGE,"E298.MirrorCS");Q92=makeQuery(id+"F7.imprint","IMPRINT",FACE,{"disambiguationData":[TD([[makeQuery(id+"F7.imprint","IMPRINT",EDGE,{"derivedFrom":subQ0}),-1.0]])]});}
            var Q93;
            {var subQ0=sQuery(id+"F7.wireOp",EDGE,"E296.MirrorCS");Q93=makeQuery(id+"F7.imprint","IMPRINT",FACE,{"disambiguationData":[TD([[makeQuery(id+"F7.imprint","IMPRINT",EDGE,{"derivedFrom":subQ0}),-1.0]])]});}
            var Q94;
            {var subQ0=sQuery(id+"F7.wireOp",EDGE,"E294.MirrorCS");Q94=makeQuery(id+"F7.imprint","IMPRINT",FACE,{"disambiguationData":[TD([[makeQuery(id+"F7.imprint","IMPRINT",EDGE,{"derivedFrom":subQ0}),-1.0]])]});}
            var Q95;
            {var subQ0=sQuery(id+"F7.wireOp",EDGE,"E292.MirrorCS");Q95=makeQuery(id+"F7.imprint","IMPRINT",FACE,{"disambiguationData":[TD([[makeQuery(id+"F7.imprint","IMPRINT",EDGE,{"derivedFrom":subQ0}),-1.0]])]});}
            var Q96;
            {var subQ0=sQuery(id+"F7.wireOp",EDGE,"E290.MirrorCS");Q96=makeQuery(id+"F7.imprint","IMPRINT",FACE,{"disambiguationData":[TD([[makeQuery(id+"F7.imprint","IMPRINT",EDGE,{"derivedFrom":subQ0}),-1.0]])]});}
            var Q97;
            {var subQ0=sQuery(id+"F7.wireOp",EDGE,"E288.MirrorCS");Q97=makeQuery(id+"F7.imprint","IMPRINT",FACE,{"disambiguationData":[TD([[makeQuery(id+"F7.imprint","IMPRINT",EDGE,{"derivedFrom":subQ0}),-1.0]])]});}
            var Q98;
            {var subQ0=sQuery(id+"F7.wireOp",EDGE,"E282.MirrorCS");Q98=makeQuery(id+"F7.imprint","IMPRINT",FACE,{"disambiguationData":[TD([[makeQuery(id+"F7.imprint","IMPRINT",EDGE,{"derivedFrom":subQ0}),-1.0]])]});}
            var Q99;
            {var subQ0=sQuery(id+"F7.wireOp",EDGE,"E280.MirrorCS");Q99=makeQuery(id+"F7.imprint","IMPRINT",FACE,{"disambiguationData":[TD([[makeQuery(id+"F7.imprint","IMPRINT",EDGE,{"derivedFrom":subQ0}),-1.0]])]});}
            var Q100;
            {var subQ0=sQuery(id+"F7.wireOp",EDGE,"E278.MirrorCS");Q100=makeQuery(id+"F7.imprint","IMPRINT",FACE,{"disambiguationData":[TD([[makeQuery(id+"F7.imprint","IMPRINT",EDGE,{"derivedFrom":subQ0}),-1.0]])]});}
            var Q101;
            {var subQ0=sQuery(id+"F7.wireOp",EDGE,"E274.MirrorCS");Q101=makeQuery(id+"F7.imprint","IMPRINT",FACE,{"disambiguationData":[TD([[makeQuery(id+"F7.imprint","IMPRINT",EDGE,{"derivedFrom":subQ0}),-1.0]])]});}
            var Q102;
            {var subQ0=sQuery(id+"F7.wireOp",EDGE,"E270.MirrorCS");Q102=makeQuery(id+"F7.imprint","IMPRINT",FACE,{"disambiguationData":[TD([[makeQuery(id+"F7.imprint","IMPRINT",EDGE,{"derivedFrom":subQ0}),-1.0]])]});}
            var Q103;
            {var subQ0=sQuery(id+"F7.wireOp",EDGE,"E268.MirrorCS");Q103=makeQuery(id+"F7.imprint","IMPRINT",FACE,{"disambiguationData":[TD([[makeQuery(id+"F7.imprint","IMPRINT",EDGE,{"derivedFrom":subQ0}),-1.0]])]});}
            var Q104;
            {var subQ0=sQuery(id+"F7.wireOp",EDGE,"E266.MirrorCS");Q104=makeQuery(id+"F7.imprint","IMPRINT",FACE,{"disambiguationData":[TD([[makeQuery(id+"F7.imprint","IMPRINT",EDGE,{"derivedFrom":subQ0}),-1.0]])]});}
            var Q105;
            {var subQ0=sQuery(id+"F7.wireOp",EDGE,"E264.MirrorCS");Q105=makeQuery(id+"F7.imprint","IMPRINT",FACE,{"disambiguationData":[TD([[makeQuery(id+"F7.imprint","IMPRINT",EDGE,{"derivedFrom":subQ0}),-1.0]])]});}
            var Q106;
            {var subQ0=sQuery(id+"F7.wireOp",EDGE,"E262.MirrorCS");Q106=makeQuery(id+"F7.imprint","IMPRINT",FACE,{"disambiguationData":[TD([[makeQuery(id+"F7.imprint","IMPRINT",EDGE,{"derivedFrom":subQ0}),-1.0]])]});}
            var Q107;
            {var subQ0=sQuery(id+"F7.wireOp",EDGE,"E260.MirrorCS");Q107=makeQuery(id+"F7.imprint","IMPRINT",FACE,{"disambiguationData":[TD([[makeQuery(id+"F7.imprint","IMPRINT",EDGE,{"derivedFrom":subQ0}),-1.0]])]});}
            var Q108;
            {var subQ2=sQuery(id+"F7.wireOp",EDGE,"E259.MirrorCS");Q108=makeQuery(id+"F7.imprint","IMPRINT",FACE,{"disambiguationData":[TD([[makeQuery(id+"F7.imprint","IMPRINT",EDGE,{"derivedFrom":subQ2}),-1.0]])]});}
            var Q109;
            {var subQ0=sQuery(id+"F7.wireOp",EDGE,"E286.MirrorCS");Q109=makeQuery(id+"F7.imprint","IMPRINT",FACE,{"disambiguationData":[TD([[makeQuery(id+"F7.imprint","IMPRINT",EDGE,{"derivedFrom":subQ0}),-1.0]])]});}
            var Q110;
            {var subQ0=sQuery(id+"F7.wireOp",EDGE,"E284.MirrorCS");Q110=makeQuery(id+"F7.imprint","IMPRINT",FACE,{"disambiguationData":[TD([[makeQuery(id+"F7.imprint","IMPRINT",EDGE,{"derivedFrom":subQ0}),-1.0]])]});}
            var Q111;
            {var subQ0=sQuery(id+"F7.wireOp",EDGE,"E276.MirrorCS");Q111=makeQuery(id+"F7.imprint","IMPRINT",FACE,{"disambiguationData":[TD([[makeQuery(id+"F7.imprint","IMPRINT",EDGE,{"derivedFrom":subQ0}),-1.0]])]});}
            var Q112;
            {var subQ0=sQuery(id+"F7.wireOp",EDGE,"E272.MirrorCS");Q112=makeQuery(id+"F7.imprint","IMPRINT",FACE,{"disambiguationData":[TD([[makeQuery(id+"F7.imprint","IMPRINT",EDGE,{"derivedFrom":subQ0}),-1.0]])]});}
            var Q113;
            {var subQ154=sQuery(id+"F7.wireOp",EDGE,"E82.bottom");Q113=makeQuery(id+"F7.imprint","IMPRINT",FACE,{"disambiguationData":[TD([[makeQuery(id+"F7.imprint","IMPRINT",EDGE,{"derivedFrom":subQ154}),1.0]])]});}
            extrude(context, id + "F10", {"entities" : qUnion([Q0, Q1, Q2, Q3, Q4, Q5, Q6, Q7, Q8, Q9, Q10, Q11, Q12, Q13, Q14, Q15, Q16, Q17, Q18, Q19, Q20, Q21, Q22, Q23, Q24, Q25, Q26, Q27, Q28, Q29, Q30, Q31, Q32, Q33, Q34, Q35, Q36, Q37, Q38, Q39, Q40, Q41, Q42, Q43, Q44, Q45, Q46, Q47, Q48, Q49, Q50, Q51, Q52, Q53, Q54, Q55, Q56, Q57, Q58, Q59, Q60, Q61, Q62, Q63, Q64, Q65, Q66, Q67, Q68, Q69, Q70, Q71, Q72, Q73, Q74, Q75, Q76, Q77, Q78, Q79, Q80, Q81, Q82, Q83, Q84, Q85, Q86, Q87, Q88, Q89, Q90, Q91, Q92, Q93, Q94, Q95, Q96, Q97, Q98, Q99, Q100, Q101, Q102, Q103, Q104, Q105, Q106, Q107, Q108, Q109, Q110, Q111, Q112, Q113]), "depth" : 3 * mm, "offsetDistance" : 25 * mm});
        }
        {
            var Q0;
            {var subQ13=sQuery(id+"F7.wireOp",EDGE,"E119.bottom");Q0=makeQuery(id+"F7.imprint","IMPRINT",FACE,{"disambiguationData":[TD([[makeQuery(id+"F7.imprint","IMPRINT",EDGE,{"derivedFrom":subQ13}),-1.0]])]});}
            var Q1;
            {var subQ0=sQuery(id+"F7.wireOp",EDGE,"E80.bottom");Q1=makeQuery(id+"F7.imprint","IMPRINT",FACE,{"disambiguationData":[TD([[makeQuery(id+"F7.imprint","IMPRINT",EDGE,{"derivedFrom":subQ0}),1.0]])]});}
            var Q2;
            {var subQ0=sQuery(id+"F7.wireOp",EDGE,"E81");Q2=makeQuery(id+"F7.imprint","IMPRINT",FACE,{"disambiguationData":[TD([[makeQuery(id+"F7.imprint","IMPRINT",EDGE,{"derivedFrom":subQ0}),-1.0]])]});}
            var Q3;
            {var subQ0=sQuery(id+"F7.wireOp",EDGE,"E83.MirrorCS");Q3=makeQuery(id+"F7.imprint","IMPRINT",FACE,{"disambiguationData":[TD([[makeQuery(id+"F7.imprint","IMPRINT",EDGE,{"derivedFrom":subQ0}),1.0]])]});}
            var Q4;
            {var subQ0=sQuery(id+"F7.wireOp",EDGE,"E84.MirrorCS");Q4=makeQuery(id+"F7.imprint","IMPRINT",FACE,{"disambiguationData":[TD([[makeQuery(id+"F7.imprint","IMPRINT",EDGE,{"derivedFrom":subQ0}),1.0]])]});}
            var Q5;
            {var subQ0=sQuery(id+"F7.wireOp",EDGE,"E86.MirrorCS");Q5=makeQuery(id+"F7.imprint","IMPRINT",FACE,{"disambiguationData":[TD([[makeQuery(id+"F7.imprint","IMPRINT",EDGE,{"derivedFrom":subQ0}),-1.0]])]});}
            var Q6;
            {var subQ0=sQuery(id+"F7.wireOp",EDGE,"E87.MirrorCS");Q6=makeQuery(id+"F7.imprint","IMPRINT",FACE,{"disambiguationData":[TD([[makeQuery(id+"F7.imprint","IMPRINT",EDGE,{"derivedFrom":subQ0}),1.0]])]});}
            var Q7;
            {var subQ0=sQuery(id+"F7.wireOp",EDGE,"E89.MirrorCS");Q7=makeQuery(id+"F7.imprint","IMPRINT",FACE,{"disambiguationData":[TD([[makeQuery(id+"F7.imprint","IMPRINT",EDGE,{"derivedFrom":subQ0}),1.0]])]});}
            var Q8;
            {var subQ0=sQuery(id+"F7.wireOp",EDGE,"E90.MirrorCS");Q8=makeQuery(id+"F7.imprint","IMPRINT",FACE,{"disambiguationData":[TD([[makeQuery(id+"F7.imprint","IMPRINT",EDGE,{"derivedFrom":subQ0}),-1.0]])]});}
            var Q9;
            {var subQ0=sQuery(id+"F7.wireOp",EDGE,"E91.MirrorCS");Q9=makeQuery(id+"F7.imprint","IMPRINT",FACE,{"disambiguationData":[TD([[makeQuery(id+"F7.imprint","IMPRINT",EDGE,{"derivedFrom":subQ0}),1.0]])]});}
            var Q10;
            {var subQ0=sQuery(id+"F7.wireOp",EDGE,"E93.MirrorCS");Q10=makeQuery(id+"F7.imprint","IMPRINT",FACE,{"disambiguationData":[TD([[makeQuery(id+"F7.imprint","IMPRINT",EDGE,{"derivedFrom":subQ0}),1.0]])]});}
            var Q11;
            {var subQ0=sQuery(id+"F7.wireOp",EDGE,"E94.MirrorCS");Q11=makeQuery(id+"F7.imprint","IMPRINT",FACE,{"disambiguationData":[TD([[makeQuery(id+"F7.imprint","IMPRINT",EDGE,{"derivedFrom":subQ0}),-1.0]])]});}
            var Q12;
            {var subQ0=sQuery(id+"F7.wireOp",EDGE,"E95.MirrorCS");Q12=makeQuery(id+"F7.imprint","IMPRINT",FACE,{"disambiguationData":[TD([[makeQuery(id+"F7.imprint","IMPRINT",EDGE,{"derivedFrom":subQ0}),1.0]])]});}
            var Q13;
            {var subQ0=sQuery(id+"F7.wireOp",EDGE,"E97.MirrorCS");Q13=makeQuery(id+"F7.imprint","IMPRINT",FACE,{"disambiguationData":[TD([[makeQuery(id+"F7.imprint","IMPRINT",EDGE,{"derivedFrom":subQ0}),1.0]])]});}
            var Q14;
            {var subQ0=sQuery(id+"F7.wireOp",EDGE,"E98.MirrorCS");Q14=makeQuery(id+"F7.imprint","IMPRINT",FACE,{"disambiguationData":[TD([[makeQuery(id+"F7.imprint","IMPRINT",EDGE,{"derivedFrom":subQ0}),-1.0]])]});}
            var Q15;
            {var subQ0=sQuery(id+"F7.wireOp",EDGE,"E99.MirrorCS");Q15=makeQuery(id+"F7.imprint","IMPRINT",FACE,{"disambiguationData":[TD([[makeQuery(id+"F7.imprint","IMPRINT",EDGE,{"derivedFrom":subQ0}),1.0]])]});}
            var Q16;
            {var subQ0=sQuery(id+"F7.wireOp",EDGE,"E101.MirrorCS");Q16=makeQuery(id+"F7.imprint","IMPRINT",FACE,{"disambiguationData":[TD([[makeQuery(id+"F7.imprint","IMPRINT",EDGE,{"derivedFrom":subQ0}),1.0]])]});}
            var Q17;
            {var subQ0=sQuery(id+"F7.wireOp",EDGE,"E102.MirrorCS");Q17=makeQuery(id+"F7.imprint","IMPRINT",FACE,{"disambiguationData":[TD([[makeQuery(id+"F7.imprint","IMPRINT",EDGE,{"derivedFrom":subQ0}),-1.0]])]});}
            var Q18;
            {var subQ0=sQuery(id+"F7.wireOp",EDGE,"E103.MirrorCS");Q18=makeQuery(id+"F7.imprint","IMPRINT",FACE,{"disambiguationData":[TD([[makeQuery(id+"F7.imprint","IMPRINT",EDGE,{"derivedFrom":subQ0}),1.0]])]});}
            var Q19;
            {var subQ0=sQuery(id+"F7.wireOp",EDGE,"E105.MirrorCS");Q19=makeQuery(id+"F7.imprint","IMPRINT",FACE,{"disambiguationData":[TD([[makeQuery(id+"F7.imprint","IMPRINT",EDGE,{"derivedFrom":subQ0}),1.0]])]});}
            var Q20;
            {var subQ0=sQuery(id+"F7.wireOp",EDGE,"E106.MirrorCS");Q20=makeQuery(id+"F7.imprint","IMPRINT",FACE,{"disambiguationData":[TD([[makeQuery(id+"F7.imprint","IMPRINT",EDGE,{"derivedFrom":subQ0}),-1.0]])]});}
            var Q21;
            {var subQ0=sQuery(id+"F7.wireOp",EDGE,"E107.MirrorCS");Q21=makeQuery(id+"F7.imprint","IMPRINT",FACE,{"disambiguationData":[TD([[makeQuery(id+"F7.imprint","IMPRINT",EDGE,{"derivedFrom":subQ0}),1.0]])]});}
            var Q22;
            {var subQ0=sQuery(id+"F7.wireOp",EDGE,"E109.MirrorCS");Q22=makeQuery(id+"F7.imprint","IMPRINT",FACE,{"disambiguationData":[TD([[makeQuery(id+"F7.imprint","IMPRINT",EDGE,{"derivedFrom":subQ0}),1.0]])]});}
            var Q23;
            {var subQ0=sQuery(id+"F7.wireOp",EDGE,"E110.MirrorCS");Q23=makeQuery(id+"F7.imprint","IMPRINT",FACE,{"disambiguationData":[TD([[makeQuery(id+"F7.imprint","IMPRINT",EDGE,{"derivedFrom":subQ0}),-1.0]])]});}
            var Q24;
            {var subQ0=sQuery(id+"F7.wireOp",EDGE,"E111.MirrorCS");Q24=makeQuery(id+"F7.imprint","IMPRINT",FACE,{"disambiguationData":[TD([[makeQuery(id+"F7.imprint","IMPRINT",EDGE,{"derivedFrom":subQ0}),1.0]])]});}
            var Q25;
            {var subQ0=sQuery(id+"F7.wireOp",EDGE,"E113.MirrorCS");Q25=makeQuery(id+"F7.imprint","IMPRINT",FACE,{"disambiguationData":[TD([[makeQuery(id+"F7.imprint","IMPRINT",EDGE,{"derivedFrom":subQ0}),1.0]])]});}
            var Q26;
            {var subQ0=sQuery(id+"F7.wireOp",EDGE,"E114.MirrorCS");Q26=makeQuery(id+"F7.imprint","IMPRINT",FACE,{"disambiguationData":[TD([[makeQuery(id+"F7.imprint","IMPRINT",EDGE,{"derivedFrom":subQ0}),-1.0]])]});}
            var Q27;
            {var subQ0=sQuery(id+"F7.wireOp",EDGE,"E115.MirrorCS");Q27=makeQuery(id+"F7.imprint","IMPRINT",FACE,{"disambiguationData":[TD([[makeQuery(id+"F7.imprint","IMPRINT",EDGE,{"derivedFrom":subQ0}),1.0]])]});}
            var Q28;
            {var subQ0=sQuery(id+"F7.wireOp",EDGE,"E117.MirrorCS");Q28=makeQuery(id+"F7.imprint","IMPRINT",FACE,{"disambiguationData":[TD([[makeQuery(id+"F7.imprint","IMPRINT",EDGE,{"derivedFrom":subQ0}),1.0]])]});}
            var Q29;
            {var subQ0=sQuery(id+"F7.wireOp",EDGE,"E118.MirrorCS");Q29=makeQuery(id+"F7.imprint","IMPRINT",FACE,{"disambiguationData":[TD([[makeQuery(id+"F7.imprint","IMPRINT",EDGE,{"derivedFrom":subQ0}),-1.0]])]});}
            var Q30;
            {var subQ0=sQuery(id+"F7.wireOp",EDGE,"E156.MirrorCS");Q30=makeQuery(id+"F7.imprint","IMPRINT",FACE,{"disambiguationData":[TD([[makeQuery(id+"F7.imprint","IMPRINT",EDGE,{"derivedFrom":subQ0}),1.0]])]});}
            var Q31;
            {var subQ0=sQuery(id+"F7.wireOp",EDGE,"E154.MirrorCS");Q31=makeQuery(id+"F7.imprint","IMPRINT",FACE,{"disambiguationData":[TD([[makeQuery(id+"F7.imprint","IMPRINT",EDGE,{"derivedFrom":subQ0}),1.0]])]});}
            var Q32;
            {var subQ0=sQuery(id+"F7.wireOp",EDGE,"E153.MirrorCS");Q32=makeQuery(id+"F7.imprint","IMPRINT",FACE,{"disambiguationData":[TD([[makeQuery(id+"F7.imprint","IMPRINT",EDGE,{"derivedFrom":subQ0}),-1.0]])]});}
            var Q33;
            {var subQ0=sQuery(id+"F7.wireOp",EDGE,"E152.MirrorCS");Q33=makeQuery(id+"F7.imprint","IMPRINT",FACE,{"disambiguationData":[TD([[makeQuery(id+"F7.imprint","IMPRINT",EDGE,{"derivedFrom":subQ0}),1.0]])]});}
            var Q34;
            {var subQ0=sQuery(id+"F7.wireOp",EDGE,"E150.MirrorCS");Q34=makeQuery(id+"F7.imprint","IMPRINT",FACE,{"disambiguationData":[TD([[makeQuery(id+"F7.imprint","IMPRINT",EDGE,{"derivedFrom":subQ0}),1.0]])]});}
            var Q35;
            {var subQ0=sQuery(id+"F7.wireOp",EDGE,"E149.MirrorCS");Q35=makeQuery(id+"F7.imprint","IMPRINT",FACE,{"disambiguationData":[TD([[makeQuery(id+"F7.imprint","IMPRINT",EDGE,{"derivedFrom":subQ0}),-1.0]])]});}
            var Q36;
            {var subQ0=sQuery(id+"F7.wireOp",EDGE,"E148.MirrorCS");Q36=makeQuery(id+"F7.imprint","IMPRINT",FACE,{"disambiguationData":[TD([[makeQuery(id+"F7.imprint","IMPRINT",EDGE,{"derivedFrom":subQ0}),1.0]])]});}
            var Q37;
            {var subQ0=sQuery(id+"F7.wireOp",EDGE,"E146.MirrorCS");Q37=makeQuery(id+"F7.imprint","IMPRINT",FACE,{"disambiguationData":[TD([[makeQuery(id+"F7.imprint","IMPRINT",EDGE,{"derivedFrom":subQ0}),1.0]])]});}
            var Q38;
            {var subQ0=sQuery(id+"F7.wireOp",EDGE,"E145.MirrorCS");Q38=makeQuery(id+"F7.imprint","IMPRINT",FACE,{"disambiguationData":[TD([[makeQuery(id+"F7.imprint","IMPRINT",EDGE,{"derivedFrom":subQ0}),-1.0]])]});}
            var Q39;
            {var subQ0=sQuery(id+"F7.wireOp",EDGE,"E144.MirrorCS");Q39=makeQuery(id+"F7.imprint","IMPRINT",FACE,{"disambiguationData":[TD([[makeQuery(id+"F7.imprint","IMPRINT",EDGE,{"derivedFrom":subQ0}),1.0]])]});}
            var Q40;
            {var subQ0=sQuery(id+"F7.wireOp",EDGE,"E142.MirrorCS");Q40=makeQuery(id+"F7.imprint","IMPRINT",FACE,{"disambiguationData":[TD([[makeQuery(id+"F7.imprint","IMPRINT",EDGE,{"derivedFrom":subQ0}),1.0]])]});}
            var Q41;
            {var subQ0=sQuery(id+"F7.wireOp",EDGE,"E142.MirrorCS");Q41=makeQuery(id+"F7.imprint","IMPRINT",FACE,{"disambiguationData":[TD([[makeQuery(id+"F7.imprint","IMPRINT",EDGE,{"derivedFrom":subQ0}),-1.0]])]});}
            var Q42;
            {var subQ0=sQuery(id+"F7.wireOp",EDGE,"E141.MirrorCS");Q42=makeQuery(id+"F7.imprint","IMPRINT",FACE,{"disambiguationData":[TD([[makeQuery(id+"F7.imprint","IMPRINT",EDGE,{"derivedFrom":subQ0}),1.0]])]});}
            var Q43;
            {var subQ0=sQuery(id+"F7.wireOp",EDGE,"E139.MirrorCS");Q43=makeQuery(id+"F7.imprint","IMPRINT",FACE,{"disambiguationData":[TD([[makeQuery(id+"F7.imprint","IMPRINT",EDGE,{"derivedFrom":subQ0}),1.0]])]});}
            var Q44;
            {var subQ0=sQuery(id+"F7.wireOp",EDGE,"E138.MirrorCS");Q44=makeQuery(id+"F7.imprint","IMPRINT",FACE,{"disambiguationData":[TD([[makeQuery(id+"F7.imprint","IMPRINT",EDGE,{"derivedFrom":subQ0}),-1.0]])]});}
            var Q45;
            {var subQ0=sQuery(id+"F7.wireOp",EDGE,"E137.MirrorCS");Q45=makeQuery(id+"F7.imprint","IMPRINT",FACE,{"disambiguationData":[TD([[makeQuery(id+"F7.imprint","IMPRINT",EDGE,{"derivedFrom":subQ0}),1.0]])]});}
            var Q46;
            {var subQ0=sQuery(id+"F7.wireOp",EDGE,"E135.MirrorCS");Q46=makeQuery(id+"F7.imprint","IMPRINT",FACE,{"disambiguationData":[TD([[makeQuery(id+"F7.imprint","IMPRINT",EDGE,{"derivedFrom":subQ0}),1.0]])]});}
            var Q47;
            {var subQ0=sQuery(id+"F7.wireOp",EDGE,"E134.MirrorCS");Q47=makeQuery(id+"F7.imprint","IMPRINT",FACE,{"disambiguationData":[TD([[makeQuery(id+"F7.imprint","IMPRINT",EDGE,{"derivedFrom":subQ0}),-1.0]])]});}
            var Q48;
            {var subQ0=sQuery(id+"F7.wireOp",EDGE,"E133.MirrorCS");Q48=makeQuery(id+"F7.imprint","IMPRINT",FACE,{"disambiguationData":[TD([[makeQuery(id+"F7.imprint","IMPRINT",EDGE,{"derivedFrom":subQ0}),1.0]])]});}
            var Q49;
            {var subQ0=sQuery(id+"F7.wireOp",EDGE,"E131.MirrorCS");Q49=makeQuery(id+"F7.imprint","IMPRINT",FACE,{"disambiguationData":[TD([[makeQuery(id+"F7.imprint","IMPRINT",EDGE,{"derivedFrom":subQ0}),1.0]])]});}
            var Q50;
            {var subQ0=sQuery(id+"F7.wireOp",EDGE,"E130.MirrorCS");Q50=makeQuery(id+"F7.imprint","IMPRINT",FACE,{"disambiguationData":[TD([[makeQuery(id+"F7.imprint","IMPRINT",EDGE,{"derivedFrom":subQ0}),-1.0]])]});}
            var Q51;
            {var subQ0=sQuery(id+"F7.wireOp",EDGE,"E129.MirrorCS");Q51=makeQuery(id+"F7.imprint","IMPRINT",FACE,{"disambiguationData":[TD([[makeQuery(id+"F7.imprint","IMPRINT",EDGE,{"derivedFrom":subQ0}),1.0]])]});}
            var Q52;
            {var subQ0=sQuery(id+"F7.wireOp",EDGE,"E127.MirrorCS");Q52=makeQuery(id+"F7.imprint","IMPRINT",FACE,{"disambiguationData":[TD([[makeQuery(id+"F7.imprint","IMPRINT",EDGE,{"derivedFrom":subQ0}),1.0]])]});}
            var Q53;
            {var subQ0=sQuery(id+"F7.wireOp",EDGE,"E126.MirrorCS");Q53=makeQuery(id+"F7.imprint","IMPRINT",FACE,{"disambiguationData":[TD([[makeQuery(id+"F7.imprint","IMPRINT",EDGE,{"derivedFrom":subQ0}),-1.0]])]});}
            var Q54;
            {var subQ0=sQuery(id+"F7.wireOp",EDGE,"E123.MirrorCS");Q54=makeQuery(id+"F7.imprint","IMPRINT",FACE,{"disambiguationData":[TD([[makeQuery(id+"F7.imprint","IMPRINT",EDGE,{"derivedFrom":subQ0}),1.0]])]});}
            var Q55;
            {var subQ0=sQuery(id+"F7.wireOp",EDGE,"E122.MirrorCS");Q55=makeQuery(id+"F7.imprint","IMPRINT",FACE,{"disambiguationData":[TD([[makeQuery(id+"F7.imprint","IMPRINT",EDGE,{"derivedFrom":subQ0}),-1.0]])]});}
            var Q56;
            {var subQ0=sQuery(id+"F7.wireOp",EDGE,"E122.MirrorCS");Q56=makeQuery(id+"F7.imprint","IMPRINT",FACE,{"disambiguationData":[TD([[makeQuery(id+"F7.imprint","IMPRINT",EDGE,{"derivedFrom":subQ0}),1.0]])]});}
            var Q57;
            {var subQ0=sQuery(id+"F7.wireOp",EDGE,"E160.MirrorCS");Q57=makeQuery(id+"F7.imprint","IMPRINT",FACE,{"disambiguationData":[TD([[makeQuery(id+"F7.imprint","IMPRINT",EDGE,{"derivedFrom":subQ0}),1.0]])]});}
            var Q58;
            {var subQ0=sQuery(id+"F7.wireOp",EDGE,"E161.MirrorCS");Q58=makeQuery(id+"F7.imprint","IMPRINT",FACE,{"disambiguationData":[TD([[makeQuery(id+"F7.imprint","IMPRINT",EDGE,{"derivedFrom":subQ0}),-1.0]])]});}
            var Q59;
            {var subQ0=sQuery(id+"F7.wireOp",EDGE,"E162.MirrorCS");Q59=makeQuery(id+"F7.imprint","IMPRINT",FACE,{"disambiguationData":[TD([[makeQuery(id+"F7.imprint","IMPRINT",EDGE,{"derivedFrom":subQ0}),1.0]])]});}
            var Q60;
            {var subQ0=sQuery(id+"F7.wireOp",EDGE,"E125.MirrorCS");Q60=makeQuery(id+"F7.imprint","IMPRINT",FACE,{"disambiguationData":[TD([[makeQuery(id+"F7.imprint","IMPRINT",EDGE,{"derivedFrom":subQ0}),1.0]])]});}
            var Q61;
            {var subQ0=sQuery(id+"F7.wireOp",EDGE,"E164.MirrorCS");Q61=makeQuery(id+"F7.imprint","IMPRINT",FACE,{"disambiguationData":[TD([[makeQuery(id+"F7.imprint","IMPRINT",EDGE,{"derivedFrom":subQ0}),1.0]])]});}
            var Q62;
            {var subQ0=sQuery(id+"F7.wireOp",EDGE,"E165.MirrorCS");Q62=makeQuery(id+"F7.imprint","IMPRINT",FACE,{"disambiguationData":[TD([[makeQuery(id+"F7.imprint","IMPRINT",EDGE,{"derivedFrom":subQ0}),-1.0]])]});}
            var Q63;
            {var subQ0=sQuery(id+"F7.wireOp",EDGE,"E168.MirrorCS");Q63=makeQuery(id+"F7.imprint","IMPRINT",FACE,{"disambiguationData":[TD([[makeQuery(id+"F7.imprint","IMPRINT",EDGE,{"derivedFrom":subQ0}),1.0]])]});}
            var Q64;
            {var subQ0=sQuery(id+"F7.wireOp",EDGE,"E169.MirrorCS");Q64=makeQuery(id+"F7.imprint","IMPRINT",FACE,{"disambiguationData":[TD([[makeQuery(id+"F7.imprint","IMPRINT",EDGE,{"derivedFrom":subQ0}),-1.0]])]});}
            var Q65;
            {var subQ0=sQuery(id+"F7.wireOp",EDGE,"E170.MirrorCS");Q65=makeQuery(id+"F7.imprint","IMPRINT",FACE,{"disambiguationData":[TD([[makeQuery(id+"F7.imprint","IMPRINT",EDGE,{"derivedFrom":subQ0}),1.0]])]});}
            var Q66;
            {var subQ0=sQuery(id+"F7.wireOp",EDGE,"E166.MirrorCS");Q66=makeQuery(id+"F7.imprint","IMPRINT",FACE,{"disambiguationData":[TD([[makeQuery(id+"F7.imprint","IMPRINT",EDGE,{"derivedFrom":subQ0}),1.0]])]});}
            var Q67;
            {var subQ0=sQuery(id+"F7.wireOp",EDGE,"E172.MirrorCS");Q67=makeQuery(id+"F7.imprint","IMPRINT",FACE,{"disambiguationData":[TD([[makeQuery(id+"F7.imprint","IMPRINT",EDGE,{"derivedFrom":subQ0}),1.0]])]});}
            var Q68;
            {var subQ0=sQuery(id+"F7.wireOp",EDGE,"E173.MirrorCS");Q68=makeQuery(id+"F7.imprint","IMPRINT",FACE,{"disambiguationData":[TD([[makeQuery(id+"F7.imprint","IMPRINT",EDGE,{"derivedFrom":subQ0}),-1.0]])]});}
            var Q69;
            {var subQ0=sQuery(id+"F7.wireOp",EDGE,"E174.MirrorCS");Q69=makeQuery(id+"F7.imprint","IMPRINT",FACE,{"disambiguationData":[TD([[makeQuery(id+"F7.imprint","IMPRINT",EDGE,{"derivedFrom":subQ0}),1.0]])]});}
            var Q70;
            {var subQ0=sQuery(id+"F7.wireOp",EDGE,"E177.MirrorCS");Q70=makeQuery(id+"F7.imprint","IMPRINT",FACE,{"disambiguationData":[TD([[makeQuery(id+"F7.imprint","IMPRINT",EDGE,{"derivedFrom":subQ0}),-1.0]])]});}
            var Q71;
            {var subQ0=sQuery(id+"F7.wireOp",EDGE,"E178.MirrorCS");Q71=makeQuery(id+"F7.imprint","IMPRINT",FACE,{"disambiguationData":[TD([[makeQuery(id+"F7.imprint","IMPRINT",EDGE,{"derivedFrom":subQ0}),1.0]])]});}
            var Q72;
            {var subQ0=sQuery(id+"F7.wireOp",EDGE,"E180.MirrorCS");Q72=makeQuery(id+"F7.imprint","IMPRINT",FACE,{"disambiguationData":[TD([[makeQuery(id+"F7.imprint","IMPRINT",EDGE,{"derivedFrom":subQ0}),1.0]])]});}
            var Q73;
            {var subQ0=sQuery(id+"F7.wireOp",EDGE,"E181.MirrorCS");Q73=makeQuery(id+"F7.imprint","IMPRINT",FACE,{"disambiguationData":[TD([[makeQuery(id+"F7.imprint","IMPRINT",EDGE,{"derivedFrom":subQ0}),-1.0]])]});}
            var Q74;
            {var subQ0=sQuery(id+"F7.wireOp",EDGE,"E182.MirrorCS");Q74=makeQuery(id+"F7.imprint","IMPRINT",FACE,{"disambiguationData":[TD([[makeQuery(id+"F7.imprint","IMPRINT",EDGE,{"derivedFrom":subQ0}),1.0]])]});}
            var Q75;
            {var subQ0=sQuery(id+"F7.wireOp",EDGE,"E184.MirrorCS");Q75=makeQuery(id+"F7.imprint","IMPRINT",FACE,{"disambiguationData":[TD([[makeQuery(id+"F7.imprint","IMPRINT",EDGE,{"derivedFrom":subQ0}),1.0]])]});}
            var Q76;
            {var subQ0=sQuery(id+"F7.wireOp",EDGE,"E185.MirrorCS");Q76=makeQuery(id+"F7.imprint","IMPRINT",FACE,{"disambiguationData":[TD([[makeQuery(id+"F7.imprint","IMPRINT",EDGE,{"derivedFrom":subQ0}),-1.0]])]});}
            var Q77;
            {var subQ0=sQuery(id+"F7.wireOp",EDGE,"E186.MirrorCS");Q77=makeQuery(id+"F7.imprint","IMPRINT",FACE,{"disambiguationData":[TD([[makeQuery(id+"F7.imprint","IMPRINT",EDGE,{"derivedFrom":subQ0}),1.0]])]});}
            var Q78;
            {var subQ0=sQuery(id+"F7.wireOp",EDGE,"E188.MirrorCS");Q78=makeQuery(id+"F7.imprint","IMPRINT",FACE,{"disambiguationData":[TD([[makeQuery(id+"F7.imprint","IMPRINT",EDGE,{"derivedFrom":subQ0}),1.0]])]});}
            var Q79;
            {var subQ0=sQuery(id+"F7.wireOp",EDGE,"E189.MirrorCS");Q79=makeQuery(id+"F7.imprint","IMPRINT",FACE,{"disambiguationData":[TD([[makeQuery(id+"F7.imprint","IMPRINT",EDGE,{"derivedFrom":subQ0}),-1.0]])]});}
            var Q80;
            {var subQ0=sQuery(id+"F7.wireOp",EDGE,"E190.MirrorCS");Q80=makeQuery(id+"F7.imprint","IMPRINT",FACE,{"disambiguationData":[TD([[makeQuery(id+"F7.imprint","IMPRINT",EDGE,{"derivedFrom":subQ0}),1.0]])]});}
            var Q81;
            {var subQ0=sQuery(id+"F7.wireOp",EDGE,"E192.MirrorCS");Q81=makeQuery(id+"F7.imprint","IMPRINT",FACE,{"disambiguationData":[TD([[makeQuery(id+"F7.imprint","IMPRINT",EDGE,{"derivedFrom":subQ0}),1.0]])]});}
            var Q82;
            {var subQ0=sQuery(id+"F7.wireOp",EDGE,"E193.MirrorCS");Q82=makeQuery(id+"F7.imprint","IMPRINT",FACE,{"disambiguationData":[TD([[makeQuery(id+"F7.imprint","IMPRINT",EDGE,{"derivedFrom":subQ0}),-1.0]])]});}
            var Q83;
            {var subQ0=sQuery(id+"F7.wireOp",EDGE,"E197.MirrorCS");Q83=makeQuery(id+"F7.imprint","IMPRINT",FACE,{"disambiguationData":[TD([[makeQuery(id+"F7.imprint","IMPRINT",EDGE,{"derivedFrom":subQ0}),-1.0]])]});}
            var Q84;
            {var subQ0=sQuery(id+"F7.wireOp",EDGE,"E198.MirrorCS");Q84=makeQuery(id+"F7.imprint","IMPRINT",FACE,{"disambiguationData":[TD([[makeQuery(id+"F7.imprint","IMPRINT",EDGE,{"derivedFrom":subQ0}),1.0]])]});}
            var Q85;
            {var subQ0=sQuery(id+"F7.wireOp",EDGE,"E202.MirrorCS");Q85=makeQuery(id+"F7.imprint","IMPRINT",FACE,{"disambiguationData":[TD([[makeQuery(id+"F7.imprint","IMPRINT",EDGE,{"derivedFrom":subQ0}),1.0]])]});}
            var Q86;
            {var subQ0=sQuery(id+"F7.wireOp",EDGE,"E196.MirrorCS");Q86=makeQuery(id+"F7.imprint","IMPRINT",FACE,{"disambiguationData":[TD([[makeQuery(id+"F7.imprint","IMPRINT",EDGE,{"derivedFrom":subQ0}),1.0]])]});}
            var Q87;
            {var subQ0=sQuery(id+"F7.wireOp",EDGE,"E200.MirrorCS");Q87=makeQuery(id+"F7.imprint","IMPRINT",FACE,{"disambiguationData":[TD([[makeQuery(id+"F7.imprint","IMPRINT",EDGE,{"derivedFrom":subQ0}),1.0]])]});}
            var Q88;
            {var subQ0=sQuery(id+"F7.wireOp",EDGE,"E201.MirrorCS");Q88=makeQuery(id+"F7.imprint","IMPRINT",FACE,{"disambiguationData":[TD([[makeQuery(id+"F7.imprint","IMPRINT",EDGE,{"derivedFrom":subQ0}),-1.0]])]});}
            var Q89;
            {var subQ0=sQuery(id+"F7.wireOp",EDGE,"E204.MirrorCS");Q89=makeQuery(id+"F7.imprint","IMPRINT",FACE,{"disambiguationData":[TD([[makeQuery(id+"F7.imprint","IMPRINT",EDGE,{"derivedFrom":subQ0}),1.0]])]});}
            var Q90;
            {var subQ0=sQuery(id+"F7.wireOp",EDGE,"E208.MirrorCS");Q90=makeQuery(id+"F7.imprint","IMPRINT",FACE,{"disambiguationData":[TD([[makeQuery(id+"F7.imprint","IMPRINT",EDGE,{"derivedFrom":subQ0}),1.0]])]});}
            var Q91;
            {var subQ0=sQuery(id+"F7.wireOp",EDGE,"E209.MirrorCS");Q91=makeQuery(id+"F7.imprint","IMPRINT",FACE,{"disambiguationData":[TD([[makeQuery(id+"F7.imprint","IMPRINT",EDGE,{"derivedFrom":subQ0}),-1.0]])]});}
            var Q92;
            {var subQ0=sQuery(id+"F7.wireOp",EDGE,"E210.MirrorCS");Q92=makeQuery(id+"F7.imprint","IMPRINT",FACE,{"disambiguationData":[TD([[makeQuery(id+"F7.imprint","IMPRINT",EDGE,{"derivedFrom":subQ0}),1.0]])]});}
            var Q93;
            {var subQ0=sQuery(id+"F7.wireOp",EDGE,"E212.MirrorCS");Q93=makeQuery(id+"F7.imprint","IMPRINT",FACE,{"disambiguationData":[TD([[makeQuery(id+"F7.imprint","IMPRINT",EDGE,{"derivedFrom":subQ0}),1.0]])]});}
            var Q94;
            {var subQ0=sQuery(id+"F7.wireOp",EDGE,"E213.MirrorCS");Q94=makeQuery(id+"F7.imprint","IMPRINT",FACE,{"disambiguationData":[TD([[makeQuery(id+"F7.imprint","IMPRINT",EDGE,{"derivedFrom":subQ0}),-1.0]])]});}
            var Q95;
            {var subQ0=sQuery(id+"F7.wireOp",EDGE,"E214.MirrorCS");Q95=makeQuery(id+"F7.imprint","IMPRINT",FACE,{"disambiguationData":[TD([[makeQuery(id+"F7.imprint","IMPRINT",EDGE,{"derivedFrom":subQ0}),1.0]])]});}
            var Q96;
            {var subQ0=sQuery(id+"F7.wireOp",EDGE,"E217.MirrorCS");Q96=makeQuery(id+"F7.imprint","IMPRINT",FACE,{"disambiguationData":[TD([[makeQuery(id+"F7.imprint","IMPRINT",EDGE,{"derivedFrom":subQ0}),-1.0]])]});}
            var Q97;
            {var subQ0=sQuery(id+"F7.wireOp",EDGE,"E218.MirrorCS");Q97=makeQuery(id+"F7.imprint","IMPRINT",FACE,{"disambiguationData":[TD([[makeQuery(id+"F7.imprint","IMPRINT",EDGE,{"derivedFrom":subQ0}),1.0]])]});}
            var Q98;
            {var subQ0=sQuery(id+"F7.wireOp",EDGE,"E220.MirrorCS");Q98=makeQuery(id+"F7.imprint","IMPRINT",FACE,{"disambiguationData":[TD([[makeQuery(id+"F7.imprint","IMPRINT",EDGE,{"derivedFrom":subQ0}),1.0]])]});}
            var Q99;
            {var subQ0=sQuery(id+"F7.wireOp",EDGE,"E221.MirrorCS");Q99=makeQuery(id+"F7.imprint","IMPRINT",FACE,{"disambiguationData":[TD([[makeQuery(id+"F7.imprint","IMPRINT",EDGE,{"derivedFrom":subQ0}),-1.0]])]});}
            var Q100;
            {var subQ0=sQuery(id+"F7.wireOp",EDGE,"E222.MirrorCS");Q100=makeQuery(id+"F7.imprint","IMPRINT",FACE,{"disambiguationData":[TD([[makeQuery(id+"F7.imprint","IMPRINT",EDGE,{"derivedFrom":subQ0}),1.0]])]});}
            var Q101;
            {var subQ0=sQuery(id+"F7.wireOp",EDGE,"E224.MirrorCS");Q101=makeQuery(id+"F7.imprint","IMPRINT",FACE,{"disambiguationData":[TD([[makeQuery(id+"F7.imprint","IMPRINT",EDGE,{"derivedFrom":subQ0}),1.0]])]});}
            var Q102;
            {var subQ0=sQuery(id+"F7.wireOp",EDGE,"E225.MirrorCS");Q102=makeQuery(id+"F7.imprint","IMPRINT",FACE,{"disambiguationData":[TD([[makeQuery(id+"F7.imprint","IMPRINT",EDGE,{"derivedFrom":subQ0}),-1.0]])]});}
            var Q103;
            {var subQ0=sQuery(id+"F7.wireOp",EDGE,"E226.MirrorCS");Q103=makeQuery(id+"F7.imprint","IMPRINT",FACE,{"disambiguationData":[TD([[makeQuery(id+"F7.imprint","IMPRINT",EDGE,{"derivedFrom":subQ0}),1.0]])]});}
            var Q104;
            {var subQ0=sQuery(id+"F7.wireOp",EDGE,"E228.MirrorCS");Q104=makeQuery(id+"F7.imprint","IMPRINT",FACE,{"disambiguationData":[TD([[makeQuery(id+"F7.imprint","IMPRINT",EDGE,{"derivedFrom":subQ0}),1.0]])]});}
            var Q105;
            {var subQ0=sQuery(id+"F7.wireOp",EDGE,"E229.MirrorCS");Q105=makeQuery(id+"F7.imprint","IMPRINT",FACE,{"disambiguationData":[TD([[makeQuery(id+"F7.imprint","IMPRINT",EDGE,{"derivedFrom":subQ0}),-1.0]])]});}
            var Q106;
            {var subQ0=sQuery(id+"F7.wireOp",EDGE,"E230.MirrorCS");Q106=makeQuery(id+"F7.imprint","IMPRINT",FACE,{"disambiguationData":[TD([[makeQuery(id+"F7.imprint","IMPRINT",EDGE,{"derivedFrom":subQ0}),1.0]])]});}
            var Q107;
            {var subQ0=sQuery(id+"F7.wireOp",EDGE,"E232.MirrorCS");Q107=makeQuery(id+"F7.imprint","IMPRINT",FACE,{"disambiguationData":[TD([[makeQuery(id+"F7.imprint","IMPRINT",EDGE,{"derivedFrom":subQ0}),1.0]])]});}
            var Q108;
            {var subQ0=sQuery(id+"F7.wireOp",EDGE,"E233.MirrorCS");Q108=makeQuery(id+"F7.imprint","IMPRINT",FACE,{"disambiguationData":[TD([[makeQuery(id+"F7.imprint","IMPRINT",EDGE,{"derivedFrom":subQ0}),-1.0]])]});}
            var Q109;
            {var subQ0=sQuery(id+"F7.wireOp",EDGE,"E237.MirrorCS");Q109=makeQuery(id+"F7.imprint","IMPRINT",FACE,{"disambiguationData":[TD([[makeQuery(id+"F7.imprint","IMPRINT",EDGE,{"derivedFrom":subQ0}),-1.0]])]});}
            var Q110;
            {var subQ0=sQuery(id+"F7.wireOp",EDGE,"E238.MirrorCS");Q110=makeQuery(id+"F7.imprint","IMPRINT",FACE,{"disambiguationData":[TD([[makeQuery(id+"F7.imprint","IMPRINT",EDGE,{"derivedFrom":subQ0}),1.0]])]});}
            var Q111;
            {var subQ0=sQuery(id+"F7.wireOp",EDGE,"E242.MirrorCS");Q111=makeQuery(id+"F7.imprint","IMPRINT",FACE,{"disambiguationData":[TD([[makeQuery(id+"F7.imprint","IMPRINT",EDGE,{"derivedFrom":subQ0}),1.0]])]});}
            var Q112;
            {var subQ0=sQuery(id+"F7.wireOp",EDGE,"E244.MirrorCS");Q112=makeQuery(id+"F7.imprint","IMPRINT",FACE,{"disambiguationData":[TD([[makeQuery(id+"F7.imprint","IMPRINT",EDGE,{"derivedFrom":subQ0}),1.0]])]});}
            var Q113;
            {var subQ0=sQuery(id+"F7.wireOp",EDGE,"E245.MirrorCS");Q113=makeQuery(id+"F7.imprint","IMPRINT",FACE,{"disambiguationData":[TD([[makeQuery(id+"F7.imprint","IMPRINT",EDGE,{"derivedFrom":subQ0}),-1.0]])]});}
            var Q114;
            {var subQ0=sQuery(id+"F7.wireOp",EDGE,"E246.MirrorCS");Q114=makeQuery(id+"F7.imprint","IMPRINT",FACE,{"disambiguationData":[TD([[makeQuery(id+"F7.imprint","IMPRINT",EDGE,{"derivedFrom":subQ0}),1.0]])]});}
            var Q115;
            {var subQ0=sQuery(id+"F7.wireOp",EDGE,"E248.MirrorCS");Q115=makeQuery(id+"F7.imprint","IMPRINT",FACE,{"disambiguationData":[TD([[makeQuery(id+"F7.imprint","IMPRINT",EDGE,{"derivedFrom":subQ0}),1.0]])]});}
            var Q116;
            {var subQ0=sQuery(id+"F7.wireOp",EDGE,"E249.MirrorCS");Q116=makeQuery(id+"F7.imprint","IMPRINT",FACE,{"disambiguationData":[TD([[makeQuery(id+"F7.imprint","IMPRINT",EDGE,{"derivedFrom":subQ0}),-1.0]])]});}
            var Q117;
            {var subQ0=sQuery(id+"F7.wireOp",EDGE,"E250.MirrorCS");Q117=makeQuery(id+"F7.imprint","IMPRINT",FACE,{"disambiguationData":[TD([[makeQuery(id+"F7.imprint","IMPRINT",EDGE,{"derivedFrom":subQ0}),1.0]])]});}
            var Q118;
            {var subQ0=sQuery(id+"F7.wireOp",EDGE,"E252.MirrorCS");Q118=makeQuery(id+"F7.imprint","IMPRINT",FACE,{"disambiguationData":[TD([[makeQuery(id+"F7.imprint","IMPRINT",EDGE,{"derivedFrom":subQ0}),1.0]])]});}
            var Q119;
            {var subQ0=sQuery(id+"F7.wireOp",EDGE,"E253.MirrorCS");Q119=makeQuery(id+"F7.imprint","IMPRINT",FACE,{"disambiguationData":[TD([[makeQuery(id+"F7.imprint","IMPRINT",EDGE,{"derivedFrom":subQ0}),-1.0]])]});}
            var Q120;
            {var subQ0=sQuery(id+"F7.wireOp",EDGE,"E254.MirrorCS");Q120=makeQuery(id+"F7.imprint","IMPRINT",FACE,{"disambiguationData":[TD([[makeQuery(id+"F7.imprint","IMPRINT",EDGE,{"derivedFrom":subQ0}),1.0]])]});}
            var Q121;
            {var subQ0=sQuery(id+"F7.wireOp",EDGE,"E257.MirrorCS");Q121=makeQuery(id+"F7.imprint","IMPRINT",FACE,{"disambiguationData":[TD([[makeQuery(id+"F7.imprint","IMPRINT",EDGE,{"derivedFrom":subQ0}),-1.0]])]});}
            var Q122;
            {var subQ0=sQuery(id+"F7.wireOp",EDGE,"E258.MirrorCS");Q122=makeQuery(id+"F7.imprint","IMPRINT",FACE,{"disambiguationData":[TD([[makeQuery(id+"F7.imprint","IMPRINT",EDGE,{"derivedFrom":subQ0}),1.0]])]});}
            var Q123;
            {var subQ0=sQuery(id+"F7.wireOp",EDGE,"E194.MirrorCS");Q123=makeQuery(id+"F7.imprint","IMPRINT",FACE,{"disambiguationData":[TD([[makeQuery(id+"F7.imprint","IMPRINT",EDGE,{"derivedFrom":subQ0}),1.0]])]});}
            var Q124;
            {var subQ0=sQuery(id+"F7.wireOp",EDGE,"E205.MirrorCS");Q124=makeQuery(id+"F7.imprint","IMPRINT",FACE,{"disambiguationData":[TD([[makeQuery(id+"F7.imprint","IMPRINT",EDGE,{"derivedFrom":subQ0}),-1.0]])]});}
            var Q125;
            {var subQ0=sQuery(id+"F7.wireOp",EDGE,"E206.MirrorCS");Q125=makeQuery(id+"F7.imprint","IMPRINT",FACE,{"disambiguationData":[TD([[makeQuery(id+"F7.imprint","IMPRINT",EDGE,{"derivedFrom":subQ0}),1.0]])]});}
            var Q126;
            {var subQ0=sQuery(id+"F7.wireOp",EDGE,"E216.MirrorCS");Q126=makeQuery(id+"F7.imprint","IMPRINT",FACE,{"disambiguationData":[TD([[makeQuery(id+"F7.imprint","IMPRINT",EDGE,{"derivedFrom":subQ0}),1.0]])]});}
            var Q127;
            {var subQ0=sQuery(id+"F7.wireOp",EDGE,"E234.MirrorCS");Q127=makeQuery(id+"F7.imprint","IMPRINT",FACE,{"disambiguationData":[TD([[makeQuery(id+"F7.imprint","IMPRINT",EDGE,{"derivedFrom":subQ0}),1.0]])]});}
            var Q128;
            {var subQ0=sQuery(id+"F7.wireOp",EDGE,"E236.MirrorCS");Q128=makeQuery(id+"F7.imprint","IMPRINT",FACE,{"disambiguationData":[TD([[makeQuery(id+"F7.imprint","IMPRINT",EDGE,{"derivedFrom":subQ0}),1.0]])]});}
            var Q129;
            {var subQ0=sQuery(id+"F7.wireOp",EDGE,"E241.MirrorCS");Q129=makeQuery(id+"F7.imprint","IMPRINT",FACE,{"disambiguationData":[TD([[makeQuery(id+"F7.imprint","IMPRINT",EDGE,{"derivedFrom":subQ0}),-1.0]])]});}
            var Q130;
            {var subQ0=sQuery(id+"F7.wireOp",EDGE,"E300.MirrorCS");Q130=makeQuery(id+"F7.imprint","IMPRINT",FACE,{"disambiguationData":[TD([[makeQuery(id+"F7.imprint","IMPRINT",EDGE,{"derivedFrom":subQ0}),-1.0]])]});}
            var Q131;
            {var subQ0=sQuery(id+"F7.wireOp",EDGE,"E299.MirrorCS");Q131=makeQuery(id+"F7.imprint","IMPRINT",FACE,{"disambiguationData":[TD([[makeQuery(id+"F7.imprint","IMPRINT",EDGE,{"derivedFrom":subQ0}),1.0]])]});}
            var Q132;
            {var subQ0=sQuery(id+"F7.wireOp",EDGE,"E296.MirrorCS");Q132=makeQuery(id+"F7.imprint","IMPRINT",FACE,{"disambiguationData":[TD([[makeQuery(id+"F7.imprint","IMPRINT",EDGE,{"derivedFrom":subQ0}),-1.0]])]});}
            var Q133;
            {var subQ0=sQuery(id+"F7.wireOp",EDGE,"E295.MirrorCS");Q133=makeQuery(id+"F7.imprint","IMPRINT",FACE,{"disambiguationData":[TD([[makeQuery(id+"F7.imprint","IMPRINT",EDGE,{"derivedFrom":subQ0}),1.0]])]});}
            var Q134;
            {var subQ0=sQuery(id+"F7.wireOp",EDGE,"E292.MirrorCS");Q134=makeQuery(id+"F7.imprint","IMPRINT",FACE,{"disambiguationData":[TD([[makeQuery(id+"F7.imprint","IMPRINT",EDGE,{"derivedFrom":subQ0}),-1.0]])]});}
            var Q135;
            {var subQ0=sQuery(id+"F7.wireOp",EDGE,"E288.MirrorCS");Q135=makeQuery(id+"F7.imprint","IMPRINT",FACE,{"disambiguationData":[TD([[makeQuery(id+"F7.imprint","IMPRINT",EDGE,{"derivedFrom":subQ0}),-1.0]])]});}
            var Q136;
            {var subQ0=sQuery(id+"F7.wireOp",EDGE,"E287.MirrorCS");Q136=makeQuery(id+"F7.imprint","IMPRINT",FACE,{"disambiguationData":[TD([[makeQuery(id+"F7.imprint","IMPRINT",EDGE,{"derivedFrom":subQ0}),1.0]])]});}
            var Q137;
            {var subQ0=sQuery(id+"F7.wireOp",EDGE,"E284.MirrorCS");Q137=makeQuery(id+"F7.imprint","IMPRINT",FACE,{"disambiguationData":[TD([[makeQuery(id+"F7.imprint","IMPRINT",EDGE,{"derivedFrom":subQ0}),-1.0]])]});}
            var Q138;
            {var subQ0=sQuery(id+"F7.wireOp",EDGE,"E283.MirrorCS");Q138=makeQuery(id+"F7.imprint","IMPRINT",FACE,{"disambiguationData":[TD([[makeQuery(id+"F7.imprint","IMPRINT",EDGE,{"derivedFrom":subQ0}),1.0]])]});}
            var Q139;
            {var subQ0=sQuery(id+"F7.wireOp",EDGE,"E280.MirrorCS");Q139=makeQuery(id+"F7.imprint","IMPRINT",FACE,{"disambiguationData":[TD([[makeQuery(id+"F7.imprint","IMPRINT",EDGE,{"derivedFrom":subQ0}),-1.0]])]});}
            var Q140;
            {var subQ0=sQuery(id+"F7.wireOp",EDGE,"E279.MirrorCS");Q140=makeQuery(id+"F7.imprint","IMPRINT",FACE,{"disambiguationData":[TD([[makeQuery(id+"F7.imprint","IMPRINT",EDGE,{"derivedFrom":subQ0}),1.0]])]});}
            var Q141;
            {var subQ0=sQuery(id+"F7.wireOp",EDGE,"E276.MirrorCS");Q141=makeQuery(id+"F7.imprint","IMPRINT",FACE,{"disambiguationData":[TD([[makeQuery(id+"F7.imprint","IMPRINT",EDGE,{"derivedFrom":subQ0}),-1.0]])]});}
            var Q142;
            {var subQ0=sQuery(id+"F7.wireOp",EDGE,"E275.MirrorCS");Q142=makeQuery(id+"F7.imprint","IMPRINT",FACE,{"disambiguationData":[TD([[makeQuery(id+"F7.imprint","IMPRINT",EDGE,{"derivedFrom":subQ0}),1.0]])]});}
            var Q143;
            {var subQ0=sQuery(id+"F7.wireOp",EDGE,"E272.MirrorCS");Q143=makeQuery(id+"F7.imprint","IMPRINT",FACE,{"disambiguationData":[TD([[makeQuery(id+"F7.imprint","IMPRINT",EDGE,{"derivedFrom":subQ0}),-1.0]])]});}
            var Q144;
            {var subQ0=sQuery(id+"F7.wireOp",EDGE,"E240.MirrorCS");Q144=makeQuery(id+"F7.imprint","IMPRINT",FACE,{"disambiguationData":[TD([[makeQuery(id+"F7.imprint","IMPRINT",EDGE,{"derivedFrom":subQ0}),1.0]])]});}
            var Q145;
            {var subQ0=sQuery(id+"F7.wireOp",EDGE,"E256.MirrorCS");Q145=makeQuery(id+"F7.imprint","IMPRINT",FACE,{"disambiguationData":[TD([[makeQuery(id+"F7.imprint","IMPRINT",EDGE,{"derivedFrom":subQ0}),1.0]])]});}
            var Q146;
            {var subQ0=sQuery(id+"F7.wireOp",EDGE,"E301.MirrorCS");Q146=makeQuery(id+"F7.imprint","IMPRINT",FACE,{"disambiguationData":[TD([[makeQuery(id+"F7.imprint","IMPRINT",EDGE,{"derivedFrom":subQ0}),1.0]])]});}
            var Q147;
            {var subQ0=sQuery(id+"F7.wireOp",EDGE,"E297.MirrorCS");Q147=makeQuery(id+"F7.imprint","IMPRINT",FACE,{"disambiguationData":[TD([[makeQuery(id+"F7.imprint","IMPRINT",EDGE,{"derivedFrom":subQ0}),1.0]])]});}
            var Q148;
            {var subQ0=sQuery(id+"F7.wireOp",EDGE,"E293.MirrorCS");Q148=makeQuery(id+"F7.imprint","IMPRINT",FACE,{"disambiguationData":[TD([[makeQuery(id+"F7.imprint","IMPRINT",EDGE,{"derivedFrom":subQ0}),1.0]])]});}
            var Q149;
            {var subQ0=sQuery(id+"F7.wireOp",EDGE,"E291.MirrorCS");Q149=makeQuery(id+"F7.imprint","IMPRINT",FACE,{"disambiguationData":[TD([[makeQuery(id+"F7.imprint","IMPRINT",EDGE,{"derivedFrom":subQ0}),1.0]])]});}
            var Q150;
            {var subQ0=sQuery(id+"F7.wireOp",EDGE,"E289.MirrorCS");Q150=makeQuery(id+"F7.imprint","IMPRINT",FACE,{"disambiguationData":[TD([[makeQuery(id+"F7.imprint","IMPRINT",EDGE,{"derivedFrom":subQ0}),1.0]])]});}
            var Q151;
            {var subQ0=sQuery(id+"F7.wireOp",EDGE,"E285.MirrorCS");Q151=makeQuery(id+"F7.imprint","IMPRINT",FACE,{"disambiguationData":[TD([[makeQuery(id+"F7.imprint","IMPRINT",EDGE,{"derivedFrom":subQ0}),1.0]])]});}
            var Q152;
            {var subQ0=sQuery(id+"F7.wireOp",EDGE,"E281.MirrorCS");Q152=makeQuery(id+"F7.imprint","IMPRINT",FACE,{"disambiguationData":[TD([[makeQuery(id+"F7.imprint","IMPRINT",EDGE,{"derivedFrom":subQ0}),1.0]])]});}
            var Q153;
            {var subQ0=sQuery(id+"F7.wireOp",EDGE,"E277.MirrorCS");Q153=makeQuery(id+"F7.imprint","IMPRINT",FACE,{"disambiguationData":[TD([[makeQuery(id+"F7.imprint","IMPRINT",EDGE,{"derivedFrom":subQ0}),1.0]])]});}
            var Q154;
            {var subQ0=sQuery(id+"F7.wireOp",EDGE,"E273.MirrorCS");Q154=makeQuery(id+"F7.imprint","IMPRINT",FACE,{"disambiguationData":[TD([[makeQuery(id+"F7.imprint","IMPRINT",EDGE,{"derivedFrom":subQ0}),1.0]])]});}
            var Q155;
            {var subQ0=sQuery(id+"F7.wireOp",EDGE,"E271.MirrorCS");Q155=makeQuery(id+"F7.imprint","IMPRINT",FACE,{"disambiguationData":[TD([[makeQuery(id+"F7.imprint","IMPRINT",EDGE,{"derivedFrom":subQ0}),1.0]])]});}
            var Q156;
            {var subQ0=sQuery(id+"F7.wireOp",EDGE,"E269.MirrorCS");Q156=makeQuery(id+"F7.imprint","IMPRINT",FACE,{"disambiguationData":[TD([[makeQuery(id+"F7.imprint","IMPRINT",EDGE,{"derivedFrom":subQ0}),1.0]])]});}
            var Q157;
            {var subQ0=sQuery(id+"F7.wireOp",EDGE,"E268.MirrorCS");Q157=makeQuery(id+"F7.imprint","IMPRINT",FACE,{"disambiguationData":[TD([[makeQuery(id+"F7.imprint","IMPRINT",EDGE,{"derivedFrom":subQ0}),-1.0]])]});}
            var Q158;
            {var subQ0=sQuery(id+"F7.wireOp",EDGE,"E267.MirrorCS");Q158=makeQuery(id+"F7.imprint","IMPRINT",FACE,{"disambiguationData":[TD([[makeQuery(id+"F7.imprint","IMPRINT",EDGE,{"derivedFrom":subQ0}),1.0]])]});}
            var Q159;
            {var subQ0=sQuery(id+"F7.wireOp",EDGE,"E265.MirrorCS");Q159=makeQuery(id+"F7.imprint","IMPRINT",FACE,{"disambiguationData":[TD([[makeQuery(id+"F7.imprint","IMPRINT",EDGE,{"derivedFrom":subQ0}),1.0]])]});}
            var Q160;
            {var subQ0=sQuery(id+"F7.wireOp",EDGE,"E264.MirrorCS");Q160=makeQuery(id+"F7.imprint","IMPRINT",FACE,{"disambiguationData":[TD([[makeQuery(id+"F7.imprint","IMPRINT",EDGE,{"derivedFrom":subQ0}),-1.0]])]});}
            var Q161;
            {var subQ0=sQuery(id+"F7.wireOp",EDGE,"E263.MirrorCS");Q161=makeQuery(id+"F7.imprint","IMPRINT",FACE,{"disambiguationData":[TD([[makeQuery(id+"F7.imprint","IMPRINT",EDGE,{"derivedFrom":subQ0}),1.0]])]});}
            var Q162;
            {var subQ0=sQuery(id+"F7.wireOp",EDGE,"E261.MirrorCS");Q162=makeQuery(id+"F7.imprint","IMPRINT",FACE,{"disambiguationData":[TD([[makeQuery(id+"F7.imprint","IMPRINT",EDGE,{"derivedFrom":subQ0}),1.0]])]});}
            var Q163;
            {var subQ0=sQuery(id+"F7.wireOp",EDGE,"E260.MirrorCS");Q163=makeQuery(id+"F7.imprint","IMPRINT",FACE,{"disambiguationData":[TD([[makeQuery(id+"F7.imprint","IMPRINT",EDGE,{"derivedFrom":subQ0}),-1.0]])]});}
            var Q164;
            {var subQ0=sQuery(id+"F7.wireOp",EDGE,"E259.MirrorCS");Q164=makeQuery(id+"F7.imprint","IMPRINT",FACE,{"disambiguationData":[TD([[makeQuery(id+"F7.imprint","IMPRINT",EDGE,{"derivedFrom":subQ0}),1.0]])]});}
            var Q165;
            {var subQ0=sQuery(id+"F7.wireOp",EDGE,"E80.top");Q165=makeQuery(id+"F7.imprint","IMPRINT",FACE,{"disambiguationData":[TD([[makeQuery(id+"F7.imprint","IMPRINT",EDGE,{"derivedFrom":subQ0}),-1.0]])]});}
            var Q166;
            {var subQ0=sQuery(id+"F7.wireOp",EDGE,"E176.MirrorCS");Q166=makeQuery(id+"F7.imprint","IMPRINT",FACE,{"disambiguationData":[TD([[makeQuery(id+"F7.imprint","IMPRINT",EDGE,{"derivedFrom":subQ0}),1.0]])]});}
            var Q167;
            {var subQ0=sQuery(id+"F7.wireOp",EDGE,"E304.MirrorCS");Q167=makeQuery(id+"F7.imprint","IMPRINT",FACE,{"disambiguationData":[TD([[makeQuery(id+"F7.imprint","IMPRINT",EDGE,{"derivedFrom":subQ0}),1.0]])]});}
            extrude(context, id + "F11", {"entities" : qUnion([Q0, Q1, Q2, Q3, Q4, Q5, Q6, Q7, Q8, Q9, Q10, Q11, Q12, Q13, Q14, Q15, Q16, Q17, Q18, Q19, Q20, Q21, Q22, Q23, Q24, Q25, Q26, Q27, Q28, Q29, Q30, Q31, Q32, Q33, Q34, Q35, Q36, Q37, Q38, Q39, Q40, Q41, Q42, Q43, Q44, Q45, Q46, Q47, Q48, Q49, Q50, Q51, Q52, Q53, Q54, Q55, Q56, Q57, Q58, Q59, Q60, Q61, Q62, Q63, Q64, Q65, Q66, Q67, Q68, Q69, Q70, Q71, Q72, Q73, Q74, Q75, Q76, Q77, Q78, Q79, Q80, Q81, Q82, Q83, Q84, Q85, Q86, Q87, Q88, Q89, Q90, Q91, Q92, Q93, Q94, Q95, Q96, Q97, Q98, Q99, Q100, Q101, Q102, Q103, Q104, Q105, Q106, Q107, Q108, Q109, Q110, Q111, Q112, Q113, Q114, Q115, Q116, Q117, Q118, Q119, Q120, Q121, Q122, Q123, Q124, Q125, Q126, Q127, Q128, Q129, Q130, Q131, Q132, Q133, Q134, Q135, Q136, Q137, Q138, Q139, Q140, Q141, Q142, Q143, Q144, Q145, Q146, Q147, Q148, Q149, Q150, Q151, Q152, Q153, Q154, Q155, Q156, Q157, Q158, Q159, Q160, Q161, Q162, Q163, Q164, Q165, Q166, Q167]), "depth" : 3 * mm, "offsetDistance" : 25 * mm});
        }
        {
            var Q0;
            {var subQ154=sQuery(id+"F7.wireOp",EDGE,"E82.bottom");Q0=makeQuery(id+"F7.imprint","IMPRINT",FACE,{"disambiguationData":[TD([[makeQuery(id+"F7.imprint","IMPRINT",EDGE,{"derivedFrom":subQ154}),1.0]])]});}
            var Q1;
            {var subQ0=sQuery(id+"F7.wireOp",EDGE,"E84.MirrorCS");Q1=makeQuery(id+"F7.imprint","IMPRINT",FACE,{"disambiguationData":[TD([[makeQuery(id+"F7.imprint","IMPRINT",EDGE,{"derivedFrom":subQ0}),-1.0]])]});}
            var Q2;
            {var subQ0=sQuery(id+"F7.wireOp",EDGE,"E88.MirrorCS");Q2=makeQuery(id+"F7.imprint","IMPRINT",FACE,{"disambiguationData":[TD([[makeQuery(id+"F7.imprint","IMPRINT",EDGE,{"derivedFrom":subQ0}),-1.0]])]});}
            var Q3;
            {var subQ0=sQuery(id+"F7.wireOp",EDGE,"E92.MirrorCS");Q3=makeQuery(id+"F7.imprint","IMPRINT",FACE,{"disambiguationData":[TD([[makeQuery(id+"F7.imprint","IMPRINT",EDGE,{"derivedFrom":subQ0}),-1.0]])]});}
            var Q4;
            {var subQ0=sQuery(id+"F7.wireOp",EDGE,"E96.MirrorCS");Q4=makeQuery(id+"F7.imprint","IMPRINT",FACE,{"disambiguationData":[TD([[makeQuery(id+"F7.imprint","IMPRINT",EDGE,{"derivedFrom":subQ0}),-1.0]])]});}
            var Q5;
            {var subQ0=sQuery(id+"F7.wireOp",EDGE,"E100.MirrorCS");Q5=makeQuery(id+"F7.imprint","IMPRINT",FACE,{"disambiguationData":[TD([[makeQuery(id+"F7.imprint","IMPRINT",EDGE,{"derivedFrom":subQ0}),-1.0]])]});}
            var Q6;
            {var subQ0=sQuery(id+"F7.wireOp",EDGE,"E104.MirrorCS");Q6=makeQuery(id+"F7.imprint","IMPRINT",FACE,{"disambiguationData":[TD([[makeQuery(id+"F7.imprint","IMPRINT",EDGE,{"derivedFrom":subQ0}),-1.0]])]});}
            var Q7;
            {var subQ0=sQuery(id+"F7.wireOp",EDGE,"E108.MirrorCS");Q7=makeQuery(id+"F7.imprint","IMPRINT",FACE,{"disambiguationData":[TD([[makeQuery(id+"F7.imprint","IMPRINT",EDGE,{"derivedFrom":subQ0}),-1.0]])]});}
            var Q8;
            {var subQ0=sQuery(id+"F7.wireOp",EDGE,"E112.MirrorCS");Q8=makeQuery(id+"F7.imprint","IMPRINT",FACE,{"disambiguationData":[TD([[makeQuery(id+"F7.imprint","IMPRINT",EDGE,{"derivedFrom":subQ0}),-1.0]])]});}
            var Q9;
            {var subQ0=sQuery(id+"F7.wireOp",EDGE,"E116.MirrorCS");Q9=makeQuery(id+"F7.imprint","IMPRINT",FACE,{"disambiguationData":[TD([[makeQuery(id+"F7.imprint","IMPRINT",EDGE,{"derivedFrom":subQ0}),-1.0]])]});}
            var Q10;
            {var subQ0=sQuery(id+"F7.wireOp",EDGE,"E155.MirrorCS");Q10=makeQuery(id+"F7.imprint","IMPRINT",FACE,{"disambiguationData":[TD([[makeQuery(id+"F7.imprint","IMPRINT",EDGE,{"derivedFrom":subQ0}),-1.0]])]});}
            var Q11;
            {var subQ0=sQuery(id+"F7.wireOp",EDGE,"E151.MirrorCS");Q11=makeQuery(id+"F7.imprint","IMPRINT",FACE,{"disambiguationData":[TD([[makeQuery(id+"F7.imprint","IMPRINT",EDGE,{"derivedFrom":subQ0}),-1.0]])]});}
            var Q12;
            {var subQ0=sQuery(id+"F7.wireOp",EDGE,"E147.MirrorCS");Q12=makeQuery(id+"F7.imprint","IMPRINT",FACE,{"disambiguationData":[TD([[makeQuery(id+"F7.imprint","IMPRINT",EDGE,{"derivedFrom":subQ0}),-1.0]])]});}
            var Q13;
            {var subQ0=sQuery(id+"F7.wireOp",EDGE,"E143.MirrorCS");Q13=makeQuery(id+"F7.imprint","IMPRINT",FACE,{"disambiguationData":[TD([[makeQuery(id+"F7.imprint","IMPRINT",EDGE,{"derivedFrom":subQ0}),-1.0]])]});}
            var Q14;
            {var subQ0=sQuery(id+"F7.wireOp",EDGE,"E140.MirrorCS");Q14=makeQuery(id+"F7.imprint","IMPRINT",FACE,{"disambiguationData":[TD([[makeQuery(id+"F7.imprint","IMPRINT",EDGE,{"derivedFrom":subQ0}),-1.0]])]});}
            var Q15;
            {var subQ0=sQuery(id+"F7.wireOp",EDGE,"E136.MirrorCS");Q15=makeQuery(id+"F7.imprint","IMPRINT",FACE,{"disambiguationData":[TD([[makeQuery(id+"F7.imprint","IMPRINT",EDGE,{"derivedFrom":subQ0}),-1.0]])]});}
            var Q16;
            {var subQ0=sQuery(id+"F7.wireOp",EDGE,"E132.MirrorCS");Q16=makeQuery(id+"F7.imprint","IMPRINT",FACE,{"disambiguationData":[TD([[makeQuery(id+"F7.imprint","IMPRINT",EDGE,{"derivedFrom":subQ0}),-1.0]])]});}
            var Q17;
            {var subQ0=sQuery(id+"F7.wireOp",EDGE,"E128.MirrorCS");Q17=makeQuery(id+"F7.imprint","IMPRINT",FACE,{"disambiguationData":[TD([[makeQuery(id+"F7.imprint","IMPRINT",EDGE,{"derivedFrom":subQ0}),-1.0]])]});}
            var Q18;
            {var subQ0=sQuery(id+"F7.wireOp",EDGE,"E124.MirrorCS");Q18=makeQuery(id+"F7.imprint","IMPRINT",FACE,{"disambiguationData":[TD([[makeQuery(id+"F7.imprint","IMPRINT",EDGE,{"derivedFrom":subQ0}),-1.0]])]});}
            var Q19;
            {var subQ0=sQuery(id+"F7.wireOp",EDGE,"E159.MirrorCS");Q19=makeQuery(id+"F7.imprint","IMPRINT",FACE,{"disambiguationData":[TD([[makeQuery(id+"F7.imprint","IMPRINT",EDGE,{"derivedFrom":subQ0}),-1.0]])]});}
            var Q20;
            {var subQ0=sQuery(id+"F7.wireOp",EDGE,"E163.MirrorCS");Q20=makeQuery(id+"F7.imprint","IMPRINT",FACE,{"disambiguationData":[TD([[makeQuery(id+"F7.imprint","IMPRINT",EDGE,{"derivedFrom":subQ0}),-1.0]])]});}
            var Q21;
            {var subQ0=sQuery(id+"F7.wireOp",EDGE,"E167.MirrorCS");Q21=makeQuery(id+"F7.imprint","IMPRINT",FACE,{"disambiguationData":[TD([[makeQuery(id+"F7.imprint","IMPRINT",EDGE,{"derivedFrom":subQ0}),-1.0]])]});}
            var Q22;
            {var subQ0=sQuery(id+"F7.wireOp",EDGE,"E171.MirrorCS");Q22=makeQuery(id+"F7.imprint","IMPRINT",FACE,{"disambiguationData":[TD([[makeQuery(id+"F7.imprint","IMPRINT",EDGE,{"derivedFrom":subQ0}),-1.0]])]});}
            var Q23;
            {var subQ0=sQuery(id+"F7.wireOp",EDGE,"E175.MirrorCS");Q23=makeQuery(id+"F7.imprint","IMPRINT",FACE,{"disambiguationData":[TD([[makeQuery(id+"F7.imprint","IMPRINT",EDGE,{"derivedFrom":subQ0}),-1.0]])]});}
            var Q24;
            {var subQ0=sQuery(id+"F7.wireOp",EDGE,"E179.MirrorCS");Q24=makeQuery(id+"F7.imprint","IMPRINT",FACE,{"disambiguationData":[TD([[makeQuery(id+"F7.imprint","IMPRINT",EDGE,{"derivedFrom":subQ0}),-1.0]])]});}
            var Q25;
            {var subQ0=sQuery(id+"F7.wireOp",EDGE,"E183.MirrorCS");Q25=makeQuery(id+"F7.imprint","IMPRINT",FACE,{"disambiguationData":[TD([[makeQuery(id+"F7.imprint","IMPRINT",EDGE,{"derivedFrom":subQ0}),-1.0]])]});}
            var Q26;
            {var subQ0=sQuery(id+"F7.wireOp",EDGE,"E187.MirrorCS");Q26=makeQuery(id+"F7.imprint","IMPRINT",FACE,{"disambiguationData":[TD([[makeQuery(id+"F7.imprint","IMPRINT",EDGE,{"derivedFrom":subQ0}),-1.0]])]});}
            var Q27;
            {var subQ0=sQuery(id+"F7.wireOp",EDGE,"E191.MirrorCS");Q27=makeQuery(id+"F7.imprint","IMPRINT",FACE,{"disambiguationData":[TD([[makeQuery(id+"F7.imprint","IMPRINT",EDGE,{"derivedFrom":subQ0}),-1.0]])]});}
            var Q28;
            {var subQ2=sQuery(id+"F7.wireOp",EDGE,"E195.MirrorCS");Q28=makeQuery(id+"F7.imprint","IMPRINT",FACE,{"disambiguationData":[TD([[makeQuery(id+"F7.imprint","IMPRINT",EDGE,{"derivedFrom":subQ2}),-1.0]])]});}
            var Q29;
            {var subQ0=sQuery(id+"F7.wireOp",EDGE,"E199.MirrorCS");Q29=makeQuery(id+"F7.imprint","IMPRINT",FACE,{"disambiguationData":[TD([[makeQuery(id+"F7.imprint","IMPRINT",EDGE,{"derivedFrom":subQ0}),-1.0]])]});}
            var Q30;
            {var subQ0=sQuery(id+"F7.wireOp",EDGE,"E203.MirrorCS");Q30=makeQuery(id+"F7.imprint","IMPRINT",FACE,{"disambiguationData":[TD([[makeQuery(id+"F7.imprint","IMPRINT",EDGE,{"derivedFrom":subQ0}),-1.0]])]});}
            var Q31;
            {var subQ0=sQuery(id+"F7.wireOp",EDGE,"E207.MirrorCS");Q31=makeQuery(id+"F7.imprint","IMPRINT",FACE,{"disambiguationData":[TD([[makeQuery(id+"F7.imprint","IMPRINT",EDGE,{"derivedFrom":subQ0}),-1.0]])]});}
            var Q32;
            {var subQ0=sQuery(id+"F7.wireOp",EDGE,"E211.MirrorCS");Q32=makeQuery(id+"F7.imprint","IMPRINT",FACE,{"disambiguationData":[TD([[makeQuery(id+"F7.imprint","IMPRINT",EDGE,{"derivedFrom":subQ0}),-1.0]])]});}
            var Q33;
            {var subQ0=sQuery(id+"F7.wireOp",EDGE,"E215.MirrorCS");Q33=makeQuery(id+"F7.imprint","IMPRINT",FACE,{"disambiguationData":[TD([[makeQuery(id+"F7.imprint","IMPRINT",EDGE,{"derivedFrom":subQ0}),-1.0]])]});}
            var Q34;
            {var subQ0=sQuery(id+"F7.wireOp",EDGE,"E219.MirrorCS");Q34=makeQuery(id+"F7.imprint","IMPRINT",FACE,{"disambiguationData":[TD([[makeQuery(id+"F7.imprint","IMPRINT",EDGE,{"derivedFrom":subQ0}),-1.0]])]});}
            var Q35;
            {var subQ0=sQuery(id+"F7.wireOp",EDGE,"E223.MirrorCS");Q35=makeQuery(id+"F7.imprint","IMPRINT",FACE,{"disambiguationData":[TD([[makeQuery(id+"F7.imprint","IMPRINT",EDGE,{"derivedFrom":subQ0}),-1.0]])]});}
            var Q36;
            {var subQ0=sQuery(id+"F7.wireOp",EDGE,"E227.MirrorCS");Q36=makeQuery(id+"F7.imprint","IMPRINT",FACE,{"disambiguationData":[TD([[makeQuery(id+"F7.imprint","IMPRINT",EDGE,{"derivedFrom":subQ0}),-1.0]])]});}
            var Q37;
            {var subQ0=sQuery(id+"F7.wireOp",EDGE,"E231.MirrorCS");Q37=makeQuery(id+"F7.imprint","IMPRINT",FACE,{"disambiguationData":[TD([[makeQuery(id+"F7.imprint","IMPRINT",EDGE,{"derivedFrom":subQ0}),-1.0]])]});}
            var Q38;
            {var subQ2=sQuery(id+"F7.wireOp",EDGE,"E259.MirrorCS");Q38=makeQuery(id+"F7.imprint","IMPRINT",FACE,{"disambiguationData":[TD([[makeQuery(id+"F7.imprint","IMPRINT",EDGE,{"derivedFrom":subQ2}),-1.0]])]});}
            var Q39;
            {var subQ0=sQuery(id+"F7.wireOp",EDGE,"E262.MirrorCS");Q39=makeQuery(id+"F7.imprint","IMPRINT",FACE,{"disambiguationData":[TD([[makeQuery(id+"F7.imprint","IMPRINT",EDGE,{"derivedFrom":subQ0}),-1.0]])]});}
            var Q40;
            {var subQ0=sQuery(id+"F7.wireOp",EDGE,"E266.MirrorCS");Q40=makeQuery(id+"F7.imprint","IMPRINT",FACE,{"disambiguationData":[TD([[makeQuery(id+"F7.imprint","IMPRINT",EDGE,{"derivedFrom":subQ0}),-1.0]])]});}
            var Q41;
            {var subQ0=sQuery(id+"F7.wireOp",EDGE,"E270.MirrorCS");Q41=makeQuery(id+"F7.imprint","IMPRINT",FACE,{"disambiguationData":[TD([[makeQuery(id+"F7.imprint","IMPRINT",EDGE,{"derivedFrom":subQ0}),-1.0]])]});}
            var Q42;
            {var subQ0=sQuery(id+"F7.wireOp",EDGE,"E274.MirrorCS");Q42=makeQuery(id+"F7.imprint","IMPRINT",FACE,{"disambiguationData":[TD([[makeQuery(id+"F7.imprint","IMPRINT",EDGE,{"derivedFrom":subQ0}),-1.0]])]});}
            var Q43;
            {var subQ0=sQuery(id+"F7.wireOp",EDGE,"E278.MirrorCS");Q43=makeQuery(id+"F7.imprint","IMPRINT",FACE,{"disambiguationData":[TD([[makeQuery(id+"F7.imprint","IMPRINT",EDGE,{"derivedFrom":subQ0}),-1.0]])]});}
            var Q44;
            {var subQ0=sQuery(id+"F7.wireOp",EDGE,"E282.MirrorCS");Q44=makeQuery(id+"F7.imprint","IMPRINT",FACE,{"disambiguationData":[TD([[makeQuery(id+"F7.imprint","IMPRINT",EDGE,{"derivedFrom":subQ0}),-1.0]])]});}
            var Q45;
            {var subQ0=sQuery(id+"F7.wireOp",EDGE,"E286.MirrorCS");Q45=makeQuery(id+"F7.imprint","IMPRINT",FACE,{"disambiguationData":[TD([[makeQuery(id+"F7.imprint","IMPRINT",EDGE,{"derivedFrom":subQ0}),-1.0]])]});}
            var Q46;
            {var subQ0=sQuery(id+"F7.wireOp",EDGE,"E290.MirrorCS");Q46=makeQuery(id+"F7.imprint","IMPRINT",FACE,{"disambiguationData":[TD([[makeQuery(id+"F7.imprint","IMPRINT",EDGE,{"derivedFrom":subQ0}),-1.0]])]});}
            var Q47;
            {var subQ0=sQuery(id+"F7.wireOp",EDGE,"E294.MirrorCS");Q47=makeQuery(id+"F7.imprint","IMPRINT",FACE,{"disambiguationData":[TD([[makeQuery(id+"F7.imprint","IMPRINT",EDGE,{"derivedFrom":subQ0}),-1.0]])]});}
            var Q48;
            {var subQ0=sQuery(id+"F7.wireOp",EDGE,"E298.MirrorCS");Q48=makeQuery(id+"F7.imprint","IMPRINT",FACE,{"disambiguationData":[TD([[makeQuery(id+"F7.imprint","IMPRINT",EDGE,{"derivedFrom":subQ0}),-1.0]])]});}
            var Q49;
            {var subQ0=sQuery(id+"F7.wireOp",EDGE,"E302.MirrorCS");Q49=makeQuery(id+"F7.imprint","IMPRINT",FACE,{"disambiguationData":[TD([[makeQuery(id+"F7.imprint","IMPRINT",EDGE,{"derivedFrom":subQ0}),-1.0]])]});}
            var Q50;
            {var subQ0=sQuery(id+"F7.wireOp",EDGE,"E255.MirrorCS");Q50=makeQuery(id+"F7.imprint","IMPRINT",FACE,{"disambiguationData":[TD([[makeQuery(id+"F7.imprint","IMPRINT",EDGE,{"derivedFrom":subQ0}),-1.0]])]});}
            var Q51;
            {var subQ0=sQuery(id+"F7.wireOp",EDGE,"E251.MirrorCS");Q51=makeQuery(id+"F7.imprint","IMPRINT",FACE,{"disambiguationData":[TD([[makeQuery(id+"F7.imprint","IMPRINT",EDGE,{"derivedFrom":subQ0}),-1.0]])]});}
            var Q52;
            {var subQ0=sQuery(id+"F7.wireOp",EDGE,"E247.MirrorCS");Q52=makeQuery(id+"F7.imprint","IMPRINT",FACE,{"disambiguationData":[TD([[makeQuery(id+"F7.imprint","IMPRINT",EDGE,{"derivedFrom":subQ0}),-1.0]])]});}
            var Q53;
            {var subQ0=sQuery(id+"F7.wireOp",EDGE,"E243.MirrorCS");Q53=makeQuery(id+"F7.imprint","IMPRINT",FACE,{"disambiguationData":[TD([[makeQuery(id+"F7.imprint","IMPRINT",EDGE,{"derivedFrom":subQ0}),-1.0]])]});}
            var Q54;
            {var subQ0=sQuery(id+"F7.wireOp",EDGE,"E235.MirrorCS");Q54=makeQuery(id+"F7.imprint","IMPRINT",FACE,{"disambiguationData":[TD([[makeQuery(id+"F7.imprint","IMPRINT",EDGE,{"derivedFrom":subQ0}),-1.0]])]});}
            var Q55;
            {var subQ0=sQuery(id+"F7.wireOp",EDGE,"E239.MirrorCS");Q55=makeQuery(id+"F7.imprint","IMPRINT",FACE,{"disambiguationData":[TD([[makeQuery(id+"F7.imprint","IMPRINT",EDGE,{"derivedFrom":subQ0}),-1.0]])]});}
            extrude(context, id + "F12", {"entities" : qUnion([Q0, Q1, Q2, Q3, Q4, Q5, Q6, Q7, Q8, Q9, Q10, Q11, Q12, Q13, Q14, Q15, Q16, Q17, Q18, Q19, Q20, Q21, Q22, Q23, Q24, Q25, Q26, Q27, Q28, Q29, Q30, Q31, Q32, Q33, Q34, Q35, Q36, Q37, Q38, Q39, Q40, Q41, Q42, Q43, Q44, Q45, Q46, Q47, Q48, Q49, Q50, Q51, Q52, Q53, Q54, Q55]), "depth" : 3 * mm, "offsetDistance" : 25 * mm});
        }
    });
